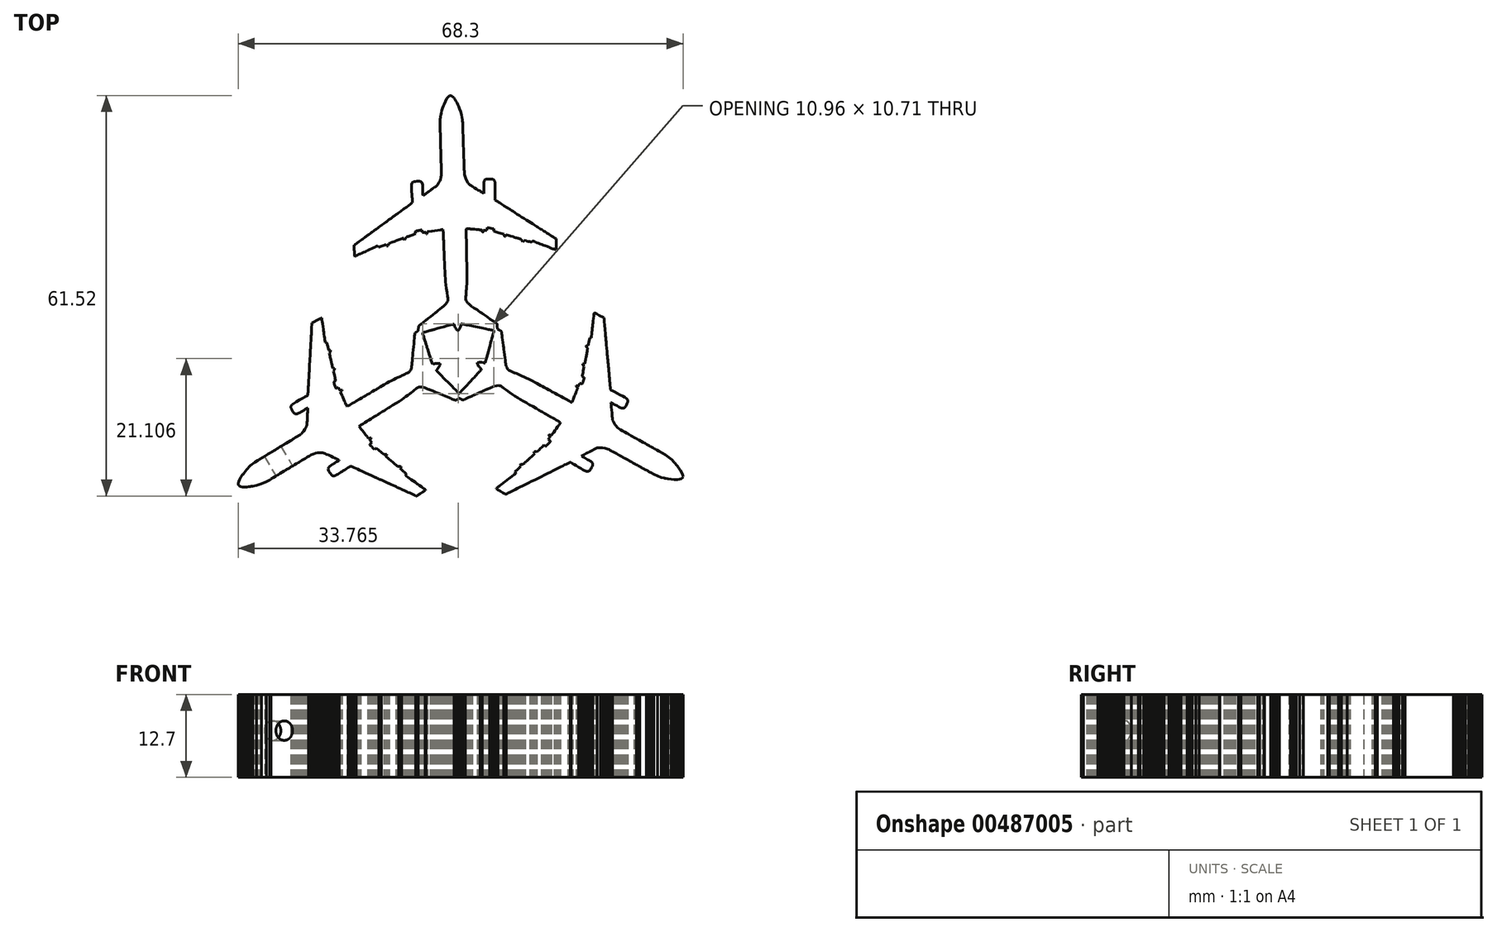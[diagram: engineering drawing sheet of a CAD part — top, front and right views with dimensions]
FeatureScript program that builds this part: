
annotation { "Feature Type Name" : "Feature", "Feature Type Description" : "" }
export const myFeature = defineFeature(function(context is Context, id is Id, definition is map)
    precondition{}
    {
        {
            var Q0;
            Q0=qCreatedBy(makeId("Top.planeOp"),FACE);
            var sketch = newSketch(context, id + "F0", { "sketchPlane" : qUnion([Q0])});
            skLineSegment(sketch, "E0", {"start": v(-1.7, 30.73) * mm, "end": v(-1.76, 30.7) * mm});
            skLineSegment(sketch, "E1", {"start": v(-1.76, 30.7) * mm, "end": v(-1.92, 30.58) * mm});
            skLineSegment(sketch, "E2", {"start": v(-1.92, 30.58) * mm, "end": v(-2.14, 30.3) * mm});
            skLineSegment(sketch, "E3", {"start": v(-2.14, 30.3) * mm, "end": v(-2.37, 29.87) * mm});
            skLineSegment(sketch, "E4", {"start": v(-2.37, 29.87) * mm, "end": v(-2.56, 29.43) * mm});
            skLineSegment(sketch, "E5", {"start": v(-2.56, 29.43) * mm, "end": v(-2.62, 29.28) * mm});
            skLineSegment(sketch, "E6", {"start": v(-2.62, 29.28) * mm, "end": v(-2.66, 29.17) * mm});
            skLineSegment(sketch, "E7", {"start": v(-2.66, 29.17) * mm, "end": v(-2.78, 28.85) * mm});
            skLineSegment(sketch, "E8", {"start": v(-2.78, 28.85) * mm, "end": v(-2.9, 28.46) * mm});
            skLineSegment(sketch, "E9", {"start": v(-2.9, 28.46) * mm, "end": v(-3, 28.1) * mm});
            skLineSegment(sketch, "E10", {"start": v(-3, 28.1) * mm, "end": v(-3.06, 27.8) * mm});
            skLineSegment(sketch, "E11", {"start": v(-3.06, 27.8) * mm, "end": v(-3.08, 27.7) * mm});
            skLineSegment(sketch, "E12", {"start": v(-3.08, 27.7) * mm, "end": v(-3.08, 27.67) * mm});
            skLineSegment(sketch, "E13", {"start": v(-3.08, 27.67) * mm, "end": v(-3.1, 27.57) * mm});
            skLineSegment(sketch, "E14", {"start": v(-3.1, 27.57) * mm, "end": v(-3.12, 27.45) * mm});
            skLineSegment(sketch, "E15", {"start": v(-3.12, 27.45) * mm, "end": v(-3.13, 27.34) * mm});
            skLineSegment(sketch, "E16", {"start": v(-3.13, 27.34) * mm, "end": v(-3.15, 27.22) * mm});
            skLineSegment(sketch, "E17", {"start": v(-3.15, 27.22) * mm, "end": v(-3.16, 27.09) * mm});
            skLineSegment(sketch, "E18", {"start": v(-3.16, 27.09) * mm, "end": v(-3.16, 26.94) * mm});
            skLineSegment(sketch, "E19", {"start": v(-3.16, 26.94) * mm, "end": v(-3.17, 26.77) * mm});
            skLineSegment(sketch, "E20", {"start": v(-3.17, 26.77) * mm, "end": v(-3.17, 26.57) * mm});
            skLineSegment(sketch, "E21", {"start": v(-3.17, 26.57) * mm, "end": v(-3.17, 26.33) * mm});
            skLineSegment(sketch, "E22", {"start": v(-3.17, 26.33) * mm, "end": v(-3.16, 26.04) * mm});
            skLineSegment(sketch, "E23", {"start": v(-3.16, 26.04) * mm, "end": v(-3.16, 25.7) * mm});
            skLineSegment(sketch, "E24", {"start": v(-3.16, 25.7) * mm, "end": v(-3.15, 25.3) * mm});
            skLineSegment(sketch, "E25", {"start": v(-3.15, 25.3) * mm, "end": v(-3.13, 24.85) * mm});
            skLineSegment(sketch, "E26", {"start": v(-3.13, 24.85) * mm, "end": v(-3.12, 24.31) * mm});
            skLineSegment(sketch, "E27", {"start": v(-3.12, 24.31) * mm, "end": v(-3.1, 23.7) * mm});
            skLineSegment(sketch, "E28", {"start": v(-3.1, 23.7) * mm, "end": v(-3.08, 23.18) * mm});
            skLineSegment(sketch, "E29", {"start": v(-3.08, 23.18) * mm, "end": v(-3.08, 23) * mm});
            skLineSegment(sketch, "E30", {"start": v(-3.08, 23) * mm, "end": v(-3.07, 22.82) * mm});
            skLineSegment(sketch, "E31", {"start": v(-3.07, 22.82) * mm, "end": v(-3.06, 22.27) * mm});
            skLineSegment(sketch, "E32", {"start": v(-3.06, 22.27) * mm, "end": v(-3.04, 21.63) * mm});
            skLineSegment(sketch, "E33", {"start": v(-3.04, 21.63) * mm, "end": v(-3.02, 21.08) * mm});
            skLineSegment(sketch, "E34", {"start": v(-3.02, 21.08) * mm, "end": v(-3.01, 20.6) * mm});
            skLineSegment(sketch, "E35", {"start": v(-3.01, 20.6) * mm, "end": v(-3, 20.17) * mm});
            skLineSegment(sketch, "E36", {"start": v(-3, 20.17) * mm, "end": v(-3, 19.79) * mm});
            skLineSegment(sketch, "E37", {"start": v(-3, 19.79) * mm, "end": v(-3, 19.44) * mm});
            skLineSegment(sketch, "E38", {"start": v(-3, 19.44) * mm, "end": v(-3, 19.19) * mm});
            skLineSegment(sketch, "E39", {"start": v(-3, 19.19) * mm, "end": v(-3, 19.1) * mm});
            skLineSegment(sketch, "E40", {"start": v(-3, 19.1) * mm, "end": v(-3, 19.03) * mm});
            skLineSegment(sketch, "E41", {"start": v(-3, 19.03) * mm, "end": v(-3, 18.81) * mm});
            skLineSegment(sketch, "E42", {"start": v(-3, 18.81) * mm, "end": v(-3, 18.59) * mm});
            skLineSegment(sketch, "E43", {"start": v(-3, 18.59) * mm, "end": v(-3, 18.42) * mm});
            skLineSegment(sketch, "E44", {"start": v(-3, 18.42) * mm, "end": v(-3, 18.3) * mm});
            skLineSegment(sketch, "E45", {"start": v(-3, 18.3) * mm, "end": v(-3.02, 18.2) * mm});
            skLineSegment(sketch, "E46", {"start": v(-3.02, 18.2) * mm, "end": v(-3.03, 18.12) * mm});
            skLineSegment(sketch, "E47", {"start": v(-3.03, 18.12) * mm, "end": v(-3.06, 18.04) * mm});
            skLineSegment(sketch, "E48", {"start": v(-3.06, 18.04) * mm, "end": v(-3.08, 17.97) * mm});
            skLineSegment(sketch, "E49", {"start": v(-3.08, 17.97) * mm, "end": v(-3.09, 17.95) * mm});
            skLineSegment(sketch, "E50", {"start": v(-3.09, 17.95) * mm, "end": v(-3.11, 17.88) * mm});
            skLineSegment(sketch, "E51", {"start": v(-3.11, 17.88) * mm, "end": v(-3.2, 17.68) * mm});
            skLineSegment(sketch, "E52", {"start": v(-3.2, 17.68) * mm, "end": v(-3.33, 17.4) * mm});
            skLineSegment(sketch, "E53", {"start": v(-3.33, 17.4) * mm, "end": v(-3.47, 17.16) * mm});
            skLineSegment(sketch, "E54", {"start": v(-3.47, 17.16) * mm, "end": v(-3.55, 17.03) * mm});
            skLineSegment(sketch, "E55", {"start": v(-3.55, 17.03) * mm, "end": v(-3.58, 17) * mm});
            skLineSegment(sketch, "E56", {"start": v(-3.58, 17) * mm, "end": v(-3.6, 16.99) * mm});
            skLineSegment(sketch, "E57", {"start": v(-3.6, 16.99) * mm, "end": v(-3.63, 16.95) * mm});
            skLineSegment(sketch, "E58", {"start": v(-3.63, 16.95) * mm, "end": v(-3.72, 16.88) * mm});
            skLineSegment(sketch, "E59", {"start": v(-3.72, 16.88) * mm, "end": v(-3.82, 16.8) * mm});
            skLineSegment(sketch, "E60", {"start": v(-3.82, 16.8) * mm, "end": v(-3.9, 16.74) * mm});
            skLineSegment(sketch, "E61", {"start": v(-3.9, 16.74) * mm, "end": v(-3.93, 16.72) * mm});
            skLineSegment(sketch, "E62", {"start": v(-3.93, 16.72) * mm, "end": v(-3.96, 16.7) * mm});
            skLineSegment(sketch, "E63", {"start": v(-3.96, 16.7) * mm, "end": v(-4.06, 16.63) * mm});
            skLineSegment(sketch, "E64", {"start": v(-4.06, 16.63) * mm, "end": v(-4.22, 16.52) * mm});
            skLineSegment(sketch, "E65", {"start": v(-4.22, 16.52) * mm, "end": v(-4.38, 16.4) * mm});
            skLineSegment(sketch, "E66", {"start": v(-4.38, 16.4) * mm, "end": v(-4.5, 16.31) * mm});
            skLineSegment(sketch, "E67", {"start": v(-4.5, 16.31) * mm, "end": v(-4.54, 16.29) * mm});
            skLineSegment(sketch, "E68", {"start": v(-4.54, 16.29) * mm, "end": v(-4.58, 16.26) * mm});
            skLineSegment(sketch, "E69", {"start": v(-4.58, 16.26) * mm, "end": v(-4.7, 16.17) * mm});
            skLineSegment(sketch, "E70", {"start": v(-4.7, 16.17) * mm, "end": v(-4.87, 16.05) * mm});
            skLineSegment(sketch, "E71", {"start": v(-4.87, 16.05) * mm, "end": v(-5.03, 15.93) * mm});
            skLineSegment(sketch, "E72", {"start": v(-5.03, 15.93) * mm, "end": v(-5.13, 15.86) * mm});
            skLineSegment(sketch, "E73", {"start": v(-5.13, 15.86) * mm, "end": v(-5.16, 15.83) * mm});
            skLineSegment(sketch, "E74", {"start": v(-5.16, 15.83) * mm, "end": v(-5.2, 15.81) * mm});
            skLineSegment(sketch, "E75", {"start": v(-5.2, 15.81) * mm, "end": v(-5.28, 15.75) * mm});
            skLineSegment(sketch, "E76", {"start": v(-5.28, 15.75) * mm, "end": v(-5.4, 15.66) * mm});
            skLineSegment(sketch, "E77", {"start": v(-5.4, 15.66) * mm, "end": v(-5.5, 15.58) * mm});
            skLineSegment(sketch, "E78", {"start": v(-5.5, 15.58) * mm, "end": v(-5.57, 15.54) * mm});
            skLineSegment(sketch, "E79", {"start": v(-5.57, 15.54) * mm, "end": v(-5.59, 15.52) * mm});
            skLineSegment(sketch, "E80", {"start": v(-5.59, 15.52) * mm, "end": v(-5.6, 15.51) * mm});
            skLineSegment(sketch, "E81", {"start": v(-5.6, 15.51) * mm, "end": v(-5.65, 15.48) * mm});
            skLineSegment(sketch, "E82", {"start": v(-5.65, 15.48) * mm, "end": v(-5.7, 15.45) * mm});
            skLineSegment(sketch, "E83", {"start": v(-5.7, 15.45) * mm, "end": v(-5.74, 15.42) * mm});
            skLineSegment(sketch, "E84", {"start": v(-5.74, 15.42) * mm, "end": v(-5.76, 15.41) * mm});
            skLineSegment(sketch, "E85", {"start": v(-5.76, 15.41) * mm, "end": v(-5.76, 15.41) * mm});
            skLineSegment(sketch, "E86", {"start": v(-5.76, 15.41) * mm, "end": v(-5.77, 15.41) * mm});
            skLineSegment(sketch, "E87", {"start": v(-5.77, 15.41) * mm, "end": v(-5.79, 15.46) * mm});
            skLineSegment(sketch, "E88", {"start": v(-5.79, 15.46) * mm, "end": v(-5.8, 15.61) * mm});
            skLineSegment(sketch, "E89", {"start": v(-5.8, 15.61) * mm, "end": v(-5.82, 15.9) * mm});
            skLineSegment(sketch, "E90", {"start": v(-5.82, 15.9) * mm, "end": v(-5.83, 16.22) * mm});
            skLineSegment(sketch, "E91", {"start": v(-5.83, 16.22) * mm, "end": v(-5.83, 16.32) * mm});
            skLineSegment(sketch, "E92", {"start": v(-5.83, 16.32) * mm, "end": v(-5.83, 16.42) * mm});
            skLineSegment(sketch, "E93", {"start": v(-5.83, 16.42) * mm, "end": v(-5.84, 16.71) * mm});
            skLineSegment(sketch, "E94", {"start": v(-5.84, 16.71) * mm, "end": v(-5.86, 17.01) * mm});
            skLineSegment(sketch, "E95", {"start": v(-5.86, 17.01) * mm, "end": v(-5.89, 17.22) * mm});
            skLineSegment(sketch, "E96", {"start": v(-5.89, 17.22) * mm, "end": v(-5.91, 17.32) * mm});
            skLineSegment(sketch, "E97", {"start": v(-5.91, 17.32) * mm, "end": v(-5.93, 17.35) * mm});
            skLineSegment(sketch, "E98", {"start": v(-5.93, 17.35) * mm, "end": v(-5.95, 17.38) * mm});
            skLineSegment(sketch, "E99", {"start": v(-5.95, 17.38) * mm, "end": v(-6.03, 17.48) * mm});
            skLineSegment(sketch, "E100", {"start": v(-6.03, 17.48) * mm, "end": v(-6.17, 17.56) * mm});
            skLineSegment(sketch, "E101", {"start": v(-6.17, 17.56) * mm, "end": v(-6.37, 17.6) * mm});
            skLineSegment(sketch, "E102", {"start": v(-6.37, 17.6) * mm, "end": v(-6.56, 17.61) * mm});
            skLineSegment(sketch, "E103", {"start": v(-6.56, 17.61) * mm, "end": v(-6.63, 17.6) * mm});
            skLineSegment(sketch, "E104", {"start": v(-6.63, 17.6) * mm, "end": v(-6.72, 17.6) * mm});
            skLineSegment(sketch, "E105", {"start": v(-6.72, 17.6) * mm, "end": v(-7, 17.58) * mm});
            skLineSegment(sketch, "E106", {"start": v(-7, 17.58) * mm, "end": v(-7.24, 17.53) * mm});
            skLineSegment(sketch, "E107", {"start": v(-7.24, 17.53) * mm, "end": v(-7.4, 17.44) * mm});
            skLineSegment(sketch, "E108", {"start": v(-7.4, 17.44) * mm, "end": v(-7.47, 17.35) * mm});
            skLineSegment(sketch, "E109", {"start": v(-7.47, 17.35) * mm, "end": v(-7.5, 17.31) * mm});
            skLineSegment(sketch, "E110", {"start": v(-7.5, 17.31) * mm, "end": v(-7.5, 17.27) * mm});
            skLineSegment(sketch, "E111", {"start": v(-7.5, 17.27) * mm, "end": v(-7.53, 17.09) * mm});
            skLineSegment(sketch, "E112", {"start": v(-7.53, 17.09) * mm, "end": v(-7.54, 16.67) * mm});
            skLineSegment(sketch, "E113", {"start": v(-7.54, 16.67) * mm, "end": v(-7.53, 16.07) * mm});
            skLineSegment(sketch, "E114", {"start": v(-7.53, 16.07) * mm, "end": v(-7.5, 15.5) * mm});
            skLineSegment(sketch, "E115", {"start": v(-7.5, 15.5) * mm, "end": v(-7.48, 15.31) * mm});
            skLineSegment(sketch, "E116", {"start": v(-7.48, 15.31) * mm, "end": v(-7.47, 15.23) * mm});
            skLineSegment(sketch, "E117", {"start": v(-7.47, 15.23) * mm, "end": v(-7.45, 14.96) * mm});
            skLineSegment(sketch, "E118", {"start": v(-7.45, 14.96) * mm, "end": v(-7.43, 14.67) * mm});
            skLineSegment(sketch, "E119", {"start": v(-7.43, 14.67) * mm, "end": v(-7.42, 14.46) * mm});
            skLineSegment(sketch, "E120", {"start": v(-7.42, 14.46) * mm, "end": v(-7.41, 14.4) * mm});
            skLineSegment(sketch, "E121", {"start": v(-7.41, 14.4) * mm, "end": v(-7.41, 14.37) * mm});
            skLineSegment(sketch, "E122", {"start": v(-7.41, 14.37) * mm, "end": v(-7.41, 14.36) * mm});
            skLineSegment(sketch, "E123", {"start": v(-7.41, 14.36) * mm, "end": v(-7.45, 14.32) * mm});
            skLineSegment(sketch, "E124", {"start": v(-7.45, 14.32) * mm, "end": v(-7.56, 14.23) * mm});
            skLineSegment(sketch, "E125", {"start": v(-7.56, 14.23) * mm, "end": v(-7.75, 14.08) * mm});
            skLineSegment(sketch, "E126", {"start": v(-7.75, 14.08) * mm, "end": v(-8, 13.88) * mm});
            skLineSegment(sketch, "E127", {"start": v(-8, 13.88) * mm, "end": v(-8.34, 13.64) * mm});
            skLineSegment(sketch, "E128", {"start": v(-8.34, 13.64) * mm, "end": v(-8.73, 13.35) * mm});
            skLineSegment(sketch, "E129", {"start": v(-8.73, 13.35) * mm, "end": v(-9.2, 13) * mm});
            skLineSegment(sketch, "E130", {"start": v(-9.2, 13) * mm, "end": v(-9.6, 12.72) * mm});
            skLineSegment(sketch, "E131", {"start": v(-9.6, 12.72) * mm, "end": v(-9.73, 12.63) * mm});
            skLineSegment(sketch, "E132", {"start": v(-9.73, 12.63) * mm, "end": v(-9.75, 12.6) * mm});
            skLineSegment(sketch, "E133", {"start": v(-9.75, 12.6) * mm, "end": v(-9.82, 12.56) * mm});
            skLineSegment(sketch, "E134", {"start": v(-9.82, 12.56) * mm, "end": v(-9.95, 12.47) * mm});
            skLineSegment(sketch, "E135", {"start": v(-9.95, 12.47) * mm, "end": v(-10.09, 12.37) * mm});
            skLineSegment(sketch, "E136", {"start": v(-10.09, 12.37) * mm, "end": v(-10.19, 12.3) * mm});
            skLineSegment(sketch, "E137", {"start": v(-10.19, 12.3) * mm, "end": v(-10.22, 12.27) * mm});
            skLineSegment(sketch, "E138", {"start": v(-10.22, 12.27) * mm, "end": v(-10.26, 12.24) * mm});
            skLineSegment(sketch, "E139", {"start": v(-10.26, 12.24) * mm, "end": v(-10.4, 12.13) * mm});
            skLineSegment(sketch, "E140", {"start": v(-10.4, 12.13) * mm, "end": v(-10.69, 11.92) * mm});
            skLineSegment(sketch, "E141", {"start": v(-10.69, 11.92) * mm, "end": v(-11.02, 11.68) * mm});
            skLineSegment(sketch, "E142", {"start": v(-11.02, 11.68) * mm, "end": v(-11.3, 11.48) * mm});
            skLineSegment(sketch, "E143", {"start": v(-11.3, 11.48) * mm, "end": v(-11.38, 11.42) * mm});
            skLineSegment(sketch, "E144", {"start": v(-11.38, 11.42) * mm, "end": v(-11.47, 11.35) * mm});
            skLineSegment(sketch, "E145", {"start": v(-11.47, 11.35) * mm, "end": v(-11.74, 11.16) * mm});
            skLineSegment(sketch, "E146", {"start": v(-11.74, 11.16) * mm, "end": v(-12.1, 10.9) * mm});
            skLineSegment(sketch, "E147", {"start": v(-12.1, 10.9) * mm, "end": v(-12.4, 10.67) * mm});
            skLineSegment(sketch, "E148", {"start": v(-12.4, 10.67) * mm, "end": v(-12.56, 10.55) * mm});
            skLineSegment(sketch, "E149", {"start": v(-12.56, 10.55) * mm, "end": v(-12.62, 10.51) * mm});
            skLineSegment(sketch, "E150", {"start": v(-12.62, 10.51) * mm, "end": v(-12.66, 10.48) * mm});
            skLineSegment(sketch, "E151", {"start": v(-12.66, 10.48) * mm, "end": v(-12.78, 10.4) * mm});
            skLineSegment(sketch, "E152", {"start": v(-12.78, 10.4) * mm, "end": v(-12.94, 10.28) * mm});
            skLineSegment(sketch, "E153", {"start": v(-12.94, 10.28) * mm, "end": v(-13.07, 10.18) * mm});
            skLineSegment(sketch, "E154", {"start": v(-13.07, 10.18) * mm, "end": v(-13.15, 10.12) * mm});
            skLineSegment(sketch, "E155", {"start": v(-13.15, 10.12) * mm, "end": v(-13.17, 10.1) * mm});
            skLineSegment(sketch, "E156", {"start": v(-13.17, 10.1) * mm, "end": v(-13.2, 10.1) * mm});
            skLineSegment(sketch, "E157", {"start": v(-13.2, 10.1) * mm, "end": v(-13.27, 10.04) * mm});
            skLineSegment(sketch, "E158", {"start": v(-13.27, 10.04) * mm, "end": v(-13.41, 9.93) * mm});
            skLineSegment(sketch, "E159", {"start": v(-13.41, 9.93) * mm, "end": v(-13.58, 9.8) * mm});
            skLineSegment(sketch, "E160", {"start": v(-13.58, 9.8) * mm, "end": v(-13.71, 9.71) * mm});
            skLineSegment(sketch, "E161", {"start": v(-13.71, 9.71) * mm, "end": v(-13.76, 9.68) * mm});
            skLineSegment(sketch, "E162", {"start": v(-13.76, 9.68) * mm, "end": v(-13.8, 9.65) * mm});
            skLineSegment(sketch, "E163", {"start": v(-13.8, 9.65) * mm, "end": v(-13.93, 9.55) * mm});
            skLineSegment(sketch, "E164", {"start": v(-13.93, 9.55) * mm, "end": v(-14.07, 9.45) * mm});
            skLineSegment(sketch, "E165", {"start": v(-14.07, 9.45) * mm, "end": v(-14.18, 9.36) * mm});
            skLineSegment(sketch, "E166", {"start": v(-14.18, 9.36) * mm, "end": v(-14.23, 9.33) * mm});
            skLineSegment(sketch, "E167", {"start": v(-14.23, 9.33) * mm, "end": v(-14.24, 9.32) * mm});
            skLineSegment(sketch, "E168", {"start": v(-14.24, 9.32) * mm, "end": v(-14.25, 9.32) * mm});
            skLineSegment(sketch, "E169", {"start": v(-14.25, 9.32) * mm, "end": v(-14.3, 9.28) * mm});
            skLineSegment(sketch, "E170", {"start": v(-14.3, 9.28) * mm, "end": v(-14.4, 9.21) * mm});
            skLineSegment(sketch, "E171", {"start": v(-14.4, 9.21) * mm, "end": v(-14.52, 9.12) * mm});
            skLineSegment(sketch, "E172", {"start": v(-14.52, 9.12) * mm, "end": v(-14.63, 9.04) * mm});
            skLineSegment(sketch, "E173", {"start": v(-14.63, 9.04) * mm, "end": v(-14.66, 9.01) * mm});
            skLineSegment(sketch, "E174", {"start": v(-14.66, 9.01) * mm, "end": v(-14.7, 8.99) * mm});
            skLineSegment(sketch, "E175", {"start": v(-14.7, 8.99) * mm, "end": v(-14.81, 8.9) * mm});
            skLineSegment(sketch, "E176", {"start": v(-14.81, 8.9) * mm, "end": v(-14.95, 8.8) * mm});
            skLineSegment(sketch, "E177", {"start": v(-14.95, 8.8) * mm, "end": v(-15.07, 8.72) * mm});
            skLineSegment(sketch, "E178", {"start": v(-15.07, 8.72) * mm, "end": v(-15.13, 8.67) * mm});
            skLineSegment(sketch, "E179", {"start": v(-15.13, 8.67) * mm, "end": v(-15.15, 8.66) * mm});
            skLineSegment(sketch, "E180", {"start": v(-15.15, 8.66) * mm, "end": v(-15.17, 8.64) * mm});
            skLineSegment(sketch, "E181", {"start": v(-15.17, 8.64) * mm, "end": v(-15.24, 8.59) * mm});
            skLineSegment(sketch, "E182", {"start": v(-15.24, 8.59) * mm, "end": v(-15.4, 8.48) * mm});
            skLineSegment(sketch, "E183", {"start": v(-15.4, 8.48) * mm, "end": v(-15.58, 8.34) * mm});
            skLineSegment(sketch, "E184", {"start": v(-15.58, 8.34) * mm, "end": v(-15.74, 8.23) * mm});
            skLineSegment(sketch, "E185", {"start": v(-15.74, 8.23) * mm, "end": v(-15.79, 8.2) * mm});
            skLineSegment(sketch, "E186", {"start": v(-15.79, 8.2) * mm, "end": v(-15.84, 8.15) * mm});
            skLineSegment(sketch, "E187", {"start": v(-15.84, 8.15) * mm, "end": v(-15.99, 8.04) * mm});
            skLineSegment(sketch, "E188", {"start": v(-15.99, 8.04) * mm, "end": v(-16.16, 7.92) * mm});
            skLineSegment(sketch, "E189", {"start": v(-16.16, 7.92) * mm, "end": v(-16.28, 7.83) * mm});
            skLineSegment(sketch, "E190", {"start": v(-16.28, 7.83) * mm, "end": v(-16.33, 7.8) * mm});
            skLineSegment(sketch, "E191", {"start": v(-16.33, 7.8) * mm, "end": v(-16.34, 7.8) * mm});
            skLineSegment(sketch, "E192", {"start": v(-16.34, 7.8) * mm, "end": v(-16.35, 7.79) * mm});
            skLineSegment(sketch, "E193", {"start": v(-16.35, 7.79) * mm, "end": v(-16.36, 7.75) * mm});
            skLineSegment(sketch, "E194", {"start": v(-16.36, 7.75) * mm, "end": v(-16.37, 7.63) * mm});
            skLineSegment(sketch, "E195", {"start": v(-16.37, 7.63) * mm, "end": v(-16.37, 7.4) * mm});
            skLineSegment(sketch, "E196", {"start": v(-16.37, 7.4) * mm, "end": v(-16.35, 7.08) * mm});
            skLineSegment(sketch, "E197", {"start": v(-16.35, 7.08) * mm, "end": v(-16.35, 6.98) * mm});
            skLineSegment(sketch, "E198", {"start": v(-16.35, 6.98) * mm, "end": v(-16.34, 6.9) * mm});
            skLineSegment(sketch, "E199", {"start": v(-16.34, 6.9) * mm, "end": v(-16.33, 6.67) * mm});
            skLineSegment(sketch, "E200", {"start": v(-16.33, 6.67) * mm, "end": v(-16.31, 6.4) * mm});
            skLineSegment(sketch, "E201", {"start": v(-16.31, 6.4) * mm, "end": v(-16.3, 6.21) * mm});
            skLineSegment(sketch, "E202", {"start": v(-16.3, 6.21) * mm, "end": v(-16.29, 6.13) * mm});
            skLineSegment(sketch, "E203", {"start": v(-16.29, 6.13) * mm, "end": v(-16.29, 6.12) * mm});
            skLineSegment(sketch, "E204", {"start": v(-16.29, 6.12) * mm, "end": v(-16.27, 6.05) * mm});
            skLineSegment(sketch, "E205", {"start": v(-16.27, 6.05) * mm, "end": v(-16.11, 6.13) * mm});
            skLineSegment(sketch, "E206", {"start": v(-16.11, 6.13) * mm, "end": v(-16.09, 6.14) * mm});
            skLineSegment(sketch, "E207", {"start": v(-16.09, 6.14) * mm, "end": v(-16, 6.18) * mm});
            skLineSegment(sketch, "E208", {"start": v(-16, 6.18) * mm, "end": v(-15.85, 6.25) * mm});
            skLineSegment(sketch, "E209", {"start": v(-15.85, 6.25) * mm, "end": v(-15.65, 6.34) * mm});
            skLineSegment(sketch, "E210", {"start": v(-15.65, 6.34) * mm, "end": v(-15.49, 6.42) * mm});
            skLineSegment(sketch, "E211", {"start": v(-15.49, 6.42) * mm, "end": v(-15.43, 6.44) * mm});
            skLineSegment(sketch, "E212", {"start": v(-15.43, 6.44) * mm, "end": v(-15.37, 6.47) * mm});
            skLineSegment(sketch, "E213", {"start": v(-15.37, 6.47) * mm, "end": v(-15.2, 6.55) * mm});
            skLineSegment(sketch, "E214", {"start": v(-15.2, 6.55) * mm, "end": v(-14.94, 6.67) * mm});
            skLineSegment(sketch, "E215", {"start": v(-14.94, 6.67) * mm, "end": v(-14.69, 6.78) * mm});
            skLineSegment(sketch, "E216", {"start": v(-14.69, 6.78) * mm, "end": v(-14.53, 6.85) * mm});
            skLineSegment(sketch, "E217", {"start": v(-14.53, 6.85) * mm, "end": v(-14.48, 6.88) * mm});
            skLineSegment(sketch, "E218", {"start": v(-14.48, 6.88) * mm, "end": v(-14.41, 6.9) * mm});
            skLineSegment(sketch, "E219", {"start": v(-14.41, 6.9) * mm, "end": v(-14.22, 7) * mm});
            skLineSegment(sketch, "E220", {"start": v(-14.22, 7) * mm, "end": v(-13.94, 7.12) * mm});
            skLineSegment(sketch, "E221", {"start": v(-13.94, 7.12) * mm, "end": v(-13.67, 7.25) * mm});
            skLineSegment(sketch, "E222", {"start": v(-13.67, 7.25) * mm, "end": v(-13.4, 7.37) * mm});
            skLineSegment(sketch, "E223", {"start": v(-13.4, 7.37) * mm, "end": v(-13.17, 7.47) * mm});
            skLineSegment(sketch, "E224", {"start": v(-13.17, 7.47) * mm, "end": v(-12.98, 7.56) * mm});
            skLineSegment(sketch, "E225", {"start": v(-12.98, 7.56) * mm, "end": v(-12.85, 7.62) * mm});
            skLineSegment(sketch, "E226", {"start": v(-12.85, 7.62) * mm, "end": v(-12.8, 7.64) * mm});
            skLineSegment(sketch, "E227", {"start": v(-12.8, 7.64) * mm, "end": v(-12.8, 7.65) * mm});
            skLineSegment(sketch, "E228", {"start": v(-12.8, 7.65) * mm, "end": v(-12.79, 7.65) * mm});
            skLineSegment(sketch, "E229", {"start": v(-12.79, 7.65) * mm, "end": v(-12.75, 7.63) * mm});
            skLineSegment(sketch, "E230", {"start": v(-12.75, 7.63) * mm, "end": v(-12.7, 7.58) * mm});
            skLineSegment(sketch, "E231", {"start": v(-12.7, 7.58) * mm, "end": v(-12.7, 7.56) * mm});
            skLineSegment(sketch, "E232", {"start": v(-12.7, 7.56) * mm, "end": v(-12.65, 7.46) * mm});
            skLineSegment(sketch, "E233", {"start": v(-12.65, 7.46) * mm, "end": v(-12.12, 7.65) * mm});
            skLineSegment(sketch, "E234", {"start": v(-12.12, 7.65) * mm, "end": v(-12.07, 7.66) * mm});
            skLineSegment(sketch, "E235", {"start": v(-12.07, 7.66) * mm, "end": v(-11.91, 7.72) * mm});
            skLineSegment(sketch, "E236", {"start": v(-11.91, 7.72) * mm, "end": v(-11.73, 7.78) * mm});
            skLineSegment(sketch, "E237", {"start": v(-11.73, 7.78) * mm, "end": v(-11.6, 7.83) * mm});
            skLineSegment(sketch, "E238", {"start": v(-11.6, 7.83) * mm, "end": v(-11.54, 7.85) * mm});
            skLineSegment(sketch, "E239", {"start": v(-11.54, 7.85) * mm, "end": v(-11.53, 7.85) * mm});
            skLineSegment(sketch, "E240", {"start": v(-11.53, 7.85) * mm, "end": v(-11.52, 7.85) * mm});
            skLineSegment(sketch, "E241", {"start": v(-11.52, 7.85) * mm, "end": v(-11.48, 7.84) * mm});
            skLineSegment(sketch, "E242", {"start": v(-11.48, 7.84) * mm, "end": v(-11.45, 7.8) * mm});
            skLineSegment(sketch, "E243", {"start": v(-11.45, 7.8) * mm, "end": v(-11.44, 7.78) * mm});
            skLineSegment(sketch, "E244", {"start": v(-11.44, 7.78) * mm, "end": v(-11.43, 7.75) * mm});
            skLineSegment(sketch, "E245", {"start": v(-11.43, 7.75) * mm, "end": v(-11.37, 7.67) * mm});
            skLineSegment(sketch, "E246", {"start": v(-11.37, 7.67) * mm, "end": v(-11.28, 7.64) * mm});
            skLineSegment(sketch, "E247", {"start": v(-11.28, 7.64) * mm, "end": v(-11.2, 7.7) * mm});
            skLineSegment(sketch, "E248", {"start": v(-11.2, 7.7) * mm, "end": v(-11.13, 7.82) * mm});
            skLineSegment(sketch, "E249", {"start": v(-11.13, 7.82) * mm, "end": v(-11.11, 7.86) * mm});
            skLineSegment(sketch, "E250", {"start": v(-11.11, 7.86) * mm, "end": v(-11.05, 8.04) * mm});
            skLineSegment(sketch, "E251", {"start": v(-11.05, 8.04) * mm, "end": v(-10.73, 8.15) * mm});
            skLineSegment(sketch, "E252", {"start": v(-10.73, 8.15) * mm, "end": v(-10.7, 8.17) * mm});
            skLineSegment(sketch, "E253", {"start": v(-10.7, 8.17) * mm, "end": v(-10.57, 8.21) * mm});
            skLineSegment(sketch, "E254", {"start": v(-10.57, 8.21) * mm, "end": v(-10.37, 8.28) * mm});
            skLineSegment(sketch, "E255", {"start": v(-10.37, 8.28) * mm, "end": v(-10.16, 8.36) * mm});
            skLineSegment(sketch, "E256", {"start": v(-10.16, 8.36) * mm, "end": v(-10.01, 8.42) * mm});
            skLineSegment(sketch, "E257", {"start": v(-10.01, 8.42) * mm, "end": v(-9.96, 8.44) * mm});
            skLineSegment(sketch, "E258", {"start": v(-9.96, 8.44) * mm, "end": v(-9.92, 8.45) * mm});
            skLineSegment(sketch, "E259", {"start": v(-9.92, 8.45) * mm, "end": v(-9.78, 8.5) * mm});
            skLineSegment(sketch, "E260", {"start": v(-9.78, 8.5) * mm, "end": v(-9.58, 8.57) * mm});
            skLineSegment(sketch, "E261", {"start": v(-9.58, 8.57) * mm, "end": v(-9.39, 8.65) * mm});
            skLineSegment(sketch, "E262", {"start": v(-9.39, 8.65) * mm, "end": v(-9.2, 8.71) * mm});
            skLineSegment(sketch, "E263", {"start": v(-9.2, 8.71) * mm, "end": v(-9.03, 8.77) * mm});
            skLineSegment(sketch, "E264", {"start": v(-9.03, 8.77) * mm, "end": v(-8.9, 8.82) * mm});
            skLineSegment(sketch, "E265", {"start": v(-8.9, 8.82) * mm, "end": v(-8.8, 8.85) * mm});
            skLineSegment(sketch, "E266", {"start": v(-8.8, 8.85) * mm, "end": v(-8.78, 8.87) * mm});
            skLineSegment(sketch, "E267", {"start": v(-8.78, 8.87) * mm, "end": v(-8.77, 8.87) * mm});
            skLineSegment(sketch, "E268", {"start": v(-8.77, 8.87) * mm, "end": v(-8.77, 8.87) * mm});
            skLineSegment(sketch, "E269", {"start": v(-8.77, 8.87) * mm, "end": v(-8.76, 8.84) * mm});
            skLineSegment(sketch, "E270", {"start": v(-8.76, 8.84) * mm, "end": v(-8.74, 8.79) * mm});
            skLineSegment(sketch, "E271", {"start": v(-8.74, 8.79) * mm, "end": v(-8.74, 8.77) * mm});
            skLineSegment(sketch, "E272", {"start": v(-8.74, 8.77) * mm, "end": v(-8.73, 8.74) * mm});
            skLineSegment(sketch, "E273", {"start": v(-8.73, 8.74) * mm, "end": v(-8.68, 8.65) * mm});
            skLineSegment(sketch, "E274", {"start": v(-8.68, 8.65) * mm, "end": v(-8.62, 8.62) * mm});
            skLineSegment(sketch, "E275", {"start": v(-8.62, 8.62) * mm, "end": v(-8.54, 8.68) * mm});
            skLineSegment(sketch, "E276", {"start": v(-8.54, 8.68) * mm, "end": v(-8.47, 8.79) * mm});
            skLineSegment(sketch, "E277", {"start": v(-8.47, 8.79) * mm, "end": v(-8.45, 8.83) * mm});
            skLineSegment(sketch, "E278", {"start": v(-8.45, 8.83) * mm, "end": v(-8.45, 8.84) * mm});
            skLineSegment(sketch, "E279", {"start": v(-8.45, 8.84) * mm, "end": v(-8.43, 8.9) * mm});
            skLineSegment(sketch, "E280", {"start": v(-8.43, 8.9) * mm, "end": v(-8.4, 8.95) * mm});
            skLineSegment(sketch, "E281", {"start": v(-8.4, 8.95) * mm, "end": v(-8.37, 9) * mm});
            skLineSegment(sketch, "E282", {"start": v(-8.37, 9) * mm, "end": v(-8.36, 9.01) * mm});
            skLineSegment(sketch, "E283", {"start": v(-8.36, 9.01) * mm, "end": v(-8.35, 9.02) * mm});
            skLineSegment(sketch, "E284", {"start": v(-8.35, 9.02) * mm, "end": v(-8.35, 9.02) * mm});
            skLineSegment(sketch, "E285", {"start": v(-8.35, 9.02) * mm, "end": v(-8.3, 9.04) * mm});
            skLineSegment(sketch, "E286", {"start": v(-8.3, 9.04) * mm, "end": v(-8.2, 9.07) * mm});
            skLineSegment(sketch, "E287", {"start": v(-8.2, 9.07) * mm, "end": v(-8.07, 9.12) * mm});
            skLineSegment(sketch, "E288", {"start": v(-8.07, 9.12) * mm, "end": v(-7.95, 9.17) * mm});
            skLineSegment(sketch, "E289", {"start": v(-7.95, 9.17) * mm, "end": v(-7.9, 9.18) * mm});
            skLineSegment(sketch, "E290", {"start": v(-7.9, 9.18) * mm, "end": v(-7.86, 9.2) * mm});
            skLineSegment(sketch, "E291", {"start": v(-7.86, 9.2) * mm, "end": v(-7.72, 9.25) * mm});
            skLineSegment(sketch, "E292", {"start": v(-7.72, 9.25) * mm, "end": v(-7.53, 9.32) * mm});
            skLineSegment(sketch, "E293", {"start": v(-7.53, 9.32) * mm, "end": v(-7.36, 9.38) * mm});
            skLineSegment(sketch, "E294", {"start": v(-7.36, 9.38) * mm, "end": v(-7.25, 9.42) * mm});
            skLineSegment(sketch, "E295", {"start": v(-7.25, 9.42) * mm, "end": v(-7.22, 9.44) * mm});
            skLineSegment(sketch, "E296", {"start": v(-7.22, 9.44) * mm, "end": v(-6.94, 9.54) * mm});
            skLineSegment(sketch, "E297", {"start": v(-6.94, 9.54) * mm, "end": v(-6.96, 9.72) * mm});
            skLineSegment(sketch, "E298", {"start": v(-6.96, 9.72) * mm, "end": v(-6.96, 9.75) * mm});
            skLineSegment(sketch, "E299", {"start": v(-6.96, 9.75) * mm, "end": v(-6.97, 9.83) * mm});
            skLineSegment(sketch, "E300", {"start": v(-6.97, 9.83) * mm, "end": v(-6.97, 9.88) * mm});
            skLineSegment(sketch, "E301", {"start": v(-6.97, 9.88) * mm, "end": v(-6.94, 9.9) * mm});
            skLineSegment(sketch, "E302", {"start": v(-6.94, 9.9) * mm, "end": v(-6.9, 9.92) * mm});
            skLineSegment(sketch, "E303", {"start": v(-6.9, 9.92) * mm, "end": v(-6.89, 9.93) * mm});
            skLineSegment(sketch, "E304", {"start": v(-6.89, 9.93) * mm, "end": v(-6.87, 9.93) * mm});
            skLineSegment(sketch, "E305", {"start": v(-6.87, 9.93) * mm, "end": v(-6.82, 9.94) * mm});
            skLineSegment(sketch, "E306", {"start": v(-6.82, 9.94) * mm, "end": v(-6.7, 9.97) * mm});
            skLineSegment(sketch, "E307", {"start": v(-6.7, 9.97) * mm, "end": v(-6.55, 10) * mm});
            skLineSegment(sketch, "E308", {"start": v(-6.55, 10) * mm, "end": v(-6.43, 10.04) * mm});
            skLineSegment(sketch, "E309", {"start": v(-6.43, 10.04) * mm, "end": v(-6.4, 10.05) * mm});
            skLineSegment(sketch, "E310", {"start": v(-6.4, 10.05) * mm, "end": v(-6.35, 10.06) * mm});
            skLineSegment(sketch, "E311", {"start": v(-6.35, 10.06) * mm, "end": v(-6.24, 10.08) * mm});
            skLineSegment(sketch, "E312", {"start": v(-6.24, 10.08) * mm, "end": v(-6.1, 10.1) * mm});
            skLineSegment(sketch, "E313", {"start": v(-6.1, 10.1) * mm, "end": v(-6.01, 10.12) * mm});
            skLineSegment(sketch, "E314", {"start": v(-6.01, 10.12) * mm, "end": v(-5.98, 10.13) * mm});
            skLineSegment(sketch, "E315", {"start": v(-5.98, 10.13) * mm, "end": v(-5.97, 10.12) * mm});
            skLineSegment(sketch, "E316", {"start": v(-5.97, 10.12) * mm, "end": v(-5.97, 10.12) * mm});
            skLineSegment(sketch, "E317", {"start": v(-5.97, 10.12) * mm, "end": v(-5.95, 10.06) * mm});
            skLineSegment(sketch, "E318", {"start": v(-5.95, 10.06) * mm, "end": v(-5.92, 9.95) * mm});
            skLineSegment(sketch, "E319", {"start": v(-5.92, 9.95) * mm, "end": v(-5.92, 9.93) * mm});
            skLineSegment(sketch, "E320", {"start": v(-5.92, 9.93) * mm, "end": v(-5.88, 9.76) * mm});
            skLineSegment(sketch, "E321", {"start": v(-5.88, 9.76) * mm, "end": v(-5.61, 9.77) * mm});
            skLineSegment(sketch, "E322", {"start": v(-5.61, 9.77) * mm, "end": v(-5.34, 9.78) * mm});
            skLineSegment(sketch, "E323", {"start": v(-5.34, 9.78) * mm, "end": v(-5.31, 9.63) * mm});
            skLineSegment(sketch, "E324", {"start": v(-5.31, 9.63) * mm, "end": v(-5.3, 9.6) * mm});
            skLineSegment(sketch, "E325", {"start": v(-5.3, 9.6) * mm, "end": v(-5.27, 9.52) * mm});
            skLineSegment(sketch, "E326", {"start": v(-5.27, 9.52) * mm, "end": v(-5.23, 9.49) * mm});
            skLineSegment(sketch, "E327", {"start": v(-5.23, 9.49) * mm, "end": v(-5.18, 9.54) * mm});
            skLineSegment(sketch, "E328", {"start": v(-5.18, 9.54) * mm, "end": v(-5.15, 9.64) * mm});
            skLineSegment(sketch, "E329", {"start": v(-5.15, 9.64) * mm, "end": v(-5.14, 9.67) * mm});
            skLineSegment(sketch, "E330", {"start": v(-5.14, 9.67) * mm, "end": v(-5.1, 9.86) * mm});
            skLineSegment(sketch, "E331", {"start": v(-5.1, 9.86) * mm, "end": v(-4.49, 9.94) * mm});
            skLineSegment(sketch, "E332", {"start": v(-4.49, 9.94) * mm, "end": v(-4.37, 9.96) * mm});
            skLineSegment(sketch, "E333", {"start": v(-4.37, 9.96) * mm, "end": v(-4, 10.01) * mm});
            skLineSegment(sketch, "E334", {"start": v(-4, 10.01) * mm, "end": v(-3.53, 10.09) * mm});
            skLineSegment(sketch, "E335", {"start": v(-3.53, 10.09) * mm, "end": v(-3.11, 10.15) * mm});
            skLineSegment(sketch, "E336", {"start": v(-3.11, 10.15) * mm, "end": v(-2.9, 10.18) * mm});
            skLineSegment(sketch, "E337", {"start": v(-2.9, 10.18) * mm, "end": v(-2.84, 10.2) * mm});
            skLineSegment(sketch, "E338", {"start": v(-2.84, 10.2) * mm, "end": v(-2.72, 10.22) * mm});
            skLineSegment(sketch, "E339", {"start": v(-2.72, 10.22) * mm, "end": v(-2.7, 9.95) * mm});
            skLineSegment(sketch, "E340", {"start": v(-2.7, 9.95) * mm, "end": v(-2.7, 9.92) * mm});
            skLineSegment(sketch, "E341", {"start": v(-2.7, 9.92) * mm, "end": v(-2.68, 9.78) * mm});
            skLineSegment(sketch, "E342", {"start": v(-2.68, 9.78) * mm, "end": v(-2.67, 9.51) * mm});
            skLineSegment(sketch, "E343", {"start": v(-2.67, 9.51) * mm, "end": v(-2.66, 9.18) * mm});
            skLineSegment(sketch, "E344", {"start": v(-2.66, 9.18) * mm, "end": v(-2.65, 8.92) * mm});
            skLineSegment(sketch, "E345", {"start": v(-2.65, 8.92) * mm, "end": v(-2.64, 8.83) * mm});
            skLineSegment(sketch, "E346", {"start": v(-2.64, 8.83) * mm, "end": v(-2.64, 8.73) * mm});
            skLineSegment(sketch, "E347", {"start": v(-2.64, 8.73) * mm, "end": v(-2.62, 8.41) * mm});
            skLineSegment(sketch, "E348", {"start": v(-2.62, 8.41) * mm, "end": v(-2.6, 7.9) * mm});
            skLineSegment(sketch, "E349", {"start": v(-2.6, 7.9) * mm, "end": v(-2.58, 7.35) * mm});
            skLineSegment(sketch, "E350", {"start": v(-2.58, 7.35) * mm, "end": v(-2.56, 6.98) * mm});
            skLineSegment(sketch, "E351", {"start": v(-2.56, 6.98) * mm, "end": v(-2.56, 6.85) * mm});
            skLineSegment(sketch, "E352", {"start": v(-2.56, 6.85) * mm, "end": v(-2.55, 6.72) * mm});
            skLineSegment(sketch, "E353", {"start": v(-2.55, 6.72) * mm, "end": v(-2.53, 6.31) * mm});
            skLineSegment(sketch, "E354", {"start": v(-2.53, 6.31) * mm, "end": v(-2.5, 5.68) * mm});
            skLineSegment(sketch, "E355", {"start": v(-2.5, 5.68) * mm, "end": v(-2.48, 5.03) * mm});
            skLineSegment(sketch, "E356", {"start": v(-2.48, 5.03) * mm, "end": v(-2.46, 4.6) * mm});
            skLineSegment(sketch, "E357", {"start": v(-2.46, 4.6) * mm, "end": v(-2.46, 4.45) * mm});
            skLineSegment(sketch, "E358", {"start": v(-2.46, 4.45) * mm, "end": v(-2.45, 4.27) * mm});
            skLineSegment(sketch, "E359", {"start": v(-2.45, 4.27) * mm, "end": v(-2.43, 3.74) * mm});
            skLineSegment(sketch, "E360", {"start": v(-2.43, 3.74) * mm, "end": v(-2.4, 3.16) * mm});
            skLineSegment(sketch, "E361", {"start": v(-2.4, 3.16) * mm, "end": v(-2.37, 2.65) * mm});
            skLineSegment(sketch, "E362", {"start": v(-2.37, 2.65) * mm, "end": v(-2.33, 2.18) * mm});
            skLineSegment(sketch, "E363", {"start": v(-2.33, 2.18) * mm, "end": v(-2.27, 1.7) * mm});
            skLineSegment(sketch, "E364", {"start": v(-2.27, 1.7) * mm, "end": v(-2.2, 1.16) * mm});
            skLineSegment(sketch, "E365", {"start": v(-2.2, 1.16) * mm, "end": v(-2.1, 0.52) * mm});
            skLineSegment(sketch, "E366", {"start": v(-2.1, 0.52) * mm, "end": v(-2.02, -0.07) * mm});
            skLineSegment(sketch, "E367", {"start": v(-2.02, -0.07) * mm, "end": v(-1.99, -0.27) * mm});
            skLineSegment(sketch, "E368", {"start": v(-1.99, -0.27) * mm, "end": v(-1.98, -0.3) * mm});
            skLineSegment(sketch, "E369", {"start": v(-1.98, -0.3) * mm, "end": v(-1.97, -0.42) * mm});
            skLineSegment(sketch, "E370", {"start": v(-1.97, -0.42) * mm, "end": v(-1.96, -0.54) * mm});
            skLineSegment(sketch, "E371", {"start": v(-1.96, -0.54) * mm, "end": v(-1.96, -0.64) * mm});
            skLineSegment(sketch, "E372", {"start": v(-1.96, -0.64) * mm, "end": v(-1.96, -0.7) * mm});
            skLineSegment(sketch, "E373", {"start": v(-1.96, -0.7) * mm, "end": v(-1.97, -0.71) * mm});
            skLineSegment(sketch, "E374", {"start": v(-1.97, -0.71) * mm, "end": v(-1.98, -0.77) * mm});
            skLineSegment(sketch, "E375", {"start": v(-1.98, -0.77) * mm, "end": v(-2.06, -0.94) * mm});
            skLineSegment(sketch, "E376", {"start": v(-2.06, -0.94) * mm, "end": v(-2.22, -1.18) * mm});
            skLineSegment(sketch, "E377", {"start": v(-2.22, -1.18) * mm, "end": v(-2.45, -1.44) * mm});
            skLineSegment(sketch, "E378", {"start": v(-2.45, -1.44) * mm, "end": v(-2.67, -1.63) * mm});
            skLineSegment(sketch, "E379", {"start": v(-2.67, -1.63) * mm, "end": v(-2.74, -1.69) * mm});
            skLineSegment(sketch, "E380", {"start": v(-2.74, -1.69) * mm, "end": v(-2.77, -1.71) * mm});
            skLineSegment(sketch, "E381", {"start": v(-2.77, -1.71) * mm, "end": v(-2.9, -1.81) * mm});
            skLineSegment(sketch, "E382", {"start": v(-2.9, -1.81) * mm, "end": v(-3.16, -2.02) * mm});
            skLineSegment(sketch, "E383", {"start": v(-3.16, -2.02) * mm, "end": v(-3.49, -2.28) * mm});
            skLineSegment(sketch, "E384", {"start": v(-3.49, -2.28) * mm, "end": v(-3.76, -2.5) * mm});
            skLineSegment(sketch, "E385", {"start": v(-3.76, -2.5) * mm, "end": v(-3.85, -2.57) * mm});
            skLineSegment(sketch, "E386", {"start": v(-3.85, -2.57) * mm, "end": v(-3.95, -2.65) * mm});
            skLineSegment(sketch, "E387", {"start": v(-3.95, -2.65) * mm, "end": v(-4.24, -2.88) * mm});
            skLineSegment(sketch, "E388", {"start": v(-4.24, -2.88) * mm, "end": v(-4.63, -3.19) * mm});
            skLineSegment(sketch, "E389", {"start": v(-4.63, -3.19) * mm, "end": v(-4.99, -3.47) * mm});
            skLineSegment(sketch, "E390", {"start": v(-4.99, -3.47) * mm, "end": v(-5.2, -3.64) * mm});
            skLineSegment(sketch, "E391", {"start": v(-5.2, -3.64) * mm, "end": v(-5.26, -3.7) * mm});
            skLineSegment(sketch, "E392", {"start": v(-5.26, -3.7) * mm, "end": v(-5.31, -3.73) * mm});
            skLineSegment(sketch, "E393", {"start": v(-5.31, -3.73) * mm, "end": v(-5.47, -3.85) * mm});
            skLineSegment(sketch, "E394", {"start": v(-5.47, -3.85) * mm, "end": v(-5.65, -4) * mm});
            skLineSegment(sketch, "E395", {"start": v(-5.65, -4) * mm, "end": v(-5.78, -4.1) * mm});
            skLineSegment(sketch, "E396", {"start": v(-5.78, -4.1) * mm, "end": v(-5.84, -4.15) * mm});
            skLineSegment(sketch, "E397", {"start": v(-5.84, -4.15) * mm, "end": v(-5.85, -4.16) * mm});
            skLineSegment(sketch, "E398", {"start": v(-5.85, -4.16) * mm, "end": v(-5.86, -4.16) * mm});
            skLineSegment(sketch, "E399", {"start": v(-5.86, -4.16) * mm, "end": v(-5.9, -4.2) * mm});
            skLineSegment(sketch, "E400", {"start": v(-5.9, -4.2) * mm, "end": v(-5.98, -4.26) * mm});
            skLineSegment(sketch, "E401", {"start": v(-5.98, -4.26) * mm, "end": v(-6.09, -4.35) * mm});
            skLineSegment(sketch, "E402", {"start": v(-6.09, -4.35) * mm, "end": v(-6.18, -4.42) * mm});
            skLineSegment(sketch, "E403", {"start": v(-6.18, -4.42) * mm, "end": v(-6.2, -4.45) * mm});
            skLineSegment(sketch, "E404", {"start": v(-6.2, -4.45) * mm, "end": v(-6.5, -4.68) * mm});
            skLineSegment(sketch, "E405", {"start": v(-6.5, -4.68) * mm, "end": v(-6.52, -5.38) * mm});
            skLineSegment(sketch, "E406", {"start": v(-6.52, -5.38) * mm, "end": v(-6.75, -5.52) * mm});
            skLineSegment(sketch, "E407", {"start": v(-6.75, -5.52) * mm, "end": v(-6.77, -5.53) * mm});
            skLineSegment(sketch, "E408", {"start": v(-6.77, -5.53) * mm, "end": v(-6.84, -5.58) * mm});
            skLineSegment(sketch, "E409", {"start": v(-6.84, -5.58) * mm, "end": v(-6.92, -5.63) * mm});
            skLineSegment(sketch, "E410", {"start": v(-6.92, -5.63) * mm, "end": v(-6.98, -5.67) * mm});
            skLineSegment(sketch, "E411", {"start": v(-6.98, -5.67) * mm, "end": v(-7, -5.69) * mm});
            skLineSegment(sketch, "E412", {"start": v(-7, -5.69) * mm, "end": v(-7, -5.7) * mm});
            skLineSegment(sketch, "E413", {"start": v(-7, -5.7) * mm, "end": v(-7.01, -5.7) * mm});
            skLineSegment(sketch, "E414", {"start": v(-7.01, -5.7) * mm, "end": v(-7.03, -5.76) * mm});
            skLineSegment(sketch, "E415", {"start": v(-7.03, -5.76) * mm, "end": v(-7.05, -5.93) * mm});
            skLineSegment(sketch, "E416", {"start": v(-7.05, -5.93) * mm, "end": v(-7.08, -6.16) * mm});
            skLineSegment(sketch, "E417", {"start": v(-7.08, -6.16) * mm, "end": v(-7.1, -6.36) * mm});
            skLineSegment(sketch, "E418", {"start": v(-7.1, -6.36) * mm, "end": v(-7.1, -6.43) * mm});
            skLineSegment(sketch, "E419", {"start": v(-7.1, -6.43) * mm, "end": v(-7.12, -6.54) * mm});
            skLineSegment(sketch, "E420", {"start": v(-7.12, -6.54) * mm, "end": v(-7.15, -6.87) * mm});
            skLineSegment(sketch, "E421", {"start": v(-7.15, -6.87) * mm, "end": v(-7.2, -7.34) * mm});
            skLineSegment(sketch, "E422", {"start": v(-7.2, -7.34) * mm, "end": v(-7.24, -7.83) * mm});
            skLineSegment(sketch, "E423", {"start": v(-7.24, -7.83) * mm, "end": v(-7.28, -8.32) * mm});
            skLineSegment(sketch, "E424", {"start": v(-7.28, -8.32) * mm, "end": v(-7.33, -8.79) * mm});
            skLineSegment(sketch, "E425", {"start": v(-7.33, -8.79) * mm, "end": v(-7.37, -9.2) * mm});
            skLineSegment(sketch, "E426", {"start": v(-7.37, -9.2) * mm, "end": v(-7.4, -9.56) * mm});
            skLineSegment(sketch, "E427", {"start": v(-7.4, -9.56) * mm, "end": v(-7.42, -9.76) * mm});
            skLineSegment(sketch, "E428", {"start": v(-7.42, -9.76) * mm, "end": v(-7.42, -9.82) * mm});
            skLineSegment(sketch, "E429", {"start": v(-7.42, -9.82) * mm, "end": v(-7.43, -9.88) * mm});
            skLineSegment(sketch, "E430", {"start": v(-7.43, -9.88) * mm, "end": v(-7.44, -10.03) * mm});
            skLineSegment(sketch, "E431", {"start": v(-7.44, -10.03) * mm, "end": v(-7.47, -10.25) * mm});
            skLineSegment(sketch, "E432", {"start": v(-7.47, -10.25) * mm, "end": v(-7.48, -10.43) * mm});
            skLineSegment(sketch, "E433", {"start": v(-7.48, -10.43) * mm, "end": v(-7.5, -10.53) * mm});
            skLineSegment(sketch, "E434", {"start": v(-7.5, -10.53) * mm, "end": v(-7.5, -10.56) * mm});
            skLineSegment(sketch, "E435", {"start": v(-7.5, -10.56) * mm, "end": v(-7.5, -10.62) * mm});
            skLineSegment(sketch, "E436", {"start": v(-7.5, -10.62) * mm, "end": v(-7.53, -10.79) * mm});
            skLineSegment(sketch, "E437", {"start": v(-7.53, -10.79) * mm, "end": v(-7.58, -11.04) * mm});
            skLineSegment(sketch, "E438", {"start": v(-7.58, -11.04) * mm, "end": v(-7.64, -11.27) * mm});
            skLineSegment(sketch, "E439", {"start": v(-7.64, -11.27) * mm, "end": v(-7.68, -11.4) * mm});
            skLineSegment(sketch, "E440", {"start": v(-7.68, -11.4) * mm, "end": v(-7.7, -11.43) * mm});
            skLineSegment(sketch, "E441", {"start": v(-7.7, -11.43) * mm, "end": v(-7.72, -11.46) * mm});
            skLineSegment(sketch, "E442", {"start": v(-7.72, -11.46) * mm, "end": v(-7.78, -11.56) * mm});
            skLineSegment(sketch, "E443", {"start": v(-7.78, -11.56) * mm, "end": v(-7.86, -11.66) * mm});
            skLineSegment(sketch, "E444", {"start": v(-7.86, -11.66) * mm, "end": v(-7.95, -11.75) * mm});
            skLineSegment(sketch, "E445", {"start": v(-7.95, -11.75) * mm, "end": v(-8.03, -11.8) * mm});
            skLineSegment(sketch, "E446", {"start": v(-8.03, -11.8) * mm, "end": v(-8.05, -11.8) * mm});
            skLineSegment(sketch, "E447", {"start": v(-8.05, -11.8) * mm, "end": v(-8.08, -11.82) * mm});
            skLineSegment(sketch, "E448", {"start": v(-8.08, -11.82) * mm, "end": v(-8.16, -11.86) * mm});
            skLineSegment(sketch, "E449", {"start": v(-8.16, -11.86) * mm, "end": v(-8.34, -11.94) * mm});
            skLineSegment(sketch, "E450", {"start": v(-8.34, -11.94) * mm, "end": v(-8.56, -12.04) * mm});
            skLineSegment(sketch, "E451", {"start": v(-8.56, -12.04) * mm, "end": v(-8.8, -12.15) * mm});
            skLineSegment(sketch, "E452", {"start": v(-8.8, -12.15) * mm, "end": v(-9.02, -12.25) * mm});
            skLineSegment(sketch, "E453", {"start": v(-9.02, -12.25) * mm, "end": v(-9.22, -12.34) * mm});
            skLineSegment(sketch, "E454", {"start": v(-9.22, -12.34) * mm, "end": v(-9.35, -12.4) * mm});
            skLineSegment(sketch, "E455", {"start": v(-9.35, -12.4) * mm, "end": v(-9.4, -12.42) * mm});
            skLineSegment(sketch, "E456", {"start": v(-9.4, -12.42) * mm, "end": v(-9.41, -12.42) * mm});
            skLineSegment(sketch, "E457", {"start": v(-9.41, -12.42) * mm, "end": v(-9.43, -12.42) * mm});
            skLineSegment(sketch, "E458", {"start": v(-9.43, -12.42) * mm, "end": v(-9.5, -12.46) * mm});
            skLineSegment(sketch, "E459", {"start": v(-9.5, -12.46) * mm, "end": v(-9.7, -12.55) * mm});
            skLineSegment(sketch, "E460", {"start": v(-9.7, -12.55) * mm, "end": v(-9.98, -12.7) * mm});
            skLineSegment(sketch, "E461", {"start": v(-9.98, -12.7) * mm, "end": v(-10.3, -12.86) * mm});
            skLineSegment(sketch, "E462", {"start": v(-10.3, -12.86) * mm, "end": v(-10.65, -13.04) * mm});
            skLineSegment(sketch, "E463", {"start": v(-10.65, -13.04) * mm, "end": v(-10.98, -13.21) * mm});
            skLineSegment(sketch, "E464", {"start": v(-10.98, -13.21) * mm, "end": v(-11.27, -13.36) * mm});
            skLineSegment(sketch, "E465", {"start": v(-11.27, -13.36) * mm, "end": v(-11.42, -13.45) * mm});
            skLineSegment(sketch, "E466", {"start": v(-11.42, -13.45) * mm, "end": v(-11.47, -13.48) * mm});
            skLineSegment(sketch, "E467", {"start": v(-11.47, -13.48) * mm, "end": v(-11.54, -13.52) * mm});
            skLineSegment(sketch, "E468", {"start": v(-11.54, -13.52) * mm, "end": v(-11.73, -13.63) * mm});
            skLineSegment(sketch, "E469", {"start": v(-11.73, -13.63) * mm, "end": v(-12.04, -13.82) * mm});
            skLineSegment(sketch, "E470", {"start": v(-12.04, -13.82) * mm, "end": v(-12.36, -14) * mm});
            skLineSegment(sketch, "E471", {"start": v(-12.36, -14) * mm, "end": v(-12.6, -14.14) * mm});
            skLineSegment(sketch, "E472", {"start": v(-12.6, -14.14) * mm, "end": v(-12.67, -14.19) * mm});
            skLineSegment(sketch, "E473", {"start": v(-12.67, -14.19) * mm, "end": v(-12.74, -14.23) * mm});
            skLineSegment(sketch, "E474", {"start": v(-12.74, -14.23) * mm, "end": v(-12.96, -14.36) * mm});
            skLineSegment(sketch, "E475", {"start": v(-12.96, -14.36) * mm, "end": v(-13.28, -14.55) * mm});
            skLineSegment(sketch, "E476", {"start": v(-13.28, -14.55) * mm, "end": v(-13.57, -14.72) * mm});
            skLineSegment(sketch, "E477", {"start": v(-13.57, -14.72) * mm, "end": v(-13.75, -14.82) * mm});
            skLineSegment(sketch, "E478", {"start": v(-13.75, -14.82) * mm, "end": v(-13.8, -14.86) * mm});
            skLineSegment(sketch, "E479", {"start": v(-13.8, -14.86) * mm, "end": v(-13.86, -14.9) * mm});
            skLineSegment(sketch, "E480", {"start": v(-13.86, -14.9) * mm, "end": v(-14.04, -15) * mm});
            skLineSegment(sketch, "E481", {"start": v(-14.04, -15) * mm, "end": v(-14.32, -15.16) * mm});
            skLineSegment(sketch, "E482", {"start": v(-14.32, -15.16) * mm, "end": v(-14.62, -15.34) * mm});
            skLineSegment(sketch, "E483", {"start": v(-14.62, -15.34) * mm, "end": v(-14.83, -15.46) * mm});
            skLineSegment(sketch, "E484", {"start": v(-14.83, -15.46) * mm, "end": v(-14.9, -15.5) * mm});
            skLineSegment(sketch, "E485", {"start": v(-14.9, -15.5) * mm, "end": v(-14.97, -15.54) * mm});
            skLineSegment(sketch, "E486", {"start": v(-14.97, -15.54) * mm, "end": v(-15.17, -15.66) * mm});
            skLineSegment(sketch, "E487", {"start": v(-15.17, -15.66) * mm, "end": v(-15.47, -15.83) * mm});
            skLineSegment(sketch, "E488", {"start": v(-15.47, -15.83) * mm, "end": v(-15.74, -15.99) * mm});
            skLineSegment(sketch, "E489", {"start": v(-15.74, -15.99) * mm, "end": v(-15.9, -16.08) * mm});
            skLineSegment(sketch, "E490", {"start": v(-15.9, -16.08) * mm, "end": v(-15.96, -16.11) * mm});
            skLineSegment(sketch, "E491", {"start": v(-15.96, -16.11) * mm, "end": v(-16.05, -16.17) * mm});
            skLineSegment(sketch, "E492", {"start": v(-16.05, -16.17) * mm, "end": v(-16.32, -16.33) * mm});
            skLineSegment(sketch, "E493", {"start": v(-16.32, -16.33) * mm, "end": v(-16.63, -16.51) * mm});
            skLineSegment(sketch, "E494", {"start": v(-16.63, -16.51) * mm, "end": v(-16.88, -16.66) * mm});
            skLineSegment(sketch, "E495", {"start": v(-16.88, -16.66) * mm, "end": v(-17.1, -16.78) * mm});
            skLineSegment(sketch, "E496", {"start": v(-17.1, -16.78) * mm, "end": v(-17.26, -16.88) * mm});
            skLineSegment(sketch, "E497", {"start": v(-17.26, -16.88) * mm, "end": v(-17.37, -16.94) * mm});
            skLineSegment(sketch, "E498", {"start": v(-17.37, -16.94) * mm, "end": v(-17.44, -16.98) * mm});
            skLineSegment(sketch, "E499", {"start": v(-17.44, -16.98) * mm, "end": v(-17.46, -16.99) * mm});
            skLineSegment(sketch, "E500", {"start": v(-17.46, -16.99) * mm, "end": v(-17.47, -16.99) * mm});
            skLineSegment(sketch, "E501", {"start": v(-17.47, -16.99) * mm, "end": v(-17.47, -16.99) * mm});
            skLineSegment(sketch, "E502", {"start": v(-17.47, -16.99) * mm, "end": v(-17.49, -16.94) * mm});
            skLineSegment(sketch, "E503", {"start": v(-17.49, -16.94) * mm, "end": v(-17.54, -16.82) * mm});
            skLineSegment(sketch, "E504", {"start": v(-17.54, -16.82) * mm, "end": v(-17.62, -16.66) * mm});
            skLineSegment(sketch, "E505", {"start": v(-17.62, -16.66) * mm, "end": v(-17.69, -16.5) * mm});
            skLineSegment(sketch, "E506", {"start": v(-17.69, -16.5) * mm, "end": v(-17.7, -16.45) * mm});
            skLineSegment(sketch, "E507", {"start": v(-17.7, -16.45) * mm, "end": v(-17.74, -16.4) * mm});
            skLineSegment(sketch, "E508", {"start": v(-17.74, -16.4) * mm, "end": v(-17.82, -16.2) * mm});
            skLineSegment(sketch, "E509", {"start": v(-17.82, -16.2) * mm, "end": v(-17.95, -15.92) * mm});
            skLineSegment(sketch, "E510", {"start": v(-17.95, -15.92) * mm, "end": v(-18.09, -15.62) * mm});
            skLineSegment(sketch, "E511", {"start": v(-18.09, -15.62) * mm, "end": v(-18.18, -15.42) * mm});
            skLineSegment(sketch, "E512", {"start": v(-18.18, -15.42) * mm, "end": v(-18.2, -15.35) * mm});
            skLineSegment(sketch, "E513", {"start": v(-18.2, -15.35) * mm, "end": v(-18.47, -14.77) * mm});
            skLineSegment(sketch, "E514", {"start": v(-18.47, -14.77) * mm, "end": v(-18.33, -14.65) * mm});
            skLineSegment(sketch, "E515", {"start": v(-18.33, -14.65) * mm, "end": v(-18.32, -14.64) * mm});
            skLineSegment(sketch, "E516", {"start": v(-18.32, -14.64) * mm, "end": v(-18.28, -14.6) * mm});
            skLineSegment(sketch, "E517", {"start": v(-18.28, -14.6) * mm, "end": v(-18.23, -14.56) * mm});
            skLineSegment(sketch, "E518", {"start": v(-18.23, -14.56) * mm, "end": v(-18.2, -14.52) * mm});
            skLineSegment(sketch, "E519", {"start": v(-18.2, -14.52) * mm, "end": v(-18.19, -14.5) * mm});
            skLineSegment(sketch, "E520", {"start": v(-18.19, -14.5) * mm, "end": v(-18.19, -14.5) * mm});
            skLineSegment(sketch, "E521", {"start": v(-18.19, -14.5) * mm, "end": v(-18.22, -14.48) * mm});
            skLineSegment(sketch, "E522", {"start": v(-18.22, -14.48) * mm, "end": v(-18.28, -14.48) * mm});
            skLineSegment(sketch, "E523", {"start": v(-18.28, -14.48) * mm, "end": v(-18.37, -14.5) * mm});
            skLineSegment(sketch, "E524", {"start": v(-18.37, -14.5) * mm, "end": v(-18.45, -14.51) * mm});
            skLineSegment(sketch, "E525", {"start": v(-18.45, -14.51) * mm, "end": v(-18.48, -14.52) * mm});
            skLineSegment(sketch, "E526", {"start": v(-18.48, -14.52) * mm, "end": v(-18.49, -14.53) * mm});
            skLineSegment(sketch, "E527", {"start": v(-18.49, -14.53) * mm, "end": v(-18.52, -14.53) * mm});
            skLineSegment(sketch, "E528", {"start": v(-18.52, -14.53) * mm, "end": v(-18.56, -14.5) * mm});
            skLineSegment(sketch, "E529", {"start": v(-18.56, -14.5) * mm, "end": v(-18.6, -14.43) * mm});
            skLineSegment(sketch, "E530", {"start": v(-18.6, -14.43) * mm, "end": v(-18.66, -14.34) * mm});
            skLineSegment(sketch, "E531", {"start": v(-18.66, -14.34) * mm, "end": v(-18.67, -14.3) * mm});
            skLineSegment(sketch, "E532", {"start": v(-18.67, -14.3) * mm, "end": v(-18.8, -14.07) * mm});
            skLineSegment(sketch, "E533", {"start": v(-18.8, -14.07) * mm, "end": v(-18.98, -14.15) * mm});
            skLineSegment(sketch, "E534", {"start": v(-18.98, -14.15) * mm, "end": v(-19, -14.16) * mm});
            skLineSegment(sketch, "E535", {"start": v(-19, -14.16) * mm, "end": v(-19.06, -14.19) * mm});
            skLineSegment(sketch, "E536", {"start": v(-19.06, -14.19) * mm, "end": v(-19.12, -14.2) * mm});
            skLineSegment(sketch, "E537", {"start": v(-19.12, -14.2) * mm, "end": v(-19.16, -14.21) * mm});
            skLineSegment(sketch, "E538", {"start": v(-19.16, -14.21) * mm, "end": v(-19.18, -14.2) * mm});
            skLineSegment(sketch, "E539", {"start": v(-19.18, -14.2) * mm, "end": v(-19.18, -14.2) * mm});
            skLineSegment(sketch, "E540", {"start": v(-19.18, -14.2) * mm, "end": v(-19.19, -14.19) * mm});
            skLineSegment(sketch, "E541", {"start": v(-19.19, -14.19) * mm, "end": v(-19.2, -14.15) * mm});
            skLineSegment(sketch, "E542", {"start": v(-19.2, -14.15) * mm, "end": v(-19.24, -14.04) * mm});
            skLineSegment(sketch, "E543", {"start": v(-19.24, -14.04) * mm, "end": v(-19.3, -13.89) * mm});
            skLineSegment(sketch, "E544", {"start": v(-19.3, -13.89) * mm, "end": v(-19.35, -13.72) * mm});
            skLineSegment(sketch, "E545", {"start": v(-19.35, -13.72) * mm, "end": v(-19.4, -13.55) * mm});
            skLineSegment(sketch, "E546", {"start": v(-19.4, -13.55) * mm, "end": v(-19.45, -13.4) * mm});
            skLineSegment(sketch, "E547", {"start": v(-19.45, -13.4) * mm, "end": v(-19.49, -13.3) * mm});
            skLineSegment(sketch, "E548", {"start": v(-19.49, -13.3) * mm, "end": v(-19.5, -13.26) * mm});
            skLineSegment(sketch, "E549", {"start": v(-19.5, -13.26) * mm, "end": v(-19.5, -13.24) * mm});
            skLineSegment(sketch, "E550", {"start": v(-19.5, -13.24) * mm, "end": v(-19.5, -13.24) * mm});
            skLineSegment(sketch, "E551", {"start": v(-19.5, -13.24) * mm, "end": v(-19.49, -13.22) * mm});
            skLineSegment(sketch, "E552", {"start": v(-19.49, -13.22) * mm, "end": v(-19.45, -13.2) * mm});
            skLineSegment(sketch, "E553", {"start": v(-19.45, -13.2) * mm, "end": v(-19.4, -13.17) * mm});
            skLineSegment(sketch, "E554", {"start": v(-19.4, -13.17) * mm, "end": v(-19.36, -13.15) * mm});
            skLineSegment(sketch, "E555", {"start": v(-19.36, -13.15) * mm, "end": v(-19.34, -13.15) * mm});
            skLineSegment(sketch, "E556", {"start": v(-19.34, -13.15) * mm, "end": v(-19.32, -13.14) * mm});
            skLineSegment(sketch, "E557", {"start": v(-19.32, -13.14) * mm, "end": v(-19.26, -13.11) * mm});
            skLineSegment(sketch, "E558", {"start": v(-19.26, -13.11) * mm, "end": v(-19.22, -13.08) * mm});
            skLineSegment(sketch, "E559", {"start": v(-19.22, -13.08) * mm, "end": v(-19.2, -13.05) * mm});
            skLineSegment(sketch, "E560", {"start": v(-19.2, -13.05) * mm, "end": v(-19.2, -13.02) * mm});
            skLineSegment(sketch, "E561", {"start": v(-19.2, -13.02) * mm, "end": v(-19.21, -13) * mm});
            skLineSegment(sketch, "E562", {"start": v(-19.21, -13) * mm, "end": v(-19.21, -13) * mm});
            skLineSegment(sketch, "E563", {"start": v(-19.21, -13) * mm, "end": v(-19.23, -12.92) * mm});
            skLineSegment(sketch, "E564", {"start": v(-19.23, -12.92) * mm, "end": v(-19.27, -12.75) * mm});
            skLineSegment(sketch, "E565", {"start": v(-19.27, -12.75) * mm, "end": v(-19.32, -12.52) * mm});
            skLineSegment(sketch, "E566", {"start": v(-19.32, -12.52) * mm, "end": v(-19.37, -12.32) * mm});
            skLineSegment(sketch, "E567", {"start": v(-19.37, -12.32) * mm, "end": v(-19.38, -12.26) * mm});
            skLineSegment(sketch, "E568", {"start": v(-19.38, -12.26) * mm, "end": v(-19.54, -11.58) * mm});
            skLineSegment(sketch, "E569", {"start": v(-19.54, -11.58) * mm, "end": v(-19.44, -11.43) * mm});
            skLineSegment(sketch, "E570", {"start": v(-19.44, -11.43) * mm, "end": v(-19.42, -11.41) * mm});
            skLineSegment(sketch, "E571", {"start": v(-19.42, -11.41) * mm, "end": v(-19.4, -11.36) * mm});
            skLineSegment(sketch, "E572", {"start": v(-19.4, -11.36) * mm, "end": v(-19.36, -11.3) * mm});
            skLineSegment(sketch, "E573", {"start": v(-19.36, -11.3) * mm, "end": v(-19.34, -11.25) * mm});
            skLineSegment(sketch, "E574", {"start": v(-19.34, -11.25) * mm, "end": v(-19.33, -11.22) * mm});
            skLineSegment(sketch, "E575", {"start": v(-19.33, -11.22) * mm, "end": v(-19.33, -11.21) * mm});
            skLineSegment(sketch, "E576", {"start": v(-19.33, -11.21) * mm, "end": v(-19.33, -11.2) * mm});
            skLineSegment(sketch, "E577", {"start": v(-19.33, -11.2) * mm, "end": v(-19.35, -11.16) * mm});
            skLineSegment(sketch, "E578", {"start": v(-19.35, -11.16) * mm, "end": v(-19.38, -11.14) * mm});
            skLineSegment(sketch, "E579", {"start": v(-19.38, -11.14) * mm, "end": v(-19.44, -11.13) * mm});
            skLineSegment(sketch, "E580", {"start": v(-19.44, -11.13) * mm, "end": v(-19.5, -11.14) * mm});
            skLineSegment(sketch, "E581", {"start": v(-19.5, -11.14) * mm, "end": v(-19.52, -11.15) * mm});
            skLineSegment(sketch, "E582", {"start": v(-19.52, -11.15) * mm, "end": v(-19.53, -11.16) * mm});
            skLineSegment(sketch, "E583", {"start": v(-19.53, -11.16) * mm, "end": v(-19.59, -11.17) * mm});
            skLineSegment(sketch, "E584", {"start": v(-19.59, -11.17) * mm, "end": v(-19.62, -11.17) * mm});
            skLineSegment(sketch, "E585", {"start": v(-19.62, -11.17) * mm, "end": v(-19.63, -11.17) * mm});
            skLineSegment(sketch, "E586", {"start": v(-19.63, -11.17) * mm, "end": v(-19.63, -11.17) * mm});
            skLineSegment(sketch, "E587", {"start": v(-19.63, -11.17) * mm, "end": v(-19.64, -11.13) * mm});
            skLineSegment(sketch, "E588", {"start": v(-19.64, -11.13) * mm, "end": v(-19.66, -11.05) * mm});
            skLineSegment(sketch, "E589", {"start": v(-19.66, -11.05) * mm, "end": v(-19.69, -10.94) * mm});
            skLineSegment(sketch, "E590", {"start": v(-19.69, -10.94) * mm, "end": v(-19.71, -10.84) * mm});
            skLineSegment(sketch, "E591", {"start": v(-19.71, -10.84) * mm, "end": v(-19.72, -10.8) * mm});
            skLineSegment(sketch, "E592", {"start": v(-19.72, -10.8) * mm, "end": v(-19.73, -10.76) * mm});
            skLineSegment(sketch, "E593", {"start": v(-19.73, -10.76) * mm, "end": v(-19.76, -10.64) * mm});
            skLineSegment(sketch, "E594", {"start": v(-19.76, -10.64) * mm, "end": v(-19.8, -10.44) * mm});
            skLineSegment(sketch, "E595", {"start": v(-19.8, -10.44) * mm, "end": v(-19.85, -10.23) * mm});
            skLineSegment(sketch, "E596", {"start": v(-19.85, -10.23) * mm, "end": v(-19.89, -10.09) * mm});
            skLineSegment(sketch, "E597", {"start": v(-19.89, -10.09) * mm, "end": v(-19.9, -10.04) * mm});
            skLineSegment(sketch, "E598", {"start": v(-19.9, -10.04) * mm, "end": v(-19.9, -10) * mm});
            skLineSegment(sketch, "E599", {"start": v(-19.9, -10) * mm, "end": v(-19.94, -9.85) * mm});
            skLineSegment(sketch, "E600", {"start": v(-19.94, -9.85) * mm, "end": v(-20, -9.63) * mm});
            skLineSegment(sketch, "E601", {"start": v(-20, -9.63) * mm, "end": v(-20.04, -9.41) * mm});
            skLineSegment(sketch, "E602", {"start": v(-20.04, -9.41) * mm, "end": v(-20.08, -9.27) * mm});
            skLineSegment(sketch, "E603", {"start": v(-20.08, -9.27) * mm, "end": v(-20.09, -9.22) * mm});
            skLineSegment(sketch, "E604", {"start": v(-20.09, -9.22) * mm, "end": v(-20.18, -8.83) * mm});
            skLineSegment(sketch, "E605", {"start": v(-20.18, -8.83) * mm, "end": v(-20.07, -8.69) * mm});
            skLineSegment(sketch, "E606", {"start": v(-20.07, -8.69) * mm, "end": v(-20.06, -8.68) * mm});
            skLineSegment(sketch, "E607", {"start": v(-20.06, -8.68) * mm, "end": v(-20.03, -8.63) * mm});
            skLineSegment(sketch, "E608", {"start": v(-20.03, -8.63) * mm, "end": v(-20, -8.56) * mm});
            skLineSegment(sketch, "E609", {"start": v(-20, -8.56) * mm, "end": v(-19.98, -8.5) * mm});
            skLineSegment(sketch, "E610", {"start": v(-19.98, -8.5) * mm, "end": v(-19.97, -8.47) * mm});
            skLineSegment(sketch, "E611", {"start": v(-19.97, -8.47) * mm, "end": v(-19.97, -8.45) * mm});
            skLineSegment(sketch, "E612", {"start": v(-19.97, -8.45) * mm, "end": v(-19.97, -8.44) * mm});
            skLineSegment(sketch, "E613", {"start": v(-19.97, -8.44) * mm, "end": v(-19.98, -8.4) * mm});
            skLineSegment(sketch, "E614", {"start": v(-19.98, -8.4) * mm, "end": v(-20, -8.36) * mm});
            skLineSegment(sketch, "E615", {"start": v(-20, -8.36) * mm, "end": v(-20.08, -8.35) * mm});
            skLineSegment(sketch, "E616", {"start": v(-20.08, -8.35) * mm, "end": v(-20.17, -8.36) * mm});
            skLineSegment(sketch, "E617", {"start": v(-20.17, -8.36) * mm, "end": v(-20.2, -8.36) * mm});
            skLineSegment(sketch, "E618", {"start": v(-20.2, -8.36) * mm, "end": v(-20.2, -8.36) * mm});
            skLineSegment(sketch, "E619", {"start": v(-20.2, -8.36) * mm, "end": v(-20.25, -8.35) * mm});
            skLineSegment(sketch, "E620", {"start": v(-20.25, -8.35) * mm, "end": v(-20.28, -8.31) * mm});
            skLineSegment(sketch, "E621", {"start": v(-20.28, -8.31) * mm, "end": v(-20.28, -8.3) * mm});
            skLineSegment(sketch, "E622", {"start": v(-20.28, -8.3) * mm, "end": v(-20.29, -8.29) * mm});
            skLineSegment(sketch, "E623", {"start": v(-20.29, -8.29) * mm, "end": v(-20.3, -8.24) * mm});
            skLineSegment(sketch, "E624", {"start": v(-20.3, -8.24) * mm, "end": v(-20.33, -8.13) * mm});
            skLineSegment(sketch, "E625", {"start": v(-20.33, -8.13) * mm, "end": v(-20.36, -7.99) * mm});
            skLineSegment(sketch, "E626", {"start": v(-20.36, -7.99) * mm, "end": v(-20.4, -7.82) * mm});
            skLineSegment(sketch, "E627", {"start": v(-20.4, -7.82) * mm, "end": v(-20.44, -7.65) * mm});
            skLineSegment(sketch, "E628", {"start": v(-20.44, -7.65) * mm, "end": v(-20.48, -7.5) * mm});
            skLineSegment(sketch, "E629", {"start": v(-20.48, -7.5) * mm, "end": v(-20.5, -7.37) * mm});
            skLineSegment(sketch, "E630", {"start": v(-20.5, -7.37) * mm, "end": v(-20.52, -7.31) * mm});
            skLineSegment(sketch, "E631", {"start": v(-20.52, -7.31) * mm, "end": v(-20.52, -7.3) * mm});
            skLineSegment(sketch, "E632", {"start": v(-20.52, -7.3) * mm, "end": v(-20.53, -7.28) * mm});
            skLineSegment(sketch, "E633", {"start": v(-20.53, -7.28) * mm, "end": v(-20.54, -7.24) * mm});
            skLineSegment(sketch, "E634", {"start": v(-20.54, -7.24) * mm, "end": v(-20.56, -7.2) * mm});
            skLineSegment(sketch, "E635", {"start": v(-20.56, -7.2) * mm, "end": v(-20.6, -7.19) * mm});
            skLineSegment(sketch, "E636", {"start": v(-20.6, -7.19) * mm, "end": v(-20.66, -7.19) * mm});
            skLineSegment(sketch, "E637", {"start": v(-20.66, -7.19) * mm, "end": v(-20.68, -7.19) * mm});
            skLineSegment(sketch, "E638", {"start": v(-20.68, -7.19) * mm, "end": v(-20.7, -7.19) * mm});
            skLineSegment(sketch, "E639", {"start": v(-20.7, -7.19) * mm, "end": v(-20.77, -7.17) * mm});
            skLineSegment(sketch, "E640", {"start": v(-20.77, -7.17) * mm, "end": v(-20.8, -7.15) * mm});
            skLineSegment(sketch, "E641", {"start": v(-20.8, -7.15) * mm, "end": v(-20.8, -7.14) * mm});
            skLineSegment(sketch, "E642", {"start": v(-20.8, -7.14) * mm, "end": v(-20.8, -7.13) * mm});
            skLineSegment(sketch, "E643", {"start": v(-20.8, -7.13) * mm, "end": v(-20.82, -7.08) * mm});
            skLineSegment(sketch, "E644", {"start": v(-20.82, -7.08) * mm, "end": v(-20.83, -6.94) * mm});
            skLineSegment(sketch, "E645", {"start": v(-20.83, -6.94) * mm, "end": v(-20.86, -6.74) * mm});
            skLineSegment(sketch, "E646", {"start": v(-20.86, -6.74) * mm, "end": v(-20.89, -6.57) * mm});
            skLineSegment(sketch, "E647", {"start": v(-20.89, -6.57) * mm, "end": v(-20.9, -6.51) * mm});
            skLineSegment(sketch, "E648", {"start": v(-20.9, -6.51) * mm, "end": v(-20.9, -6.44) * mm});
            skLineSegment(sketch, "E649", {"start": v(-20.9, -6.44) * mm, "end": v(-20.94, -6.23) * mm});
            skLineSegment(sketch, "E650", {"start": v(-20.94, -6.23) * mm, "end": v(-20.98, -5.9) * mm});
            skLineSegment(sketch, "E651", {"start": v(-20.98, -5.9) * mm, "end": v(-21.03, -5.57) * mm});
            skLineSegment(sketch, "E652", {"start": v(-21.03, -5.57) * mm, "end": v(-21.07, -5.35) * mm});
            skLineSegment(sketch, "E653", {"start": v(-21.07, -5.35) * mm, "end": v(-21.08, -5.27) * mm});
            skLineSegment(sketch, "E654", {"start": v(-21.08, -5.27) * mm, "end": v(-21.1, -5.14) * mm});
            skLineSegment(sketch, "E655", {"start": v(-21.1, -5.14) * mm, "end": v(-21.15, -4.74) * mm});
            skLineSegment(sketch, "E656", {"start": v(-21.15, -4.74) * mm, "end": v(-21.22, -4.32) * mm});
            skLineSegment(sketch, "E657", {"start": v(-21.22, -4.32) * mm, "end": v(-21.27, -4) * mm});
            skLineSegment(sketch, "E658", {"start": v(-21.27, -4) * mm, "end": v(-21.3, -3.75) * mm});
            skLineSegment(sketch, "E659", {"start": v(-21.3, -3.75) * mm, "end": v(-21.33, -3.58) * mm});
            skLineSegment(sketch, "E660", {"start": v(-21.33, -3.58) * mm, "end": v(-21.35, -3.47) * mm});
            skLineSegment(sketch, "E661", {"start": v(-21.35, -3.47) * mm, "end": v(-21.36, -3.41) * mm});
            skLineSegment(sketch, "E662", {"start": v(-21.36, -3.41) * mm, "end": v(-21.36, -3.4) * mm});
            skLineSegment(sketch, "E663", {"start": v(-21.36, -3.4) * mm, "end": v(-21.37, -3.4) * mm});
            skLineSegment(sketch, "E664", {"start": v(-21.37, -3.4) * mm, "end": v(-21.37, -3.39) * mm});
            skLineSegment(sketch, "E665", {"start": v(-21.37, -3.39) * mm, "end": v(-21.43, -3.41) * mm});
            skLineSegment(sketch, "E666", {"start": v(-21.43, -3.41) * mm, "end": v(-21.62, -3.5) * mm});
            skLineSegment(sketch, "E667", {"start": v(-21.62, -3.5) * mm, "end": v(-21.92, -3.67) * mm});
            skLineSegment(sketch, "E668", {"start": v(-21.92, -3.67) * mm, "end": v(-22.25, -3.85) * mm});
            skLineSegment(sketch, "E669", {"start": v(-22.25, -3.85) * mm, "end": v(-22.36, -3.91) * mm});
            skLineSegment(sketch, "E670", {"start": v(-22.36, -3.91) * mm, "end": v(-22.84, -4.18) * mm});
            skLineSegment(sketch, "E671", {"start": v(-22.84, -4.18) * mm, "end": v(-22.9, -5.09) * mm});
            skLineSegment(sketch, "E672", {"start": v(-22.9, -5.09) * mm, "end": v(-22.9, -5.18) * mm});
            skLineSegment(sketch, "E673", {"start": v(-22.9, -5.18) * mm, "end": v(-22.92, -5.47) * mm});
            skLineSegment(sketch, "E674", {"start": v(-22.92, -5.47) * mm, "end": v(-22.94, -5.86) * mm});
            skLineSegment(sketch, "E675", {"start": v(-22.94, -5.86) * mm, "end": v(-22.96, -6.19) * mm});
            skLineSegment(sketch, "E676", {"start": v(-22.96, -6.19) * mm, "end": v(-22.97, -6.37) * mm});
            skLineSegment(sketch, "E677", {"start": v(-22.97, -6.37) * mm, "end": v(-22.97, -6.43) * mm});
            skLineSegment(sketch, "E678", {"start": v(-22.97, -6.43) * mm, "end": v(-22.98, -6.54) * mm});
            skLineSegment(sketch, "E679", {"start": v(-22.98, -6.54) * mm, "end": v(-23, -6.85) * mm});
            skLineSegment(sketch, "E680", {"start": v(-23, -6.85) * mm, "end": v(-23.02, -7.35) * mm});
            skLineSegment(sketch, "E681", {"start": v(-23.02, -7.35) * mm, "end": v(-23.05, -7.84) * mm});
            skLineSegment(sketch, "E682", {"start": v(-23.05, -7.84) * mm, "end": v(-23.07, -8.13) * mm});
            skLineSegment(sketch, "E683", {"start": v(-23.07, -8.13) * mm, "end": v(-23.08, -8.23) * mm});
            skLineSegment(sketch, "E684", {"start": v(-23.08, -8.23) * mm, "end": v(-23.08, -8.26) * mm});
            skLineSegment(sketch, "E685", {"start": v(-23.08, -8.26) * mm, "end": v(-23.1, -8.5) * mm});
            skLineSegment(sketch, "E686", {"start": v(-23.1, -8.5) * mm, "end": v(-23.1, -8.75) * mm});
            skLineSegment(sketch, "E687", {"start": v(-23.1, -8.75) * mm, "end": v(-23.1, -8.8) * mm});
            skLineSegment(sketch, "E688", {"start": v(-23.1, -8.8) * mm, "end": v(-23.11, -8.9) * mm});
            skLineSegment(sketch, "E689", {"start": v(-23.11, -8.9) * mm, "end": v(-23.13, -9.23) * mm});
            skLineSegment(sketch, "E690", {"start": v(-23.13, -9.23) * mm, "end": v(-23.15, -9.63) * mm});
            skLineSegment(sketch, "E691", {"start": v(-23.15, -9.63) * mm, "end": v(-23.18, -10.07) * mm});
            skLineSegment(sketch, "E692", {"start": v(-23.18, -10.07) * mm, "end": v(-23.2, -10.5) * mm});
            skLineSegment(sketch, "E693", {"start": v(-23.2, -10.5) * mm, "end": v(-23.2, -10.64) * mm});
            skLineSegment(sketch, "E694", {"start": v(-23.2, -10.64) * mm, "end": v(-23.21, -10.74) * mm});
            skLineSegment(sketch, "E695", {"start": v(-23.21, -10.74) * mm, "end": v(-23.23, -11.02) * mm});
            skLineSegment(sketch, "E696", {"start": v(-23.23, -11.02) * mm, "end": v(-23.25, -11.32) * mm});
            skLineSegment(sketch, "E697", {"start": v(-23.25, -11.32) * mm, "end": v(-23.26, -11.6) * mm});
            skLineSegment(sketch, "E698", {"start": v(-23.26, -11.6) * mm, "end": v(-23.28, -11.86) * mm});
            skLineSegment(sketch, "E699", {"start": v(-23.28, -11.86) * mm, "end": v(-23.3, -12.16) * mm});
            skLineSegment(sketch, "E700", {"start": v(-23.3, -12.16) * mm, "end": v(-23.32, -12.53) * mm});
            skLineSegment(sketch, "E701", {"start": v(-23.32, -12.53) * mm, "end": v(-23.34, -13.02) * mm});
            skLineSegment(sketch, "E702", {"start": v(-23.34, -13.02) * mm, "end": v(-23.37, -13.5) * mm});
            skLineSegment(sketch, "E703", {"start": v(-23.37, -13.5) * mm, "end": v(-23.38, -13.65) * mm});
            skLineSegment(sketch, "E704", {"start": v(-23.38, -13.65) * mm, "end": v(-23.38, -13.73) * mm});
            skLineSegment(sketch, "E705", {"start": v(-23.38, -13.73) * mm, "end": v(-23.4, -13.97) * mm});
            skLineSegment(sketch, "E706", {"start": v(-23.4, -13.97) * mm, "end": v(-23.41, -14.28) * mm});
            skLineSegment(sketch, "E707", {"start": v(-23.41, -14.28) * mm, "end": v(-23.43, -14.55) * mm});
            skLineSegment(sketch, "E708", {"start": v(-23.43, -14.55) * mm, "end": v(-23.45, -14.8) * mm});
            skLineSegment(sketch, "E709", {"start": v(-23.45, -14.8) * mm, "end": v(-23.46, -15) * mm});
            skLineSegment(sketch, "E710", {"start": v(-23.46, -15) * mm, "end": v(-23.48, -15.15) * mm});
            skLineSegment(sketch, "E711", {"start": v(-23.48, -15.15) * mm, "end": v(-23.48, -15.25) * mm});
            skLineSegment(sketch, "E712", {"start": v(-23.48, -15.25) * mm, "end": v(-23.49, -15.28) * mm});
            skLineSegment(sketch, "E713", {"start": v(-23.49, -15.28) * mm, "end": v(-23.5, -15.28) * mm});
            skLineSegment(sketch, "E714", {"start": v(-23.5, -15.28) * mm, "end": v(-23.5, -15.29) * mm});
            skLineSegment(sketch, "E715", {"start": v(-23.5, -15.29) * mm, "end": v(-23.54, -15.32) * mm});
            skLineSegment(sketch, "E716", {"start": v(-23.54, -15.32) * mm, "end": v(-23.67, -15.39) * mm});
            skLineSegment(sketch, "E717", {"start": v(-23.67, -15.39) * mm, "end": v(-23.86, -15.5) * mm});
            skLineSegment(sketch, "E718", {"start": v(-23.86, -15.5) * mm, "end": v(-24.03, -15.58) * mm});
            skLineSegment(sketch, "E719", {"start": v(-24.03, -15.58) * mm, "end": v(-24.08, -15.61) * mm});
            skLineSegment(sketch, "E720", {"start": v(-24.08, -15.61) * mm, "end": v(-24.25, -15.7) * mm});
            skLineSegment(sketch, "E721", {"start": v(-24.25, -15.7) * mm, "end": v(-24.76, -15.98) * mm});
            skLineSegment(sketch, "E722", {"start": v(-24.76, -15.98) * mm, "end": v(-25.29, -16.3) * mm});
            skLineSegment(sketch, "E723", {"start": v(-25.29, -16.3) * mm, "end": v(-25.67, -16.53) * mm});
            skLineSegment(sketch, "E724", {"start": v(-25.67, -16.53) * mm, "end": v(-25.84, -16.65) * mm});
            skLineSegment(sketch, "E725", {"start": v(-25.84, -16.65) * mm, "end": v(-25.89, -16.69) * mm});
            skLineSegment(sketch, "E726", {"start": v(-25.89, -16.69) * mm, "end": v(-25.9, -16.7) * mm});
            skLineSegment(sketch, "E727", {"start": v(-25.9, -16.7) * mm, "end": v(-25.98, -16.78) * mm});
            skLineSegment(sketch, "E728", {"start": v(-25.98, -16.78) * mm, "end": v(-26.03, -16.84) * mm});
            skLineSegment(sketch, "E729", {"start": v(-26.03, -16.84) * mm, "end": v(-26.06, -16.92) * mm});
            skLineSegment(sketch, "E730", {"start": v(-26.06, -16.92) * mm, "end": v(-26.07, -16.99) * mm});
            skLineSegment(sketch, "E731", {"start": v(-26.07, -16.99) * mm, "end": v(-26.07, -17.01) * mm});
            skLineSegment(sketch, "E732", {"start": v(-26.07, -17.01) * mm, "end": v(-26.07, -17.03) * mm});
            skLineSegment(sketch, "E733", {"start": v(-26.07, -17.03) * mm, "end": v(-26.08, -17.07) * mm});
            skLineSegment(sketch, "E734", {"start": v(-26.08, -17.07) * mm, "end": v(-26.08, -17.12) * mm});
            skLineSegment(sketch, "E735", {"start": v(-26.08, -17.12) * mm, "end": v(-26.07, -17.16) * mm});
            skLineSegment(sketch, "E736", {"start": v(-26.07, -17.16) * mm, "end": v(-26.06, -17.21) * mm});
            skLineSegment(sketch, "E737", {"start": v(-26.06, -17.21) * mm, "end": v(-26.04, -17.26) * mm});
            skLineSegment(sketch, "E738", {"start": v(-26.04, -17.26) * mm, "end": v(-26.01, -17.33) * mm});
            skLineSegment(sketch, "E739", {"start": v(-26.01, -17.33) * mm, "end": v(-25.98, -17.4) * mm});
            skLineSegment(sketch, "E740", {"start": v(-25.98, -17.4) * mm, "end": v(-25.94, -17.48) * mm});
            skLineSegment(sketch, "E741", {"start": v(-25.94, -17.48) * mm, "end": v(-25.93, -17.5) * mm});
            skLineSegment(sketch, "E742", {"start": v(-25.93, -17.5) * mm, "end": v(-25.89, -17.58) * mm});
            skLineSegment(sketch, "E743", {"start": v(-25.89, -17.58) * mm, "end": v(-25.75, -17.82) * mm});
            skLineSegment(sketch, "E744", {"start": v(-25.75, -17.82) * mm, "end": v(-25.6, -18.03) * mm});
            skLineSegment(sketch, "E745", {"start": v(-25.6, -18.03) * mm, "end": v(-25.44, -18.13) * mm});
            skLineSegment(sketch, "E746", {"start": v(-25.44, -18.13) * mm, "end": v(-25.3, -18.17) * mm});
            skLineSegment(sketch, "E747", {"start": v(-25.3, -18.17) * mm, "end": v(-25.26, -18.17) * mm});
            skLineSegment(sketch, "E748", {"start": v(-25.26, -18.17) * mm, "end": v(-25.25, -18.17) * mm});
            skLineSegment(sketch, "E749", {"start": v(-25.25, -18.17) * mm, "end": v(-25.2, -18.16) * mm});
            skLineSegment(sketch, "E750", {"start": v(-25.2, -18.16) * mm, "end": v(-25.11, -18.14) * mm});
            skLineSegment(sketch, "E751", {"start": v(-25.11, -18.14) * mm, "end": v(-25.01, -18.1) * mm});
            skLineSegment(sketch, "E752", {"start": v(-25.01, -18.1) * mm, "end": v(-24.88, -18.03) * mm});
            skLineSegment(sketch, "E753", {"start": v(-24.88, -18.03) * mm, "end": v(-24.72, -17.95) * mm});
            skLineSegment(sketch, "E754", {"start": v(-24.72, -17.95) * mm, "end": v(-24.52, -17.83) * mm});
            skLineSegment(sketch, "E755", {"start": v(-24.52, -17.83) * mm, "end": v(-24.27, -17.68) * mm});
            skLineSegment(sketch, "E756", {"start": v(-24.27, -17.68) * mm, "end": v(-24.04, -17.54) * mm});
            skLineSegment(sketch, "E757", {"start": v(-24.04, -17.54) * mm, "end": v(-23.96, -17.49) * mm});
            skLineSegment(sketch, "E758", {"start": v(-23.96, -17.49) * mm, "end": v(-23.92, -17.46) * mm});
            skLineSegment(sketch, "E759", {"start": v(-23.92, -17.46) * mm, "end": v(-23.8, -17.39) * mm});
            skLineSegment(sketch, "E760", {"start": v(-23.8, -17.39) * mm, "end": v(-23.65, -17.3) * mm});
            skLineSegment(sketch, "E761", {"start": v(-23.65, -17.3) * mm, "end": v(-23.56, -17.25) * mm});
            skLineSegment(sketch, "E762", {"start": v(-23.56, -17.25) * mm, "end": v(-23.52, -17.23) * mm});
            skLineSegment(sketch, "E763", {"start": v(-23.52, -17.23) * mm, "end": v(-23.51, -17.23) * mm});
            skLineSegment(sketch, "E764", {"start": v(-23.51, -17.23) * mm, "end": v(-23.51, -17.23) * mm});
            skLineSegment(sketch, "E765", {"start": v(-23.51, -17.23) * mm, "end": v(-23.5, -17.26) * mm});
            skLineSegment(sketch, "E766", {"start": v(-23.5, -17.26) * mm, "end": v(-23.5, -17.36) * mm});
            skLineSegment(sketch, "E767", {"start": v(-23.5, -17.36) * mm, "end": v(-23.5, -17.5) * mm});
            skLineSegment(sketch, "E768", {"start": v(-23.5, -17.5) * mm, "end": v(-23.5, -17.69) * mm});
            skLineSegment(sketch, "E769", {"start": v(-23.5, -17.69) * mm, "end": v(-23.51, -17.9) * mm});
            skLineSegment(sketch, "E770", {"start": v(-23.51, -17.9) * mm, "end": v(-23.52, -18.1) * mm});
            skLineSegment(sketch, "E771", {"start": v(-23.52, -18.1) * mm, "end": v(-23.53, -18.31) * mm});
            skLineSegment(sketch, "E772", {"start": v(-23.53, -18.31) * mm, "end": v(-23.54, -18.45) * mm});
            skLineSegment(sketch, "E773", {"start": v(-23.54, -18.45) * mm, "end": v(-23.55, -18.5) * mm});
            skLineSegment(sketch, "E774", {"start": v(-23.55, -18.5) * mm, "end": v(-23.55, -18.53) * mm});
            skLineSegment(sketch, "E775", {"start": v(-23.55, -18.53) * mm, "end": v(-23.55, -18.6) * mm});
            skLineSegment(sketch, "E776", {"start": v(-23.55, -18.6) * mm, "end": v(-23.56, -18.76) * mm});
            skLineSegment(sketch, "E777", {"start": v(-23.56, -18.76) * mm, "end": v(-23.57, -18.94) * mm});
            skLineSegment(sketch, "E778", {"start": v(-23.57, -18.94) * mm, "end": v(-23.58, -19.08) * mm});
            skLineSegment(sketch, "E779", {"start": v(-23.58, -19.08) * mm, "end": v(-23.58, -19.12) * mm});
            skLineSegment(sketch, "E780", {"start": v(-23.58, -19.12) * mm, "end": v(-23.58, -19.19) * mm});
            skLineSegment(sketch, "E781", {"start": v(-23.58, -19.19) * mm, "end": v(-23.6, -19.38) * mm});
            skLineSegment(sketch, "E782", {"start": v(-23.6, -19.38) * mm, "end": v(-23.6, -19.58) * mm});
            skLineSegment(sketch, "E783", {"start": v(-23.6, -19.58) * mm, "end": v(-23.62, -19.74) * mm});
            skLineSegment(sketch, "E784", {"start": v(-23.62, -19.74) * mm, "end": v(-23.63, -19.86) * mm});
            skLineSegment(sketch, "E785", {"start": v(-23.63, -19.86) * mm, "end": v(-23.65, -19.96) * mm});
            skLineSegment(sketch, "E786", {"start": v(-23.65, -19.96) * mm, "end": v(-23.68, -20.05) * mm});
            skLineSegment(sketch, "E787", {"start": v(-23.68, -20.05) * mm, "end": v(-23.72, -20.13) * mm});
            skLineSegment(sketch, "E788", {"start": v(-23.72, -20.13) * mm, "end": v(-23.75, -20.2) * mm});
            skLineSegment(sketch, "E789", {"start": v(-23.75, -20.2) * mm, "end": v(-23.76, -20.23) * mm});
            skLineSegment(sketch, "E790", {"start": v(-23.76, -20.23) * mm, "end": v(-23.8, -20.3) * mm});
            skLineSegment(sketch, "E791", {"start": v(-23.8, -20.3) * mm, "end": v(-23.92, -20.5) * mm});
            skLineSegment(sketch, "E792", {"start": v(-23.92, -20.5) * mm, "end": v(-24.1, -20.77) * mm});
            skLineSegment(sketch, "E793", {"start": v(-24.1, -20.77) * mm, "end": v(-24.3, -21.02) * mm});
            skLineSegment(sketch, "E794", {"start": v(-24.3, -21.02) * mm, "end": v(-24.44, -21.16) * mm});
            skLineSegment(sketch, "E795", {"start": v(-24.44, -21.16) * mm, "end": v(-24.49, -21.2) * mm});
            skLineSegment(sketch, "E796", {"start": v(-24.49, -21.2) * mm, "end": v(-24.5, -21.22) * mm});
            skLineSegment(sketch, "E797", {"start": v(-24.5, -21.22) * mm, "end": v(-24.57, -21.27) * mm});
            skLineSegment(sketch, "E798", {"start": v(-24.57, -21.27) * mm, "end": v(-24.7, -21.35) * mm});
            skLineSegment(sketch, "E799", {"start": v(-24.7, -21.35) * mm, "end": v(-24.84, -21.45) * mm});
            skLineSegment(sketch, "E800", {"start": v(-24.84, -21.45) * mm, "end": v(-24.95, -21.52) * mm});
            skLineSegment(sketch, "E801", {"start": v(-24.95, -21.52) * mm, "end": v(-24.99, -21.54) * mm});
            skLineSegment(sketch, "E802", {"start": v(-24.99, -21.54) * mm, "end": v(-25.03, -21.57) * mm});
            skLineSegment(sketch, "E803", {"start": v(-25.03, -21.57) * mm, "end": v(-25.16, -21.65) * mm});
            skLineSegment(sketch, "E804", {"start": v(-25.16, -21.65) * mm, "end": v(-25.38, -21.78) * mm});
            skLineSegment(sketch, "E805", {"start": v(-25.38, -21.78) * mm, "end": v(-25.63, -21.93) * mm});
            skLineSegment(sketch, "E806", {"start": v(-25.63, -21.93) * mm, "end": v(-25.8, -22.04) * mm});
            skLineSegment(sketch, "E807", {"start": v(-25.8, -22.04) * mm, "end": v(-25.86, -22.08) * mm});
            skLineSegment(sketch, "E808", {"start": v(-25.86, -22.08) * mm, "end": v(-25.93, -22.12) * mm});
            skLineSegment(sketch, "E809", {"start": v(-25.93, -22.12) * mm, "end": v(-26.13, -22.24) * mm});
            skLineSegment(sketch, "E810", {"start": v(-26.13, -22.24) * mm, "end": v(-26.46, -22.44) * mm});
            skLineSegment(sketch, "E811", {"start": v(-26.46, -22.44) * mm, "end": v(-26.8, -22.65) * mm});
            skLineSegment(sketch, "E812", {"start": v(-26.8, -22.65) * mm, "end": v(-27.06, -22.8) * mm});
            skLineSegment(sketch, "E813", {"start": v(-27.06, -22.8) * mm, "end": v(-27.14, -22.85) * mm});
            skLineSegment(sketch, "E814", {"start": v(-27.14, -22.85) * mm, "end": v(-27.22, -22.9) * mm});
            skLineSegment(sketch, "E815", {"start": v(-27.22, -22.9) * mm, "end": v(-27.46, -23.04) * mm});
            skLineSegment(sketch, "E816", {"start": v(-27.46, -23.04) * mm, "end": v(-27.77, -23.23) * mm});
            skLineSegment(sketch, "E817", {"start": v(-27.77, -23.23) * mm, "end": v(-28.06, -23.4) * mm});
            skLineSegment(sketch, "E818", {"start": v(-28.06, -23.4) * mm, "end": v(-28.21, -23.5) * mm});
            skLineSegment(sketch, "E819", {"start": v(-28.21, -23.5) * mm, "end": v(-28.26, -23.53) * mm});
            skLineSegment(sketch, "E820", {"start": v(-28.26, -23.53) * mm, "end": v(-28.3, -23.56) * mm});
            skLineSegment(sketch, "E821", {"start": v(-28.3, -23.56) * mm, "end": v(-28.45, -23.64) * mm});
            skLineSegment(sketch, "E822", {"start": v(-28.45, -23.64) * mm, "end": v(-28.66, -23.78) * mm});
            skLineSegment(sketch, "E823", {"start": v(-28.66, -23.78) * mm, "end": v(-28.89, -23.9) * mm});
            skLineSegment(sketch, "E824", {"start": v(-28.89, -23.9) * mm, "end": v(-29.04, -24) * mm});
            skLineSegment(sketch, "E825", {"start": v(-29.04, -24) * mm, "end": v(-29.09, -24.03) * mm});
            skLineSegment(sketch, "E826", {"start": v(-29.09, -24.03) * mm, "end": v(-29.14, -24.06) * mm});
            skLineSegment(sketch, "E827", {"start": v(-29.14, -24.06) * mm, "end": v(-29.3, -24.16) * mm});
            skLineSegment(sketch, "E828", {"start": v(-29.3, -24.16) * mm, "end": v(-29.56, -24.32) * mm});
            skLineSegment(sketch, "E829", {"start": v(-29.56, -24.32) * mm, "end": v(-29.84, -24.48) * mm});
            skLineSegment(sketch, "E830", {"start": v(-29.84, -24.48) * mm, "end": v(-30.03, -24.6) * mm});
            skLineSegment(sketch, "E831", {"start": v(-30.03, -24.6) * mm, "end": v(-30.1, -24.64) * mm});
            skLineSegment(sketch, "E832", {"start": v(-30.1, -24.64) * mm, "end": v(-30.15, -24.68) * mm});
            skLineSegment(sketch, "E833", {"start": v(-30.15, -24.68) * mm, "end": v(-30.34, -24.79) * mm});
            skLineSegment(sketch, "E834", {"start": v(-30.34, -24.79) * mm, "end": v(-30.57, -24.93) * mm});
            skLineSegment(sketch, "E835", {"start": v(-30.57, -24.93) * mm, "end": v(-30.78, -25.06) * mm});
            skLineSegment(sketch, "E836", {"start": v(-30.78, -25.06) * mm, "end": v(-30.9, -25.12) * mm});
            skLineSegment(sketch, "E837", {"start": v(-30.9, -25.12) * mm, "end": v(-30.93, -25.14) * mm});
            skLineSegment(sketch, "E838", {"start": v(-30.93, -25.14) * mm, "end": v(-31.12, -25.25) * mm});
            skLineSegment(sketch, "E839", {"start": v(-31.12, -25.25) * mm, "end": v(-31.64, -25.6) * mm});
            skLineSegment(sketch, "E840", {"start": v(-31.64, -25.6) * mm, "end": v(-32.28, -26.1) * mm});
            skLineSegment(sketch, "E841", {"start": v(-32.28, -26.1) * mm, "end": v(-32.87, -26.7) * mm});
            skLineSegment(sketch, "E842", {"start": v(-32.87, -26.7) * mm, "end": v(-33.29, -27.2) * mm});
            skLineSegment(sketch, "E843", {"start": v(-33.29, -27.2) * mm, "end": v(-33.42, -27.38) * mm});
            skLineSegment(sketch, "E844", {"start": v(-33.42, -27.38) * mm, "end": v(-33.5, -27.5) * mm});
            skLineSegment(sketch, "E845", {"start": v(-33.5, -27.5) * mm, "end": v(-33.75, -27.86) * mm});
            skLineSegment(sketch, "E846", {"start": v(-33.75, -27.86) * mm, "end": v(-33.97, -28.26) * mm});
            skLineSegment(sketch, "E847", {"start": v(-33.97, -28.26) * mm, "end": v(-34.1, -28.58) * mm});
            skLineSegment(sketch, "E848", {"start": v(-34.1, -28.58) * mm, "end": v(-34.15, -28.78) * mm});
            skLineSegment(sketch, "E849", {"start": v(-34.15, -28.78) * mm, "end": v(-34.15, -28.85) * mm});
            skLineSegment(sketch, "E850", {"start": v(-34.15, -28.85) * mm, "end": v(-34.15, -28.88) * mm});
            skLineSegment(sketch, "E851", {"start": v(-34.15, -28.88) * mm, "end": v(-34.15, -28.96) * mm});
            skLineSegment(sketch, "E852", {"start": v(-34.15, -28.96) * mm, "end": v(-34.14, -29.03) * mm});
            skLineSegment(sketch, "E853", {"start": v(-34.14, -29.03) * mm, "end": v(-34.1, -29.09) * mm});
            skLineSegment(sketch, "E854", {"start": v(-34.1, -29.09) * mm, "end": v(-34.07, -29.13) * mm});
            skLineSegment(sketch, "E855", {"start": v(-34.07, -29.13) * mm, "end": v(-34.06, -29.15) * mm});
            skLineSegment(sketch, "E856", {"start": v(-34.06, -29.15) * mm, "end": v(-34.03, -29.18) * mm});
            skLineSegment(sketch, "E857", {"start": v(-34.03, -29.18) * mm, "end": v(-33.92, -29.25) * mm});
            skLineSegment(sketch, "E858", {"start": v(-33.92, -29.25) * mm, "end": v(-33.75, -29.31) * mm});
            skLineSegment(sketch, "E859", {"start": v(-33.75, -29.31) * mm, "end": v(-33.5, -29.35) * mm});
            skLineSegment(sketch, "E860", {"start": v(-33.5, -29.35) * mm, "end": v(-33.28, -29.36) * mm});
            skLineSegment(sketch, "E861", {"start": v(-33.28, -29.36) * mm, "end": v(-33.2, -29.36) * mm});
            skLineSegment(sketch, "E862", {"start": v(-33.2, -29.36) * mm, "end": v(-33.11, -29.36) * mm});
            skLineSegment(sketch, "E863", {"start": v(-33.11, -29.36) * mm, "end": v(-32.84, -29.35) * mm});
            skLineSegment(sketch, "E864", {"start": v(-32.84, -29.35) * mm, "end": v(-32.57, -29.32) * mm});
            skLineSegment(sketch, "E865", {"start": v(-32.57, -29.32) * mm, "end": v(-32.53, -29.32) * mm});
            skLineSegment(sketch, "E866", {"start": v(-32.53, -29.32) * mm, "end": v(-32.5, -29.31) * mm});
            skLineSegment(sketch, "E867", {"start": v(-32.5, -29.31) * mm, "end": v(-32.4, -29.3) * mm});
            skLineSegment(sketch, "E868", {"start": v(-32.4, -29.3) * mm, "end": v(-32.3, -29.28) * mm});
            skLineSegment(sketch, "E869", {"start": v(-32.3, -29.28) * mm, "end": v(-32.2, -29.27) * mm});
            skLineSegment(sketch, "E870", {"start": v(-32.2, -29.27) * mm, "end": v(-32.14, -29.26) * mm});
            skLineSegment(sketch, "E871", {"start": v(-32.14, -29.26) * mm, "end": v(-32.12, -29.26) * mm});
            skLineSegment(sketch, "E872", {"start": v(-32.12, -29.26) * mm, "end": v(-31.93, -29.23) * mm});
            skLineSegment(sketch, "E873", {"start": v(-31.93, -29.23) * mm, "end": v(-31.36, -29.1) * mm});
            skLineSegment(sketch, "E874", {"start": v(-31.36, -29.1) * mm, "end": v(-30.6, -28.87) * mm});
            skLineSegment(sketch, "E875", {"start": v(-30.6, -28.87) * mm, "end": v(-29.86, -28.55) * mm});
            skLineSegment(sketch, "E876", {"start": v(-29.86, -28.55) * mm, "end": v(-29.33, -28.27) * mm});
            skLineSegment(sketch, "E877", {"start": v(-29.33, -28.27) * mm, "end": v(-29.17, -28.16) * mm});
            skLineSegment(sketch, "E878", {"start": v(-29.17, -28.16) * mm, "end": v(-29.13, -28.14) * mm});
            skLineSegment(sketch, "E879", {"start": v(-29.13, -28.14) * mm, "end": v(-29, -28.05) * mm});
            skLineSegment(sketch, "E880", {"start": v(-29, -28.05) * mm, "end": v(-28.74, -27.9) * mm});
            skLineSegment(sketch, "E881", {"start": v(-28.74, -27.9) * mm, "end": v(-28.43, -27.7) * mm});
            skLineSegment(sketch, "E882", {"start": v(-28.43, -27.7) * mm, "end": v(-28.19, -27.56) * mm});
            skLineSegment(sketch, "E883", {"start": v(-28.19, -27.56) * mm, "end": v(-28.1, -27.51) * mm});
            skLineSegment(sketch, "E884", {"start": v(-28.1, -27.51) * mm, "end": v(-28.02, -27.46) * mm});
            skLineSegment(sketch, "E885", {"start": v(-28.02, -27.46) * mm, "end": v(-27.76, -27.31) * mm});
            skLineSegment(sketch, "E886", {"start": v(-27.76, -27.31) * mm, "end": v(-27.4, -27.1) * mm});
            skLineSegment(sketch, "E887", {"start": v(-27.4, -27.1) * mm, "end": v(-27.08, -26.9) * mm});
            skLineSegment(sketch, "E888", {"start": v(-27.08, -26.9) * mm, "end": v(-26.9, -26.79) * mm});
            skLineSegment(sketch, "E889", {"start": v(-26.9, -26.79) * mm, "end": v(-26.83, -26.75) * mm});
            skLineSegment(sketch, "E890", {"start": v(-26.83, -26.75) * mm, "end": v(-26.8, -26.73) * mm});
            skLineSegment(sketch, "E891", {"start": v(-26.8, -26.73) * mm, "end": v(-26.7, -26.67) * mm});
            skLineSegment(sketch, "E892", {"start": v(-26.7, -26.67) * mm, "end": v(-26.52, -26.57) * mm});
            skLineSegment(sketch, "E893", {"start": v(-26.52, -26.57) * mm, "end": v(-26.3, -26.44) * mm});
            skLineSegment(sketch, "E894", {"start": v(-26.3, -26.44) * mm, "end": v(-26.06, -26.3) * mm});
            skLineSegment(sketch, "E895", {"start": v(-26.06, -26.3) * mm, "end": v(-25.8, -26.13) * mm});
            skLineSegment(sketch, "E896", {"start": v(-25.8, -26.13) * mm, "end": v(-25.5, -25.96) * mm});
            skLineSegment(sketch, "E897", {"start": v(-25.5, -25.96) * mm, "end": v(-25.22, -25.79) * mm});
            skLineSegment(sketch, "E898", {"start": v(-25.22, -25.79) * mm, "end": v(-25, -25.65) * mm});
            skLineSegment(sketch, "E899", {"start": v(-25, -25.65) * mm, "end": v(-24.92, -25.61) * mm});
            skLineSegment(sketch, "E900", {"start": v(-24.92, -25.61) * mm, "end": v(-24.85, -25.57) * mm});
            skLineSegment(sketch, "E901", {"start": v(-24.85, -25.57) * mm, "end": v(-24.64, -25.44) * mm});
            skLineSegment(sketch, "E902", {"start": v(-24.64, -25.44) * mm, "end": v(-24.36, -25.28) * mm});
            skLineSegment(sketch, "E903", {"start": v(-24.36, -25.28) * mm, "end": v(-24.1, -25.12) * mm});
            skLineSegment(sketch, "E904", {"start": v(-24.1, -25.12) * mm, "end": v(-23.88, -24.99) * mm});
            skLineSegment(sketch, "E905", {"start": v(-23.88, -24.99) * mm, "end": v(-23.68, -24.87) * mm});
            skLineSegment(sketch, "E906", {"start": v(-23.68, -24.87) * mm, "end": v(-23.52, -24.77) * mm});
            skLineSegment(sketch, "E907", {"start": v(-23.52, -24.77) * mm, "end": v(-23.4, -24.7) * mm});
            skLineSegment(sketch, "E908", {"start": v(-23.4, -24.7) * mm, "end": v(-23.36, -24.67) * mm});
            skLineSegment(sketch, "E909", {"start": v(-23.36, -24.67) * mm, "end": v(-23.34, -24.66) * mm});
            skLineSegment(sketch, "E910", {"start": v(-23.34, -24.66) * mm, "end": v(-23.25, -24.6) * mm});
            skLineSegment(sketch, "E911", {"start": v(-23.25, -24.6) * mm, "end": v(-22.96, -24.44) * mm});
            skLineSegment(sketch, "E912", {"start": v(-22.96, -24.44) * mm, "end": v(-22.6, -24.28) * mm});
            skLineSegment(sketch, "E913", {"start": v(-22.6, -24.28) * mm, "end": v(-22.26, -24.17) * mm});
            skLineSegment(sketch, "E914", {"start": v(-22.26, -24.17) * mm, "end": v(-21.98, -24.12) * mm});
            skLineSegment(sketch, "E915", {"start": v(-21.98, -24.12) * mm, "end": v(-21.89, -24.1) * mm});
            skLineSegment(sketch, "E916", {"start": v(-21.89, -24.1) * mm, "end": v(-21.84, -24.1) * mm});
            skLineSegment(sketch, "E917", {"start": v(-21.84, -24.1) * mm, "end": v(-21.68, -24.09) * mm});
            skLineSegment(sketch, "E918", {"start": v(-21.68, -24.09) * mm, "end": v(-21.5, -24.08) * mm});
            skLineSegment(sketch, "E919", {"start": v(-21.5, -24.08) * mm, "end": v(-21.36, -24.08) * mm});
            skLineSegment(sketch, "E920", {"start": v(-21.36, -24.08) * mm, "end": v(-21.2, -24.1) * mm});
            skLineSegment(sketch, "E921", {"start": v(-21.2, -24.1) * mm, "end": v(-21.04, -24.16) * mm});
            skLineSegment(sketch, "E922", {"start": v(-21.04, -24.16) * mm, "end": v(-20.84, -24.23) * mm});
            skLineSegment(sketch, "E923", {"start": v(-20.84, -24.23) * mm, "end": v(-20.6, -24.34) * mm});
            skLineSegment(sketch, "E924", {"start": v(-20.6, -24.34) * mm, "end": v(-20.38, -24.44) * mm});
            skLineSegment(sketch, "E925", {"start": v(-20.38, -24.44) * mm, "end": v(-20.3, -24.47) * mm});
            skLineSegment(sketch, "E926", {"start": v(-20.3, -24.47) * mm, "end": v(-20.22, -24.51) * mm});
            skLineSegment(sketch, "E927", {"start": v(-20.22, -24.51) * mm, "end": v(-19.96, -24.63) * mm});
            skLineSegment(sketch, "E928", {"start": v(-19.96, -24.63) * mm, "end": v(-19.62, -24.79) * mm});
            skLineSegment(sketch, "E929", {"start": v(-19.62, -24.79) * mm, "end": v(-19.32, -24.93) * mm});
            skLineSegment(sketch, "E930", {"start": v(-19.32, -24.93) * mm, "end": v(-19.14, -25) * mm});
            skLineSegment(sketch, "E931", {"start": v(-19.14, -25) * mm, "end": v(-19.09, -25.03) * mm});
            skLineSegment(sketch, "E932", {"start": v(-19.09, -25.03) * mm, "end": v(-19.04, -25.05) * mm});
            skLineSegment(sketch, "E933", {"start": v(-19.04, -25.05) * mm, "end": v(-18.92, -25.11) * mm});
            skLineSegment(sketch, "E934", {"start": v(-18.92, -25.11) * mm, "end": v(-18.78, -25.18) * mm});
            skLineSegment(sketch, "E935", {"start": v(-18.78, -25.18) * mm, "end": v(-18.7, -25.23) * mm});
            skLineSegment(sketch, "E936", {"start": v(-18.7, -25.23) * mm, "end": v(-18.66, -25.25) * mm});
            skLineSegment(sketch, "E937", {"start": v(-18.66, -25.25) * mm, "end": v(-18.66, -25.25) * mm});
            skLineSegment(sketch, "E938", {"start": v(-18.66, -25.25) * mm, "end": v(-18.67, -25.27) * mm});
            skLineSegment(sketch, "E939", {"start": v(-18.67, -25.27) * mm, "end": v(-18.7, -25.29) * mm});
            skLineSegment(sketch, "E940", {"start": v(-18.7, -25.29) * mm, "end": v(-18.74, -25.32) * mm});
            skLineSegment(sketch, "E941", {"start": v(-18.74, -25.32) * mm, "end": v(-18.82, -25.38) * mm});
            skLineSegment(sketch, "E942", {"start": v(-18.82, -25.38) * mm, "end": v(-18.93, -25.44) * mm});
            skLineSegment(sketch, "E943", {"start": v(-18.93, -25.44) * mm, "end": v(-19.08, -25.53) * mm});
            skLineSegment(sketch, "E944", {"start": v(-19.08, -25.53) * mm, "end": v(-19.27, -25.65) * mm});
            skLineSegment(sketch, "E945", {"start": v(-19.27, -25.65) * mm, "end": v(-19.45, -25.76) * mm});
            skLineSegment(sketch, "E946", {"start": v(-19.45, -25.76) * mm, "end": v(-19.51, -25.8) * mm});
            skLineSegment(sketch, "E947", {"start": v(-19.51, -25.8) * mm, "end": v(-19.6, -25.85) * mm});
            skLineSegment(sketch, "E948", {"start": v(-19.6, -25.85) * mm, "end": v(-19.89, -26.02) * mm});
            skLineSegment(sketch, "E949", {"start": v(-19.89, -26.02) * mm, "end": v(-20.13, -26.2) * mm});
            skLineSegment(sketch, "E950", {"start": v(-20.13, -26.2) * mm, "end": v(-20.27, -26.34) * mm});
            skLineSegment(sketch, "E951", {"start": v(-20.27, -26.34) * mm, "end": v(-20.32, -26.44) * mm});
            skLineSegment(sketch, "E952", {"start": v(-20.32, -26.44) * mm, "end": v(-20.33, -26.47) * mm});
            skLineSegment(sketch, "E953", {"start": v(-20.33, -26.47) * mm, "end": v(-20.34, -26.5) * mm});
            skLineSegment(sketch, "E954", {"start": v(-20.34, -26.5) * mm, "end": v(-20.35, -26.61) * mm});
            skLineSegment(sketch, "E955", {"start": v(-20.35, -26.61) * mm, "end": v(-20.31, -26.77) * mm});
            skLineSegment(sketch, "E956", {"start": v(-20.31, -26.77) * mm, "end": v(-20.22, -26.96) * mm});
            skLineSegment(sketch, "E957", {"start": v(-20.22, -26.96) * mm, "end": v(-20.1, -27.15) * mm});
            skLineSegment(sketch, "E958", {"start": v(-20.1, -27.15) * mm, "end": v(-20.07, -27.21) * mm});
            skLineSegment(sketch, "E959", {"start": v(-20.07, -27.21) * mm, "end": v(-20.02, -27.27) * mm});
            skLineSegment(sketch, "E960", {"start": v(-20.02, -27.27) * mm, "end": v(-19.9, -27.45) * mm});
            skLineSegment(sketch, "E961", {"start": v(-19.9, -27.45) * mm, "end": v(-19.75, -27.6) * mm});
            skLineSegment(sketch, "E962", {"start": v(-19.75, -27.6) * mm, "end": v(-19.61, -27.66) * mm});
            skLineSegment(sketch, "E963", {"start": v(-19.61, -27.66) * mm, "end": v(-19.5, -27.67) * mm});
            skLineSegment(sketch, "E964", {"start": v(-19.5, -27.67) * mm, "end": v(-19.46, -27.66) * mm});
            skLineSegment(sketch, "E965", {"start": v(-19.46, -27.66) * mm, "end": v(-19.44, -27.66) * mm});
            skLineSegment(sketch, "E966", {"start": v(-19.44, -27.66) * mm, "end": v(-19.38, -27.65) * mm});
            skLineSegment(sketch, "E967", {"start": v(-19.38, -27.65) * mm, "end": v(-19.28, -27.62) * mm});
            skLineSegment(sketch, "E968", {"start": v(-19.28, -27.62) * mm, "end": v(-19.17, -27.57) * mm});
            skLineSegment(sketch, "E969", {"start": v(-19.17, -27.57) * mm, "end": v(-19.03, -27.5) * mm});
            skLineSegment(sketch, "E970", {"start": v(-19.03, -27.5) * mm, "end": v(-18.85, -27.4) * mm});
            skLineSegment(sketch, "E971", {"start": v(-18.85, -27.4) * mm, "end": v(-18.64, -27.27) * mm});
            skLineSegment(sketch, "E972", {"start": v(-18.64, -27.27) * mm, "end": v(-18.38, -27.1) * mm});
            skLineSegment(sketch, "E973", {"start": v(-18.38, -27.1) * mm, "end": v(-18.15, -26.95) * mm});
            skLineSegment(sketch, "E974", {"start": v(-18.15, -26.95) * mm, "end": v(-18.07, -26.9) * mm});
            skLineSegment(sketch, "E975", {"start": v(-18.07, -26.9) * mm, "end": v(-18.01, -26.87) * mm});
            skLineSegment(sketch, "E976", {"start": v(-18.01, -26.87) * mm, "end": v(-17.84, -26.75) * mm});
            skLineSegment(sketch, "E977", {"start": v(-17.84, -26.75) * mm, "end": v(-17.61, -26.6) * mm});
            skLineSegment(sketch, "E978", {"start": v(-17.61, -26.6) * mm, "end": v(-17.4, -26.47) * mm});
            skLineSegment(sketch, "E979", {"start": v(-17.4, -26.47) * mm, "end": v(-17.3, -26.4) * mm});
            skLineSegment(sketch, "E980", {"start": v(-17.3, -26.4) * mm, "end": v(-17.26, -26.37) * mm});
            skLineSegment(sketch, "E981", {"start": v(-17.26, -26.37) * mm, "end": v(-17.23, -26.35) * mm});
            skLineSegment(sketch, "E982", {"start": v(-17.23, -26.35) * mm, "end": v(-17.15, -26.3) * mm});
            skLineSegment(sketch, "E983", {"start": v(-17.15, -26.3) * mm, "end": v(-17.05, -26.24) * mm});
            skLineSegment(sketch, "E984", {"start": v(-17.05, -26.24) * mm, "end": v(-16.97, -26.2) * mm});
            skLineSegment(sketch, "E985", {"start": v(-16.97, -26.2) * mm, "end": v(-16.94, -26.17) * mm});
            skLineSegment(sketch, "E986", {"start": v(-16.94, -26.17) * mm, "end": v(-16.93, -26.17) * mm});
            skLineSegment(sketch, "E987", {"start": v(-16.93, -26.17) * mm, "end": v(-16.93, -26.17) * mm});
            skLineSegment(sketch, "E988", {"start": v(-16.93, -26.17) * mm, "end": v(-16.84, -26.2) * mm});
            skLineSegment(sketch, "E989", {"start": v(-16.84, -26.2) * mm, "end": v(-16.64, -26.28) * mm});
            skLineSegment(sketch, "E990", {"start": v(-16.64, -26.28) * mm, "end": v(-16.35, -26.4) * mm});
            skLineSegment(sketch, "E991", {"start": v(-16.35, -26.4) * mm, "end": v(-16.09, -26.51) * mm});
            skLineSegment(sketch, "E992", {"start": v(-16.09, -26.51) * mm, "end": v(-16, -26.55) * mm});
            skLineSegment(sketch, "E993", {"start": v(-16, -26.55) * mm, "end": v(-15.89, -26.6) * mm});
            skLineSegment(sketch, "E994", {"start": v(-15.89, -26.6) * mm, "end": v(-15.56, -26.76) * mm});
            skLineSegment(sketch, "E995", {"start": v(-15.56, -26.76) * mm, "end": v(-15.08, -26.97) * mm});
            skLineSegment(sketch, "E996", {"start": v(-15.08, -26.97) * mm, "end": v(-14.6, -27.2) * mm});
            skLineSegment(sketch, "E997", {"start": v(-14.6, -27.2) * mm, "end": v(-14.13, -27.4) * mm});
            skLineSegment(sketch, "E998", {"start": v(-14.13, -27.4) * mm, "end": v(-13.7, -27.6) * mm});
            skLineSegment(sketch, "E999", {"start": v(-13.7, -27.6) * mm, "end": v(-13.34, -27.77) * mm});
            skLineSegment(sketch, "E1000", {"start": v(-13.34, -27.77) * mm, "end": v(-13.07, -27.89) * mm});
            skLineSegment(sketch, "E1001", {"start": v(-13.07, -27.89) * mm, "end": v(-12.96, -27.94) * mm});
            skLineSegment(sketch, "E1002", {"start": v(-12.96, -27.94) * mm, "end": v(-12.92, -27.96) * mm});
            skLineSegment(sketch, "E1003", {"start": v(-12.92, -27.96) * mm, "end": v(-12.9, -27.97) * mm});
            skLineSegment(sketch, "E1004", {"start": v(-12.9, -27.97) * mm, "end": v(-12.83, -28) * mm});
            skLineSegment(sketch, "E1005", {"start": v(-12.83, -28) * mm, "end": v(-12.74, -28.04) * mm});
            skLineSegment(sketch, "E1006", {"start": v(-12.74, -28.04) * mm, "end": v(-12.64, -28.09) * mm});
            skLineSegment(sketch, "E1007", {"start": v(-12.64, -28.09) * mm, "end": v(-12.58, -28.11) * mm});
            skLineSegment(sketch, "E1008", {"start": v(-12.58, -28.11) * mm, "end": v(-12.56, -28.12) * mm});
            skLineSegment(sketch, "E1009", {"start": v(-12.56, -28.12) * mm, "end": v(-12.54, -28.13) * mm});
            skLineSegment(sketch, "E1010", {"start": v(-12.54, -28.13) * mm, "end": v(-12.48, -28.16) * mm});
            skLineSegment(sketch, "E1011", {"start": v(-12.48, -28.16) * mm, "end": v(-12.38, -28.2) * mm});
            skLineSegment(sketch, "E1012", {"start": v(-12.38, -28.2) * mm, "end": v(-12.27, -28.26) * mm});
            skLineSegment(sketch, "E1013", {"start": v(-12.27, -28.26) * mm, "end": v(-12.19, -28.3) * mm});
            skLineSegment(sketch, "E1014", {"start": v(-12.19, -28.3) * mm, "end": v(-12.16, -28.3) * mm});
            skLineSegment(sketch, "E1015", {"start": v(-12.16, -28.3) * mm, "end": v(-12.13, -28.32) * mm});
            skLineSegment(sketch, "E1016", {"start": v(-12.13, -28.32) * mm, "end": v(-12, -28.38) * mm});
            skLineSegment(sketch, "E1017", {"start": v(-12, -28.38) * mm, "end": v(-11.73, -28.5) * mm});
            skLineSegment(sketch, "E1018", {"start": v(-11.73, -28.5) * mm, "end": v(-11.39, -28.66) * mm});
            skLineSegment(sketch, "E1019", {"start": v(-11.39, -28.66) * mm, "end": v(-11.11, -28.79) * mm});
            skLineSegment(sketch, "E1020", {"start": v(-11.11, -28.79) * mm, "end": v(-11.02, -28.83) * mm});
            skLineSegment(sketch, "E1021", {"start": v(-11.02, -28.83) * mm, "end": v(-10.93, -28.87) * mm});
            skLineSegment(sketch, "E1022", {"start": v(-10.93, -28.87) * mm, "end": v(-10.65, -29) * mm});
            skLineSegment(sketch, "E1023", {"start": v(-10.65, -29) * mm, "end": v(-10.32, -29.15) * mm});
            skLineSegment(sketch, "E1024", {"start": v(-10.32, -29.15) * mm, "end": v(-10.05, -29.27) * mm});
            skLineSegment(sketch, "E1025", {"start": v(-10.05, -29.27) * mm, "end": v(-9.93, -29.33) * mm});
            skLineSegment(sketch, "E1026", {"start": v(-9.93, -29.33) * mm, "end": v(-9.9, -29.34) * mm});
            skLineSegment(sketch, "E1027", {"start": v(-9.9, -29.34) * mm, "end": v(-9.87, -29.35) * mm});
            skLineSegment(sketch, "E1028", {"start": v(-9.87, -29.35) * mm, "end": v(-9.8, -29.39) * mm});
            skLineSegment(sketch, "E1029", {"start": v(-9.8, -29.39) * mm, "end": v(-9.69, -29.44) * mm});
            skLineSegment(sketch, "E1030", {"start": v(-9.69, -29.44) * mm, "end": v(-9.58, -29.48) * mm});
            skLineSegment(sketch, "E1031", {"start": v(-9.58, -29.48) * mm, "end": v(-9.51, -29.52) * mm});
            skLineSegment(sketch, "E1032", {"start": v(-9.51, -29.52) * mm, "end": v(-9.5, -29.53) * mm});
            skLineSegment(sketch, "E1033", {"start": v(-9.5, -29.53) * mm, "end": v(-9.47, -29.54) * mm});
            skLineSegment(sketch, "E1034", {"start": v(-9.47, -29.54) * mm, "end": v(-9.4, -29.57) * mm});
            skLineSegment(sketch, "E1035", {"start": v(-9.4, -29.57) * mm, "end": v(-9.29, -29.62) * mm});
            skLineSegment(sketch, "E1036", {"start": v(-9.29, -29.62) * mm, "end": v(-9.17, -29.67) * mm});
            skLineSegment(sketch, "E1037", {"start": v(-9.17, -29.67) * mm, "end": v(-9.08, -29.71) * mm});
            skLineSegment(sketch, "E1038", {"start": v(-9.08, -29.71) * mm, "end": v(-9.06, -29.73) * mm});
            skLineSegment(sketch, "E1039", {"start": v(-9.06, -29.73) * mm, "end": v(-9.02, -29.74) * mm});
            skLineSegment(sketch, "E1040", {"start": v(-9.02, -29.74) * mm, "end": v(-8.9, -29.8) * mm});
            skLineSegment(sketch, "E1041", {"start": v(-8.9, -29.8) * mm, "end": v(-8.68, -29.9) * mm});
            skLineSegment(sketch, "E1042", {"start": v(-8.68, -29.9) * mm, "end": v(-8.4, -30.02) * mm});
            skLineSegment(sketch, "E1043", {"start": v(-8.4, -30.02) * mm, "end": v(-8.19, -30.12) * mm});
            skLineSegment(sketch, "E1044", {"start": v(-8.19, -30.12) * mm, "end": v(-8.12, -30.15) * mm});
            skLineSegment(sketch, "E1045", {"start": v(-8.12, -30.15) * mm, "end": v(-8.04, -30.19) * mm});
            skLineSegment(sketch, "E1046", {"start": v(-8.04, -30.19) * mm, "end": v(-7.82, -30.29) * mm});
            skLineSegment(sketch, "E1047", {"start": v(-7.82, -30.29) * mm, "end": v(-7.54, -30.42) * mm});
            skLineSegment(sketch, "E1048", {"start": v(-7.54, -30.42) * mm, "end": v(-7.3, -30.53) * mm});
            skLineSegment(sketch, "E1049", {"start": v(-7.3, -30.53) * mm, "end": v(-7.16, -30.6) * mm});
            skLineSegment(sketch, "E1050", {"start": v(-7.16, -30.6) * mm, "end": v(-7.11, -30.61) * mm});
            skLineSegment(sketch, "E1051", {"start": v(-7.11, -30.61) * mm, "end": v(-7.08, -30.63) * mm});
            skLineSegment(sketch, "E1052", {"start": v(-7.08, -30.63) * mm, "end": v(-7, -30.67) * mm});
            skLineSegment(sketch, "E1053", {"start": v(-7, -30.67) * mm, "end": v(-6.89, -30.71) * mm});
            skLineSegment(sketch, "E1054", {"start": v(-6.89, -30.71) * mm, "end": v(-6.82, -30.75) * mm});
            skLineSegment(sketch, "E1055", {"start": v(-6.82, -30.75) * mm, "end": v(-6.8, -30.76) * mm});
            skLineSegment(sketch, "E1056", {"start": v(-6.8, -30.76) * mm, "end": v(-6.79, -30.76) * mm});
            skLineSegment(sketch, "E1057", {"start": v(-6.79, -30.76) * mm, "end": v(-6.78, -30.76) * mm});
            skLineSegment(sketch, "E1058", {"start": v(-6.78, -30.76) * mm, "end": v(-6.75, -30.74) * mm});
            skLineSegment(sketch, "E1059", {"start": v(-6.75, -30.74) * mm, "end": v(-6.66, -30.69) * mm});
            skLineSegment(sketch, "E1060", {"start": v(-6.66, -30.69) * mm, "end": v(-6.54, -30.6) * mm});
            skLineSegment(sketch, "E1061", {"start": v(-6.54, -30.6) * mm, "end": v(-6.43, -30.54) * mm});
            skLineSegment(sketch, "E1062", {"start": v(-6.43, -30.54) * mm, "end": v(-6.4, -30.51) * mm});
            skLineSegment(sketch, "E1063", {"start": v(-6.4, -30.51) * mm, "end": v(-6.35, -30.48) * mm});
            skLineSegment(sketch, "E1064", {"start": v(-6.35, -30.48) * mm, "end": v(-6.22, -30.4) * mm});
            skLineSegment(sketch, "E1065", {"start": v(-6.22, -30.4) * mm, "end": v(-6.03, -30.28) * mm});
            skLineSegment(sketch, "E1066", {"start": v(-6.03, -30.28) * mm, "end": v(-5.85, -30.16) * mm});
            skLineSegment(sketch, "E1067", {"start": v(-5.85, -30.16) * mm, "end": v(-5.73, -30.08) * mm});
            skLineSegment(sketch, "E1068", {"start": v(-5.73, -30.08) * mm, "end": v(-5.69, -30.05) * mm});
            skLineSegment(sketch, "E1069", {"start": v(-5.69, -30.05) * mm, "end": v(-5.66, -30.03) * mm});
            skLineSegment(sketch, "E1070", {"start": v(-5.66, -30.03) * mm, "end": v(-5.56, -29.97) * mm});
            skLineSegment(sketch, "E1071", {"start": v(-5.56, -29.97) * mm, "end": v(-5.46, -29.9) * mm});
            skLineSegment(sketch, "E1072", {"start": v(-5.46, -29.9) * mm, "end": v(-5.39, -29.85) * mm});
            skLineSegment(sketch, "E1073", {"start": v(-5.39, -29.85) * mm, "end": v(-5.36, -29.84) * mm});
            skLineSegment(sketch, "E1074", {"start": v(-5.36, -29.84) * mm, "end": v(-5.36, -29.84) * mm});
            skLineSegment(sketch, "E1075", {"start": v(-5.36, -29.84) * mm, "end": v(-5.36, -29.83) * mm});
            skLineSegment(sketch, "E1076", {"start": v(-5.36, -29.83) * mm, "end": v(-5.38, -29.82) * mm});
            skLineSegment(sketch, "E1077", {"start": v(-5.38, -29.82) * mm, "end": v(-5.42, -29.78) * mm});
            skLineSegment(sketch, "E1078", {"start": v(-5.42, -29.78) * mm, "end": v(-5.51, -29.72) * mm});
            skLineSegment(sketch, "E1079", {"start": v(-5.51, -29.72) * mm, "end": v(-5.64, -29.62) * mm});
            skLineSegment(sketch, "E1080", {"start": v(-5.64, -29.62) * mm, "end": v(-5.82, -29.5) * mm});
            skLineSegment(sketch, "E1081", {"start": v(-5.82, -29.5) * mm, "end": v(-6.05, -29.33) * mm});
            skLineSegment(sketch, "E1082", {"start": v(-6.05, -29.33) * mm, "end": v(-6.34, -29.12) * mm});
            skLineSegment(sketch, "E1083", {"start": v(-6.34, -29.12) * mm, "end": v(-6.6, -28.92) * mm});
            skLineSegment(sketch, "E1084", {"start": v(-6.6, -28.92) * mm, "end": v(-6.69, -28.86) * mm});
            skLineSegment(sketch, "E1085", {"start": v(-6.69, -28.86) * mm, "end": v(-6.76, -28.8) * mm});
            skLineSegment(sketch, "E1086", {"start": v(-6.76, -28.8) * mm, "end": v(-6.99, -28.64) * mm});
            skLineSegment(sketch, "E1087", {"start": v(-6.99, -28.64) * mm, "end": v(-7.29, -28.42) * mm});
            skLineSegment(sketch, "E1088", {"start": v(-7.29, -28.42) * mm, "end": v(-7.58, -28.21) * mm});
            skLineSegment(sketch, "E1089", {"start": v(-7.58, -28.21) * mm, "end": v(-7.86, -28.01) * mm});
            skLineSegment(sketch, "E1090", {"start": v(-7.86, -28.01) * mm, "end": v(-8.1, -27.84) * mm});
            skLineSegment(sketch, "E1091", {"start": v(-8.1, -27.84) * mm, "end": v(-8.28, -27.7) * mm});
            skLineSegment(sketch, "E1092", {"start": v(-8.28, -27.7) * mm, "end": v(-8.4, -27.6) * mm});
            skLineSegment(sketch, "E1093", {"start": v(-8.4, -27.6) * mm, "end": v(-8.45, -27.58) * mm});
            skLineSegment(sketch, "E1094", {"start": v(-8.45, -27.58) * mm, "end": v(-8.46, -27.57) * mm});
            skLineSegment(sketch, "E1095", {"start": v(-8.46, -27.57) * mm, "end": v(-8.47, -27.56) * mm});
            skLineSegment(sketch, "E1096", {"start": v(-8.47, -27.56) * mm, "end": v(-8.47, -27.52) * mm});
            skLineSegment(sketch, "E1097", {"start": v(-8.47, -27.52) * mm, "end": v(-8.44, -27.47) * mm});
            skLineSegment(sketch, "E1098", {"start": v(-8.44, -27.47) * mm, "end": v(-8.43, -27.45) * mm});
            skLineSegment(sketch, "E1099", {"start": v(-8.43, -27.45) * mm, "end": v(-8.43, -27.44) * mm});
            skLineSegment(sketch, "E1100", {"start": v(-8.43, -27.44) * mm, "end": v(-8.4, -27.39) * mm});
            skLineSegment(sketch, "E1101", {"start": v(-8.4, -27.39) * mm, "end": v(-8.39, -27.34) * mm});
            skLineSegment(sketch, "E1102", {"start": v(-8.39, -27.34) * mm, "end": v(-8.4, -27.34) * mm});
            skLineSegment(sketch, "E1103", {"start": v(-8.4, -27.34) * mm, "end": v(-8.4, -27.34) * mm});
            skLineSegment(sketch, "E1104", {"start": v(-8.4, -27.34) * mm, "end": v(-8.42, -27.3) * mm});
            skLineSegment(sketch, "E1105", {"start": v(-8.42, -27.3) * mm, "end": v(-8.5, -27.24) * mm});
            skLineSegment(sketch, "E1106", {"start": v(-8.5, -27.24) * mm, "end": v(-8.6, -27.14) * mm});
            skLineSegment(sketch, "E1107", {"start": v(-8.6, -27.14) * mm, "end": v(-8.69, -27.06) * mm});
            skLineSegment(sketch, "E1108", {"start": v(-8.69, -27.06) * mm, "end": v(-8.72, -27.03) * mm});
            skLineSegment(sketch, "E1109", {"start": v(-8.72, -27.03) * mm, "end": v(-8.75, -27) * mm});
            skLineSegment(sketch, "E1110", {"start": v(-8.75, -27) * mm, "end": v(-8.85, -26.92) * mm});
            skLineSegment(sketch, "E1111", {"start": v(-8.85, -26.92) * mm, "end": v(-8.98, -26.8) * mm});
            skLineSegment(sketch, "E1112", {"start": v(-8.98, -26.8) * mm, "end": v(-9.1, -26.7) * mm});
            skLineSegment(sketch, "E1113", {"start": v(-9.1, -26.7) * mm, "end": v(-9.15, -26.66) * mm});
            skLineSegment(sketch, "E1114", {"start": v(-9.15, -26.66) * mm, "end": v(-9.17, -26.64) * mm});
            skLineSegment(sketch, "E1115", {"start": v(-9.17, -26.64) * mm, "end": v(-9.3, -26.53) * mm});
            skLineSegment(sketch, "E1116", {"start": v(-9.3, -26.53) * mm, "end": v(-9.23, -26.44) * mm});
            skLineSegment(sketch, "E1117", {"start": v(-9.23, -26.44) * mm, "end": v(-9.22, -26.43) * mm});
            skLineSegment(sketch, "E1118", {"start": v(-9.22, -26.43) * mm, "end": v(-9.18, -26.36) * mm});
            skLineSegment(sketch, "E1119", {"start": v(-9.18, -26.36) * mm, "end": v(-9.16, -26.32) * mm});
            skLineSegment(sketch, "E1120", {"start": v(-9.16, -26.32) * mm, "end": v(-9.16, -26.3) * mm});
            skLineSegment(sketch, "E1121", {"start": v(-9.16, -26.3) * mm, "end": v(-9.16, -26.3) * mm});
            skLineSegment(sketch, "E1122", {"start": v(-9.16, -26.3) * mm, "end": v(-9.18, -26.25) * mm});
            skLineSegment(sketch, "E1123", {"start": v(-9.18, -26.25) * mm, "end": v(-9.25, -26.22) * mm});
            skLineSegment(sketch, "E1124", {"start": v(-9.25, -26.22) * mm, "end": v(-9.35, -26.2) * mm});
            skLineSegment(sketch, "E1125", {"start": v(-9.35, -26.2) * mm, "end": v(-9.44, -26.2) * mm});
            skLineSegment(sketch, "E1126", {"start": v(-9.44, -26.2) * mm, "end": v(-9.48, -26.2) * mm});
            skLineSegment(sketch, "E1127", {"start": v(-9.48, -26.2) * mm, "end": v(-9.5, -26.21) * mm});
            skLineSegment(sketch, "E1128", {"start": v(-9.5, -26.21) * mm, "end": v(-9.58, -26.22) * mm});
            skLineSegment(sketch, "E1129", {"start": v(-9.58, -26.22) * mm, "end": v(-9.64, -26.21) * mm});
            skLineSegment(sketch, "E1130", {"start": v(-9.64, -26.21) * mm, "end": v(-9.7, -26.2) * mm});
            skLineSegment(sketch, "E1131", {"start": v(-9.7, -26.2) * mm, "end": v(-9.74, -26.17) * mm});
            skLineSegment(sketch, "E1132", {"start": v(-9.74, -26.17) * mm, "end": v(-9.75, -26.15) * mm});
            skLineSegment(sketch, "E1133", {"start": v(-9.75, -26.15) * mm, "end": v(-9.8, -26.12) * mm});
            skLineSegment(sketch, "E1134", {"start": v(-9.8, -26.12) * mm, "end": v(-9.92, -26.02) * mm});
            skLineSegment(sketch, "E1135", {"start": v(-9.92, -26.02) * mm, "end": v(-10.15, -25.82) * mm});
            skLineSegment(sketch, "E1136", {"start": v(-10.15, -25.82) * mm, "end": v(-10.43, -25.57) * mm});
            skLineSegment(sketch, "E1137", {"start": v(-10.43, -25.57) * mm, "end": v(-10.73, -25.32) * mm});
            skLineSegment(sketch, "E1138", {"start": v(-10.73, -25.32) * mm, "end": v(-11.01, -25.07) * mm});
            skLineSegment(sketch, "E1139", {"start": v(-11.01, -25.07) * mm, "end": v(-11.25, -24.86) * mm});
            skLineSegment(sketch, "E1140", {"start": v(-11.25, -24.86) * mm, "end": v(-11.41, -24.71) * mm});
            skLineSegment(sketch, "E1141", {"start": v(-11.41, -24.71) * mm, "end": v(-11.47, -24.67) * mm});
            skLineSegment(sketch, "E1142", {"start": v(-11.47, -24.67) * mm, "end": v(-11.47, -24.65) * mm});
            skLineSegment(sketch, "E1143", {"start": v(-11.47, -24.65) * mm, "end": v(-11.47, -24.64) * mm});
            skLineSegment(sketch, "E1144", {"start": v(-11.47, -24.64) * mm, "end": v(-11.45, -24.61) * mm});
            skLineSegment(sketch, "E1145", {"start": v(-11.45, -24.61) * mm, "end": v(-11.42, -24.57) * mm});
            skLineSegment(sketch, "E1146", {"start": v(-11.42, -24.57) * mm, "end": v(-11.4, -24.56) * mm});
            skLineSegment(sketch, "E1147", {"start": v(-11.4, -24.56) * mm, "end": v(-11.4, -24.55) * mm});
            skLineSegment(sketch, "E1148", {"start": v(-11.4, -24.55) * mm, "end": v(-11.36, -24.5) * mm});
            skLineSegment(sketch, "E1149", {"start": v(-11.36, -24.5) * mm, "end": v(-11.34, -24.45) * mm});
            skLineSegment(sketch, "E1150", {"start": v(-11.34, -24.45) * mm, "end": v(-11.36, -24.4) * mm});
            skLineSegment(sketch, "E1151", {"start": v(-11.36, -24.4) * mm, "end": v(-11.4, -24.37) * mm});
            skLineSegment(sketch, "E1152", {"start": v(-11.4, -24.37) * mm, "end": v(-11.4, -24.37) * mm});
            skLineSegment(sketch, "E1153", {"start": v(-11.4, -24.37) * mm, "end": v(-11.41, -24.37) * mm});
            skLineSegment(sketch, "E1154", {"start": v(-11.41, -24.37) * mm, "end": v(-11.5, -24.36) * mm});
            skLineSegment(sketch, "E1155", {"start": v(-11.5, -24.36) * mm, "end": v(-11.61, -24.37) * mm});
            skLineSegment(sketch, "E1156", {"start": v(-11.61, -24.37) * mm, "end": v(-11.63, -24.37) * mm});
            skLineSegment(sketch, "E1157", {"start": v(-11.63, -24.37) * mm, "end": v(-11.8, -24.39) * mm});
            skLineSegment(sketch, "E1158", {"start": v(-11.8, -24.39) * mm, "end": v(-12.95, -23.4) * mm});
            skLineSegment(sketch, "E1159", {"start": v(-12.95, -23.4) * mm, "end": v(-13.09, -23.49) * mm});
            skLineSegment(sketch, "E1160", {"start": v(-13.09, -23.49) * mm, "end": v(-13.1, -23.5) * mm});
            skLineSegment(sketch, "E1161", {"start": v(-13.1, -23.5) * mm, "end": v(-13.18, -23.54) * mm});
            skLineSegment(sketch, "E1162", {"start": v(-13.18, -23.54) * mm, "end": v(-13.25, -23.57) * mm});
            skLineSegment(sketch, "E1163", {"start": v(-13.25, -23.57) * mm, "end": v(-13.3, -23.56) * mm});
            skLineSegment(sketch, "E1164", {"start": v(-13.3, -23.56) * mm, "end": v(-13.34, -23.54) * mm});
            skLineSegment(sketch, "E1165", {"start": v(-13.34, -23.54) * mm, "end": v(-13.34, -23.53) * mm});
            skLineSegment(sketch, "E1166", {"start": v(-13.34, -23.53) * mm, "end": v(-13.35, -23.52) * mm});
            skLineSegment(sketch, "E1167", {"start": v(-13.35, -23.52) * mm, "end": v(-13.38, -23.48) * mm});
            skLineSegment(sketch, "E1168", {"start": v(-13.38, -23.48) * mm, "end": v(-13.45, -23.4) * mm});
            skLineSegment(sketch, "E1169", {"start": v(-13.45, -23.4) * mm, "end": v(-13.55, -23.3) * mm});
            skLineSegment(sketch, "E1170", {"start": v(-13.55, -23.3) * mm, "end": v(-13.63, -23.2) * mm});
            skLineSegment(sketch, "E1171", {"start": v(-13.63, -23.2) * mm, "end": v(-13.66, -23.17) * mm});
            skLineSegment(sketch, "E1172", {"start": v(-13.66, -23.17) * mm, "end": v(-13.7, -23.14) * mm});
            skLineSegment(sketch, "E1173", {"start": v(-13.7, -23.14) * mm, "end": v(-13.78, -23.05) * mm});
            skLineSegment(sketch, "E1174", {"start": v(-13.78, -23.05) * mm, "end": v(-13.87, -22.95) * mm});
            skLineSegment(sketch, "E1175", {"start": v(-13.87, -22.95) * mm, "end": v(-13.94, -22.87) * mm});
            skLineSegment(sketch, "E1176", {"start": v(-13.94, -22.87) * mm, "end": v(-13.96, -22.85) * mm});
            skLineSegment(sketch, "E1177", {"start": v(-13.96, -22.85) * mm, "end": v(-13.96, -22.84) * mm});
            skLineSegment(sketch, "E1178", {"start": v(-13.96, -22.84) * mm, "end": v(-13.96, -22.83) * mm});
            skLineSegment(sketch, "E1179", {"start": v(-13.96, -22.83) * mm, "end": v(-13.95, -22.82) * mm});
            skLineSegment(sketch, "E1180", {"start": v(-13.95, -22.82) * mm, "end": v(-13.91, -22.78) * mm});
            skLineSegment(sketch, "E1181", {"start": v(-13.91, -22.78) * mm, "end": v(-13.87, -22.74) * mm});
            skLineSegment(sketch, "E1182", {"start": v(-13.87, -22.74) * mm, "end": v(-13.82, -22.7) * mm});
            skLineSegment(sketch, "E1183", {"start": v(-13.82, -22.7) * mm, "end": v(-13.8, -22.69) * mm});
            skLineSegment(sketch, "E1184", {"start": v(-13.8, -22.69) * mm, "end": v(-13.66, -22.56) * mm});
            skLineSegment(sketch, "E1185", {"start": v(-13.66, -22.56) * mm, "end": v(-13.77, -22.41) * mm});
            skLineSegment(sketch, "E1186", {"start": v(-13.77, -22.41) * mm, "end": v(-13.8, -22.38) * mm});
            skLineSegment(sketch, "E1187", {"start": v(-13.8, -22.38) * mm, "end": v(-13.87, -22.27) * mm});
            skLineSegment(sketch, "E1188", {"start": v(-13.87, -22.27) * mm, "end": v(-13.91, -22.17) * mm});
            skLineSegment(sketch, "E1189", {"start": v(-13.91, -22.17) * mm, "end": v(-13.9, -22.1) * mm});
            skLineSegment(sketch, "E1190", {"start": v(-13.9, -22.1) * mm, "end": v(-13.86, -22.04) * mm});
            skLineSegment(sketch, "E1191", {"start": v(-13.86, -22.04) * mm, "end": v(-13.84, -22.02) * mm});
            skLineSegment(sketch, "E1192", {"start": v(-13.84, -22.02) * mm, "end": v(-13.83, -22.01) * mm});
            skLineSegment(sketch, "E1193", {"start": v(-13.83, -22.01) * mm, "end": v(-13.78, -21.96) * mm});
            skLineSegment(sketch, "E1194", {"start": v(-13.78, -21.96) * mm, "end": v(-13.76, -21.9) * mm});
            skLineSegment(sketch, "E1195", {"start": v(-13.76, -21.9) * mm, "end": v(-13.76, -21.89) * mm});
            skLineSegment(sketch, "E1196", {"start": v(-13.76, -21.89) * mm, "end": v(-13.76, -21.88) * mm});
            skLineSegment(sketch, "E1197", {"start": v(-13.76, -21.88) * mm, "end": v(-13.76, -21.86) * mm});
            skLineSegment(sketch, "E1198", {"start": v(-13.76, -21.86) * mm, "end": v(-13.77, -21.84) * mm});
            skLineSegment(sketch, "E1199", {"start": v(-13.77, -21.84) * mm, "end": v(-13.8, -21.84) * mm});
            skLineSegment(sketch, "E1200", {"start": v(-13.8, -21.84) * mm, "end": v(-13.84, -21.84) * mm});
            skLineSegment(sketch, "E1201", {"start": v(-13.84, -21.84) * mm, "end": v(-13.85, -21.85) * mm});
            skLineSegment(sketch, "E1202", {"start": v(-13.85, -21.85) * mm, "end": v(-13.86, -21.85) * mm});
            skLineSegment(sketch, "E1203", {"start": v(-13.86, -21.85) * mm, "end": v(-13.93, -21.88) * mm});
            skLineSegment(sketch, "E1204", {"start": v(-13.93, -21.88) * mm, "end": v(-14, -21.9) * mm});
            skLineSegment(sketch, "E1205", {"start": v(-14, -21.9) * mm, "end": v(-14, -21.91) * mm});
            skLineSegment(sketch, "E1206", {"start": v(-14, -21.91) * mm, "end": v(-14.02, -21.92) * mm});
            skLineSegment(sketch, "E1207", {"start": v(-14.02, -21.92) * mm, "end": v(-14.06, -21.95) * mm});
            skLineSegment(sketch, "E1208", {"start": v(-14.06, -21.95) * mm, "end": v(-14.09, -21.96) * mm});
            skLineSegment(sketch, "E1209", {"start": v(-14.09, -21.96) * mm, "end": v(-14.1, -21.96) * mm});
            skLineSegment(sketch, "E1210", {"start": v(-14.1, -21.96) * mm, "end": v(-14.1, -21.96) * mm});
            skLineSegment(sketch, "E1211", {"start": v(-14.1, -21.96) * mm, "end": v(-14.13, -21.93) * mm});
            skLineSegment(sketch, "E1212", {"start": v(-14.13, -21.93) * mm, "end": v(-14.2, -21.84) * mm});
            skLineSegment(sketch, "E1213", {"start": v(-14.2, -21.84) * mm, "end": v(-14.3, -21.72) * mm});
            skLineSegment(sketch, "E1214", {"start": v(-14.3, -21.72) * mm, "end": v(-14.4, -21.6) * mm});
            skLineSegment(sketch, "E1215", {"start": v(-14.4, -21.6) * mm, "end": v(-14.43, -21.56) * mm});
            skLineSegment(sketch, "E1216", {"start": v(-14.43, -21.56) * mm, "end": v(-14.46, -21.52) * mm});
            skLineSegment(sketch, "E1217", {"start": v(-14.46, -21.52) * mm, "end": v(-14.57, -21.38) * mm});
            skLineSegment(sketch, "E1218", {"start": v(-14.57, -21.38) * mm, "end": v(-14.73, -21.18) * mm});
            skLineSegment(sketch, "E1219", {"start": v(-14.73, -21.18) * mm, "end": v(-14.88, -20.99) * mm});
            skLineSegment(sketch, "E1220", {"start": v(-14.88, -20.99) * mm, "end": v(-14.98, -20.86) * mm});
            skLineSegment(sketch, "E1221", {"start": v(-14.98, -20.86) * mm, "end": v(-15, -20.82) * mm});
            skLineSegment(sketch, "E1222", {"start": v(-15, -20.82) * mm, "end": v(-15.05, -20.76) * mm});
            skLineSegment(sketch, "E1223", {"start": v(-15.05, -20.76) * mm, "end": v(-15.19, -20.6) * mm});
            skLineSegment(sketch, "E1224", {"start": v(-15.19, -20.6) * mm, "end": v(-15.33, -20.41) * mm});
            skLineSegment(sketch, "E1225", {"start": v(-15.33, -20.41) * mm, "end": v(-15.43, -20.28) * mm});
            skLineSegment(sketch, "E1226", {"start": v(-15.43, -20.28) * mm, "end": v(-15.5, -20.18) * mm});
            skLineSegment(sketch, "E1227", {"start": v(-15.5, -20.18) * mm, "end": v(-15.56, -20.1) * mm});
            skLineSegment(sketch, "E1228", {"start": v(-15.56, -20.1) * mm, "end": v(-15.58, -20.06) * mm});
            skLineSegment(sketch, "E1229", {"start": v(-15.58, -20.06) * mm, "end": v(-15.6, -20.03) * mm});
            skLineSegment(sketch, "E1230", {"start": v(-15.6, -20.03) * mm, "end": v(-15.6, -20.02) * mm});
            skLineSegment(sketch, "E1231", {"start": v(-15.6, -20.02) * mm, "end": v(-15.6, -20.02) * mm});
            skLineSegment(sketch, "E1232", {"start": v(-15.6, -20.02) * mm, "end": v(-15.59, -20.02) * mm});
            skLineSegment(sketch, "E1233", {"start": v(-15.59, -20.02) * mm, "end": v(-15.57, -20) * mm});
            skLineSegment(sketch, "E1234", {"start": v(-15.57, -20) * mm, "end": v(-15.52, -19.96) * mm});
            skLineSegment(sketch, "E1235", {"start": v(-15.52, -19.96) * mm, "end": v(-15.45, -19.91) * mm});
            skLineSegment(sketch, "E1236", {"start": v(-15.45, -19.91) * mm, "end": v(-15.38, -19.87) * mm});
            skLineSegment(sketch, "E1237", {"start": v(-15.38, -19.87) * mm, "end": v(-15.36, -19.86) * mm});
            skLineSegment(sketch, "E1238", {"start": v(-15.36, -19.86) * mm, "end": v(-15.33, -19.84) * mm});
            skLineSegment(sketch, "E1239", {"start": v(-15.33, -19.84) * mm, "end": v(-15.22, -19.77) * mm});
            skLineSegment(sketch, "E1240", {"start": v(-15.22, -19.77) * mm, "end": v(-15, -19.63) * mm});
            skLineSegment(sketch, "E1241", {"start": v(-15, -19.63) * mm, "end": v(-14.7, -19.46) * mm});
            skLineSegment(sketch, "E1242", {"start": v(-14.7, -19.46) * mm, "end": v(-14.47, -19.31) * mm});
            skLineSegment(sketch, "E1243", {"start": v(-14.47, -19.31) * mm, "end": v(-14.4, -19.26) * mm});
            skLineSegment(sketch, "E1244", {"start": v(-14.4, -19.26) * mm, "end": v(-14.32, -19.21) * mm});
            skLineSegment(sketch, "E1245", {"start": v(-14.32, -19.21) * mm, "end": v(-14.08, -19.07) * mm});
            skLineSegment(sketch, "E1246", {"start": v(-14.08, -19.07) * mm, "end": v(-13.77, -18.88) * mm});
            skLineSegment(sketch, "E1247", {"start": v(-13.77, -18.88) * mm, "end": v(-13.51, -18.72) * mm});
            skLineSegment(sketch, "E1248", {"start": v(-13.51, -18.72) * mm, "end": v(-13.38, -18.64) * mm});
            skLineSegment(sketch, "E1249", {"start": v(-13.38, -18.64) * mm, "end": v(-13.34, -18.6) * mm});
            skLineSegment(sketch, "E1250", {"start": v(-13.34, -18.6) * mm, "end": v(-13.3, -18.59) * mm});
            skLineSegment(sketch, "E1251", {"start": v(-13.3, -18.59) * mm, "end": v(-13.2, -18.53) * mm});
            skLineSegment(sketch, "E1252", {"start": v(-13.2, -18.53) * mm, "end": v(-13.07, -18.44) * mm});
            skLineSegment(sketch, "E1253", {"start": v(-13.07, -18.44) * mm, "end": v(-12.94, -18.36) * mm});
            skLineSegment(sketch, "E1254", {"start": v(-12.94, -18.36) * mm, "end": v(-12.87, -18.32) * mm});
            skLineSegment(sketch, "E1255", {"start": v(-12.87, -18.32) * mm, "end": v(-12.84, -18.3) * mm});
            skLineSegment(sketch, "E1256", {"start": v(-12.84, -18.3) * mm, "end": v(-12.82, -18.29) * mm});
            skLineSegment(sketch, "E1257", {"start": v(-12.82, -18.29) * mm, "end": v(-12.76, -18.25) * mm});
            skLineSegment(sketch, "E1258", {"start": v(-12.76, -18.25) * mm, "end": v(-12.66, -18.19) * mm});
            skLineSegment(sketch, "E1259", {"start": v(-12.66, -18.19) * mm, "end": v(-12.56, -18.13) * mm});
            skLineSegment(sketch, "E1260", {"start": v(-12.56, -18.13) * mm, "end": v(-12.5, -18.09) * mm});
            skLineSegment(sketch, "E1261", {"start": v(-12.5, -18.09) * mm, "end": v(-12.47, -18.08) * mm});
            skLineSegment(sketch, "E1262", {"start": v(-12.47, -18.08) * mm, "end": v(-12.45, -18.06) * mm});
            skLineSegment(sketch, "E1263", {"start": v(-12.45, -18.06) * mm, "end": v(-12.36, -18) * mm});
            skLineSegment(sketch, "E1264", {"start": v(-12.36, -18) * mm, "end": v(-12.2, -17.9) * mm});
            skLineSegment(sketch, "E1265", {"start": v(-12.2, -17.9) * mm, "end": v(-11.98, -17.77) * mm});
            skLineSegment(sketch, "E1266", {"start": v(-11.98, -17.77) * mm, "end": v(-11.81, -17.67) * mm});
            skLineSegment(sketch, "E1267", {"start": v(-11.81, -17.67) * mm, "end": v(-11.76, -17.63) * mm});
            skLineSegment(sketch, "E1268", {"start": v(-11.76, -17.63) * mm, "end": v(-11.7, -17.6) * mm});
            skLineSegment(sketch, "E1269", {"start": v(-11.7, -17.6) * mm, "end": v(-11.54, -17.5) * mm});
            skLineSegment(sketch, "E1270", {"start": v(-11.54, -17.5) * mm, "end": v(-11.33, -17.36) * mm});
            skLineSegment(sketch, "E1271", {"start": v(-11.33, -17.36) * mm, "end": v(-11.16, -17.26) * mm});
            skLineSegment(sketch, "E1272", {"start": v(-11.16, -17.26) * mm, "end": v(-11.08, -17.2) * mm});
            skLineSegment(sketch, "E1273", {"start": v(-11.08, -17.2) * mm, "end": v(-11.05, -17.2) * mm});
            skLineSegment(sketch, "E1274", {"start": v(-11.05, -17.2) * mm, "end": v(-10.9, -17.1) * mm});
            skLineSegment(sketch, "E1275", {"start": v(-10.9, -17.1) * mm, "end": v(-10.44, -16.82) * mm});
            skLineSegment(sketch, "E1276", {"start": v(-10.44, -16.82) * mm, "end": v(-9.92, -16.5) * mm});
            skLineSegment(sketch, "E1277", {"start": v(-9.92, -16.5) * mm, "end": v(-9.48, -16.21) * mm});
            skLineSegment(sketch, "E1278", {"start": v(-9.48, -16.21) * mm, "end": v(-9.1, -15.96) * mm});
            skLineSegment(sketch, "E1279", {"start": v(-9.1, -15.96) * mm, "end": v(-8.75, -15.73) * mm});
            skLineSegment(sketch, "E1280", {"start": v(-8.75, -15.73) * mm, "end": v(-8.42, -15.5) * mm});
            skLineSegment(sketch, "E1281", {"start": v(-8.42, -15.5) * mm, "end": v(-8.1, -15.25) * mm});
            skLineSegment(sketch, "E1282", {"start": v(-8.1, -15.25) * mm, "end": v(-7.85, -15.06) * mm});
            skLineSegment(sketch, "E1283", {"start": v(-7.85, -15.06) * mm, "end": v(-7.76, -15) * mm});
            skLineSegment(sketch, "E1284", {"start": v(-7.76, -15) * mm, "end": v(-7.75, -14.98) * mm});
            skLineSegment(sketch, "E1285", {"start": v(-7.75, -14.98) * mm, "end": v(-7.68, -14.93) * mm});
            skLineSegment(sketch, "E1286", {"start": v(-7.68, -14.93) * mm, "end": v(-7.54, -14.82) * mm});
            skLineSegment(sketch, "E1287", {"start": v(-7.54, -14.82) * mm, "end": v(-7.36, -14.68) * mm});
            skLineSegment(sketch, "E1288", {"start": v(-7.36, -14.68) * mm, "end": v(-7.2, -14.56) * mm});
            skLineSegment(sketch, "E1289", {"start": v(-7.2, -14.56) * mm, "end": v(-7.16, -14.52) * mm});
            skLineSegment(sketch, "E1290", {"start": v(-7.16, -14.52) * mm, "end": v(-7.1, -14.48) * mm});
            skLineSegment(sketch, "E1291", {"start": v(-7.1, -14.48) * mm, "end": v(-6.94, -14.36) * mm});
            skLineSegment(sketch, "E1292", {"start": v(-6.94, -14.36) * mm, "end": v(-6.77, -14.23) * mm});
            skLineSegment(sketch, "E1293", {"start": v(-6.77, -14.23) * mm, "end": v(-6.63, -14.14) * mm});
            skLineSegment(sketch, "E1294", {"start": v(-6.63, -14.14) * mm, "end": v(-6.52, -14.07) * mm});
            skLineSegment(sketch, "E1295", {"start": v(-6.52, -14.07) * mm, "end": v(-6.41, -14.03) * mm});
            skLineSegment(sketch, "E1296", {"start": v(-6.41, -14.03) * mm, "end": v(-6.32, -14.01) * mm});
            skLineSegment(sketch, "E1297", {"start": v(-6.32, -14.01) * mm, "end": v(-6.2, -14) * mm});
            skLineSegment(sketch, "E1298", {"start": v(-6.2, -14) * mm, "end": v(-6.12, -14) * mm});
            skLineSegment(sketch, "E1299", {"start": v(-6.12, -14) * mm, "end": v(-6.09, -14.01) * mm});
            skLineSegment(sketch, "E1300", {"start": v(-6.09, -14.01) * mm, "end": v(-6.06, -14.01) * mm});
            skLineSegment(sketch, "E1301", {"start": v(-6.06, -14.01) * mm, "end": v(-5.97, -14.02) * mm});
            skLineSegment(sketch, "E1302", {"start": v(-5.97, -14.02) * mm, "end": v(-5.86, -14.04) * mm});
            skLineSegment(sketch, "E1303", {"start": v(-5.86, -14.04) * mm, "end": v(-5.75, -14.06) * mm});
            skLineSegment(sketch, "E1304", {"start": v(-5.75, -14.06) * mm, "end": v(-5.62, -14.1) * mm});
            skLineSegment(sketch, "E1305", {"start": v(-5.62, -14.1) * mm, "end": v(-5.47, -14.15) * mm});
            skLineSegment(sketch, "E1306", {"start": v(-5.47, -14.15) * mm, "end": v(-5.3, -14.22) * mm});
            skLineSegment(sketch, "E1307", {"start": v(-5.3, -14.22) * mm, "end": v(-5.08, -14.3) * mm});
            skLineSegment(sketch, "E1308", {"start": v(-5.08, -14.3) * mm, "end": v(-4.88, -14.38) * mm});
            skLineSegment(sketch, "E1309", {"start": v(-4.88, -14.38) * mm, "end": v(-4.81, -14.4) * mm});
            skLineSegment(sketch, "E1310", {"start": v(-4.81, -14.4) * mm, "end": v(-4.7, -14.46) * mm});
            skLineSegment(sketch, "E1311", {"start": v(-4.7, -14.46) * mm, "end": v(-4.33, -14.6) * mm});
            skLineSegment(sketch, "E1312", {"start": v(-4.33, -14.6) * mm, "end": v(-3.8, -14.82) * mm});
            skLineSegment(sketch, "E1313", {"start": v(-3.8, -14.82) * mm, "end": v(-3.24, -15.06) * mm});
            skLineSegment(sketch, "E1314", {"start": v(-3.24, -15.06) * mm, "end": v(-2.77, -15.25) * mm});
            skLineSegment(sketch, "E1315", {"start": v(-2.77, -15.25) * mm, "end": v(-2.6, -15.31) * mm});
            skLineSegment(sketch, "E1316", {"start": v(-2.6, -15.31) * mm, "end": v(-2.54, -15.34) * mm});
            skLineSegment(sketch, "E1317", {"start": v(-2.54, -15.34) * mm, "end": v(-2.34, -15.42) * mm});
            skLineSegment(sketch, "E1318", {"start": v(-2.34, -15.42) * mm, "end": v(-2.03, -15.55) * mm});
            skLineSegment(sketch, "E1319", {"start": v(-2.03, -15.55) * mm, "end": v(-1.7, -15.68) * mm});
            skLineSegment(sketch, "E1320", {"start": v(-1.7, -15.68) * mm, "end": v(-1.49, -15.77) * mm});
            skLineSegment(sketch, "E1321", {"start": v(-1.49, -15.77) * mm, "end": v(-1.42, -15.8) * mm});
            skLineSegment(sketch, "E1322", {"start": v(-1.42, -15.8) * mm, "end": v(-1.36, -15.82) * mm});
            skLineSegment(sketch, "E1323", {"start": v(-1.36, -15.82) * mm, "end": v(-1.18, -15.9) * mm});
            skLineSegment(sketch, "E1324", {"start": v(-1.18, -15.9) * mm, "end": v(-1.01, -15.96) * mm});
            skLineSegment(sketch, "E1325", {"start": v(-1.01, -15.96) * mm, "end": v(-0.88, -16) * mm});
            skLineSegment(sketch, "E1326", {"start": v(-0.88, -16) * mm, "end": v(-0.79, -16.02) * mm});
            skLineSegment(sketch, "E1327", {"start": v(-0.79, -16.02) * mm, "end": v(-0.7, -16.01) * mm});
            skLineSegment(sketch, "E1328", {"start": v(-0.7, -16.01) * mm, "end": v(-0.62, -15.98) * mm});
            skLineSegment(sketch, "E1329", {"start": v(-0.62, -15.98) * mm, "end": v(-0.52, -15.92) * mm});
            skLineSegment(sketch, "E1330", {"start": v(-0.52, -15.92) * mm, "end": v(-0.43, -15.86) * mm});
            skLineSegment(sketch, "E1331", {"start": v(-0.43, -15.86) * mm, "end": v(-0.4, -15.84) * mm});
            skLineSegment(sketch, "E1332", {"start": v(-0.4, -15.84) * mm, "end": v(-0.38, -15.83) * mm});
            skLineSegment(sketch, "E1333", {"start": v(-0.38, -15.83) * mm, "end": v(-0.33, -15.8) * mm});
            skLineSegment(sketch, "E1334", {"start": v(-0.33, -15.8) * mm, "end": v(-0.27, -15.77) * mm});
            skLineSegment(sketch, "E1335", {"start": v(-0.27, -15.77) * mm, "end": v(-0.23, -15.75) * mm});
            skLineSegment(sketch, "E1336", {"start": v(-0.23, -15.75) * mm, "end": v(-0.18, -15.75) * mm});
            skLineSegment(sketch, "E1337", {"start": v(-0.18, -15.75) * mm, "end": v(-0.13, -15.76) * mm});
            skLineSegment(sketch, "E1338", {"start": v(-0.13, -15.76) * mm, "end": v(-0.07, -15.79) * mm});
            skLineSegment(sketch, "E1339", {"start": v(-0.07, -15.79) * mm, "end": v(0.02, -15.83) * mm});
            skLineSegment(sketch, "E1340", {"start": v(0.02, -15.83) * mm, "end": v(0.1, -15.87) * mm});
            skLineSegment(sketch, "E1341", {"start": v(0.1, -15.87) * mm, "end": v(0.12, -15.89) * mm});
            skLineSegment(sketch, "E1342", {"start": v(0.12, -15.89) * mm, "end": v(0.16, -15.91) * mm});
            skLineSegment(sketch, "E1343", {"start": v(0.16, -15.91) * mm, "end": v(0.27, -15.97) * mm});
            skLineSegment(sketch, "E1344", {"start": v(0.27, -15.97) * mm, "end": v(0.39, -16) * mm});
            skLineSegment(sketch, "E1345", {"start": v(0.39, -16) * mm, "end": v(0.54, -15.95) * mm});
            skLineSegment(sketch, "E1346", {"start": v(0.54, -15.95) * mm, "end": v(0.73, -15.86) * mm});
            skLineSegment(sketch, "E1347", {"start": v(0.73, -15.86) * mm, "end": v(0.8, -15.83) * mm});
            skLineSegment(sketch, "E1348", {"start": v(0.8, -15.83) * mm, "end": v(0.84, -15.81) * mm});
            skLineSegment(sketch, "E1349", {"start": v(0.84, -15.81) * mm, "end": v(0.98, -15.75) * mm});
            skLineSegment(sketch, "E1350", {"start": v(0.98, -15.75) * mm, "end": v(1.25, -15.63) * mm});
            skLineSegment(sketch, "E1351", {"start": v(1.25, -15.63) * mm, "end": v(1.57, -15.48) * mm});
            skLineSegment(sketch, "E1352", {"start": v(1.57, -15.48) * mm, "end": v(1.82, -15.37) * mm});
            skLineSegment(sketch, "E1353", {"start": v(1.82, -15.37) * mm, "end": v(1.9, -15.33) * mm});
            skLineSegment(sketch, "E1354", {"start": v(1.9, -15.33) * mm, "end": v(2, -15.3) * mm});
            skLineSegment(sketch, "E1355", {"start": v(2, -15.3) * mm, "end": v(2.24, -15.18) * mm});
            skLineSegment(sketch, "E1356", {"start": v(2.24, -15.18) * mm, "end": v(2.56, -15.04) * mm});
            skLineSegment(sketch, "E1357", {"start": v(2.56, -15.04) * mm, "end": v(2.82, -14.92) * mm});
            skLineSegment(sketch, "E1358", {"start": v(2.82, -14.92) * mm, "end": v(2.96, -14.86) * mm});
            skLineSegment(sketch, "E1359", {"start": v(2.96, -14.86) * mm, "end": v(3, -14.84) * mm});
            skLineSegment(sketch, "E1360", {"start": v(3, -14.84) * mm, "end": v(3.02, -14.83) * mm});
            skLineSegment(sketch, "E1361", {"start": v(3.02, -14.83) * mm, "end": v(3.1, -14.79) * mm});
            skLineSegment(sketch, "E1362", {"start": v(3.1, -14.79) * mm, "end": v(3.2, -14.75) * mm});
            skLineSegment(sketch, "E1363", {"start": v(3.2, -14.75) * mm, "end": v(3.26, -14.72) * mm});
            skLineSegment(sketch, "E1364", {"start": v(3.26, -14.72) * mm, "end": v(3.28, -14.7) * mm});
            skLineSegment(sketch, "E1365", {"start": v(3.28, -14.7) * mm, "end": v(3.29, -14.7) * mm});
            skLineSegment(sketch, "E1366", {"start": v(3.29, -14.7) * mm, "end": v(3.3, -14.7) * mm});
            skLineSegment(sketch, "E1367", {"start": v(3.3, -14.7) * mm, "end": v(3.32, -14.7) * mm});
            skLineSegment(sketch, "E1368", {"start": v(3.32, -14.7) * mm, "end": v(3.4, -14.66) * mm});
            skLineSegment(sketch, "E1369", {"start": v(3.4, -14.66) * mm, "end": v(3.5, -14.61) * mm});
            skLineSegment(sketch, "E1370", {"start": v(3.5, -14.61) * mm, "end": v(3.6, -14.57) * mm});
            skLineSegment(sketch, "E1371", {"start": v(3.6, -14.57) * mm, "end": v(3.63, -14.55) * mm});
            skLineSegment(sketch, "E1372", {"start": v(3.63, -14.55) * mm, "end": v(3.66, -14.54) * mm});
            skLineSegment(sketch, "E1373", {"start": v(3.66, -14.54) * mm, "end": v(3.77, -14.48) * mm});
            skLineSegment(sketch, "E1374", {"start": v(3.77, -14.48) * mm, "end": v(3.93, -14.41) * mm});
            skLineSegment(sketch, "E1375", {"start": v(3.93, -14.41) * mm, "end": v(4.08, -14.34) * mm});
            skLineSegment(sketch, "E1376", {"start": v(4.08, -14.34) * mm, "end": v(4.18, -14.3) * mm});
            skLineSegment(sketch, "E1377", {"start": v(4.18, -14.3) * mm, "end": v(4.2, -14.29) * mm});
            skLineSegment(sketch, "E1378", {"start": v(4.2, -14.29) * mm, "end": v(4.24, -14.27) * mm});
            skLineSegment(sketch, "E1379", {"start": v(4.24, -14.27) * mm, "end": v(4.47, -14.17) * mm});
            skLineSegment(sketch, "E1380", {"start": v(4.47, -14.17) * mm, "end": v(4.71, -14.06) * mm});
            skLineSegment(sketch, "E1381", {"start": v(4.71, -14.06) * mm, "end": v(4.75, -14.04) * mm});
            skLineSegment(sketch, "E1382", {"start": v(4.75, -14.04) * mm, "end": v(4.85, -14) * mm});
            skLineSegment(sketch, "E1383", {"start": v(4.85, -14) * mm, "end": v(5.14, -13.89) * mm});
            skLineSegment(sketch, "E1384", {"start": v(5.14, -13.89) * mm, "end": v(5.5, -13.8) * mm});
            skLineSegment(sketch, "E1385", {"start": v(5.5, -13.8) * mm, "end": v(5.82, -13.77) * mm});
            skLineSegment(sketch, "E1386", {"start": v(5.82, -13.77) * mm, "end": v(6.01, -13.8) * mm});
            skLineSegment(sketch, "E1387", {"start": v(6.01, -13.8) * mm, "end": v(6.07, -13.81) * mm});
            skLineSegment(sketch, "E1388", {"start": v(6.07, -13.81) * mm, "end": v(6.08, -13.82) * mm});
            skLineSegment(sketch, "E1389", {"start": v(6.08, -13.82) * mm, "end": v(6.13, -13.85) * mm});
            skLineSegment(sketch, "E1390", {"start": v(6.13, -13.85) * mm, "end": v(6.23, -13.91) * mm});
            skLineSegment(sketch, "E1391", {"start": v(6.23, -13.91) * mm, "end": v(6.35, -14) * mm});
            skLineSegment(sketch, "E1392", {"start": v(6.35, -14) * mm, "end": v(6.44, -14.06) * mm});
            skLineSegment(sketch, "E1393", {"start": v(6.44, -14.06) * mm, "end": v(6.47, -14.08) * mm});
            skLineSegment(sketch, "E1394", {"start": v(6.47, -14.08) * mm, "end": v(6.6, -14.18) * mm});
            skLineSegment(sketch, "E1395", {"start": v(6.6, -14.18) * mm, "end": v(7.01, -14.47) * mm});
            skLineSegment(sketch, "E1396", {"start": v(7.01, -14.47) * mm, "end": v(7.5, -14.82) * mm});
            skLineSegment(sketch, "E1397", {"start": v(7.5, -14.82) * mm, "end": v(7.93, -15.12) * mm});
            skLineSegment(sketch, "E1398", {"start": v(7.93, -15.12) * mm, "end": v(8.35, -15.4) * mm});
            skLineSegment(sketch, "E1399", {"start": v(8.35, -15.4) * mm, "end": v(8.76, -15.66) * mm});
            skLineSegment(sketch, "E1400", {"start": v(8.76, -15.66) * mm, "end": v(9.17, -15.92) * mm});
            skLineSegment(sketch, "E1401", {"start": v(9.17, -15.92) * mm, "end": v(9.6, -16.18) * mm});
            skLineSegment(sketch, "E1402", {"start": v(9.6, -16.18) * mm, "end": v(9.97, -16.38) * mm});
            skLineSegment(sketch, "E1403", {"start": v(9.97, -16.38) * mm, "end": v(10.08, -16.45) * mm});
            skLineSegment(sketch, "E1404", {"start": v(10.08, -16.45) * mm, "end": v(10.2, -16.52) * mm});
            skLineSegment(sketch, "E1405", {"start": v(10.2, -16.52) * mm, "end": v(10.55, -16.72) * mm});
            skLineSegment(sketch, "E1406", {"start": v(10.55, -16.72) * mm, "end": v(11.1, -17.02) * mm});
            skLineSegment(sketch, "E1407", {"start": v(11.1, -17.02) * mm, "end": v(11.63, -17.34) * mm});
            skLineSegment(sketch, "E1408", {"start": v(11.63, -17.34) * mm, "end": v(12, -17.54) * mm});
            skLineSegment(sketch, "E1409", {"start": v(12, -17.54) * mm, "end": v(12.12, -17.61) * mm});
            skLineSegment(sketch, "E1410", {"start": v(12.12, -17.61) * mm, "end": v(12.17, -17.64) * mm});
            skLineSegment(sketch, "E1411", {"start": v(12.17, -17.64) * mm, "end": v(12.33, -17.73) * mm});
            skLineSegment(sketch, "E1412", {"start": v(12.33, -17.73) * mm, "end": v(12.53, -17.85) * mm});
            skLineSegment(sketch, "E1413", {"start": v(12.53, -17.85) * mm, "end": v(12.72, -17.96) * mm});
            skLineSegment(sketch, "E1414", {"start": v(12.72, -17.96) * mm, "end": v(12.88, -18.05) * mm});
            skLineSegment(sketch, "E1415", {"start": v(12.88, -18.05) * mm, "end": v(13.02, -18.13) * mm});
            skLineSegment(sketch, "E1416", {"start": v(13.02, -18.13) * mm, "end": v(13.14, -18.2) * mm});
            skLineSegment(sketch, "E1417", {"start": v(13.14, -18.2) * mm, "end": v(13.22, -18.24) * mm});
            skLineSegment(sketch, "E1418", {"start": v(13.22, -18.24) * mm, "end": v(13.25, -18.26) * mm});
            skLineSegment(sketch, "E1419", {"start": v(13.25, -18.26) * mm, "end": v(13.26, -18.27) * mm});
            skLineSegment(sketch, "E1420", {"start": v(13.26, -18.27) * mm, "end": v(13.27, -18.27) * mm});
            skLineSegment(sketch, "E1421", {"start": v(13.27, -18.27) * mm, "end": v(13.34, -18.31) * mm});
            skLineSegment(sketch, "E1422", {"start": v(13.34, -18.31) * mm, "end": v(13.49, -18.4) * mm});
            skLineSegment(sketch, "E1423", {"start": v(13.49, -18.4) * mm, "end": v(13.68, -18.51) * mm});
            skLineSegment(sketch, "E1424", {"start": v(13.68, -18.51) * mm, "end": v(13.84, -18.6) * mm});
            skLineSegment(sketch, "E1425", {"start": v(13.84, -18.6) * mm, "end": v(13.9, -18.64) * mm});
            skLineSegment(sketch, "E1426", {"start": v(13.9, -18.64) * mm, "end": v(13.96, -18.67) * mm});
            skLineSegment(sketch, "E1427", {"start": v(13.96, -18.67) * mm, "end": v(14.14, -18.78) * mm});
            skLineSegment(sketch, "E1428", {"start": v(14.14, -18.78) * mm, "end": v(14.4, -18.93) * mm});
            skLineSegment(sketch, "E1429", {"start": v(14.4, -18.93) * mm, "end": v(14.66, -19.08) * mm});
            skLineSegment(sketch, "E1430", {"start": v(14.66, -19.08) * mm, "end": v(14.83, -19.17) * mm});
            skLineSegment(sketch, "E1431", {"start": v(14.83, -19.17) * mm, "end": v(14.88, -19.2) * mm});
            skLineSegment(sketch, "E1432", {"start": v(14.88, -19.2) * mm, "end": v(14.92, -19.22) * mm});
            skLineSegment(sketch, "E1433", {"start": v(14.92, -19.22) * mm, "end": v(15.05, -19.3) * mm});
            skLineSegment(sketch, "E1434", {"start": v(15.05, -19.3) * mm, "end": v(15.2, -19.39) * mm});
            skLineSegment(sketch, "E1435", {"start": v(15.2, -19.39) * mm, "end": v(15.29, -19.45) * mm});
            skLineSegment(sketch, "E1436", {"start": v(15.29, -19.45) * mm, "end": v(15.32, -19.47) * mm});
            skLineSegment(sketch, "E1437", {"start": v(15.32, -19.47) * mm, "end": v(15.32, -19.48) * mm});
            skLineSegment(sketch, "E1438", {"start": v(15.32, -19.48) * mm, "end": v(15.32, -19.49) * mm});
            skLineSegment(sketch, "E1439", {"start": v(15.32, -19.49) * mm, "end": v(15.31, -19.51) * mm});
            skLineSegment(sketch, "E1440", {"start": v(15.31, -19.51) * mm, "end": v(15.28, -19.57) * mm});
            skLineSegment(sketch, "E1441", {"start": v(15.28, -19.57) * mm, "end": v(15.23, -19.65) * mm});
            skLineSegment(sketch, "E1442", {"start": v(15.23, -19.65) * mm, "end": v(15.18, -19.71) * mm});
            skLineSegment(sketch, "E1443", {"start": v(15.18, -19.71) * mm, "end": v(15.17, -19.73) * mm});
            skLineSegment(sketch, "E1444", {"start": v(15.17, -19.73) * mm, "end": v(15.13, -19.78) * mm});
            skLineSegment(sketch, "E1445", {"start": v(15.13, -19.78) * mm, "end": v(15.04, -19.9) * mm});
            skLineSegment(sketch, "E1446", {"start": v(15.04, -19.9) * mm, "end": v(14.87, -20.14) * mm});
            skLineSegment(sketch, "E1447", {"start": v(14.87, -20.14) * mm, "end": v(14.67, -20.41) * mm});
            skLineSegment(sketch, "E1448", {"start": v(14.67, -20.41) * mm, "end": v(14.46, -20.7) * mm});
            skLineSegment(sketch, "E1449", {"start": v(14.46, -20.7) * mm, "end": v(14.26, -20.98) * mm});
            skLineSegment(sketch, "E1450", {"start": v(14.26, -20.98) * mm, "end": v(14.1, -21.21) * mm});
            skLineSegment(sketch, "E1451", {"start": v(14.1, -21.21) * mm, "end": v(13.98, -21.38) * mm});
            skLineSegment(sketch, "E1452", {"start": v(13.98, -21.38) * mm, "end": v(13.93, -21.44) * mm});
            skLineSegment(sketch, "E1453", {"start": v(13.93, -21.44) * mm, "end": v(13.93, -21.45) * mm});
            skLineSegment(sketch, "E1454", {"start": v(13.93, -21.45) * mm, "end": v(13.92, -21.45) * mm});
            skLineSegment(sketch, "E1455", {"start": v(13.92, -21.45) * mm, "end": v(13.9, -21.45) * mm});
            skLineSegment(sketch, "E1456", {"start": v(13.9, -21.45) * mm, "end": v(13.87, -21.44) * mm});
            skLineSegment(sketch, "E1457", {"start": v(13.87, -21.44) * mm, "end": v(13.81, -21.42) * mm});
            skLineSegment(sketch, "E1458", {"start": v(13.81, -21.42) * mm, "end": v(13.76, -21.4) * mm});
            skLineSegment(sketch, "E1459", {"start": v(13.76, -21.4) * mm, "end": v(13.75, -21.39) * mm});
            skLineSegment(sketch, "E1460", {"start": v(13.75, -21.39) * mm, "end": v(13.72, -21.38) * mm});
            skLineSegment(sketch, "E1461", {"start": v(13.72, -21.38) * mm, "end": v(13.65, -21.35) * mm});
            skLineSegment(sketch, "E1462", {"start": v(13.65, -21.35) * mm, "end": v(13.6, -21.34) * mm});
            skLineSegment(sketch, "E1463", {"start": v(13.6, -21.34) * mm, "end": v(13.57, -21.35) * mm});
            skLineSegment(sketch, "E1464", {"start": v(13.57, -21.35) * mm, "end": v(13.56, -21.37) * mm});
            skLineSegment(sketch, "E1465", {"start": v(13.56, -21.37) * mm, "end": v(13.55, -21.38) * mm});
            skLineSegment(sketch, "E1466", {"start": v(13.55, -21.38) * mm, "end": v(13.55, -21.39) * mm});
            skLineSegment(sketch, "E1467", {"start": v(13.55, -21.39) * mm, "end": v(13.56, -21.44) * mm});
            skLineSegment(sketch, "E1468", {"start": v(13.56, -21.44) * mm, "end": v(13.62, -21.51) * mm});
            skLineSegment(sketch, "E1469", {"start": v(13.62, -21.51) * mm, "end": v(13.64, -21.53) * mm});
            skLineSegment(sketch, "E1470", {"start": v(13.64, -21.53) * mm, "end": v(13.75, -21.62) * mm});
            skLineSegment(sketch, "E1471", {"start": v(13.75, -21.62) * mm, "end": v(13.7, -21.73) * mm});
            skLineSegment(sketch, "E1472", {"start": v(13.7, -21.73) * mm, "end": v(13.68, -21.74) * mm});
            skLineSegment(sketch, "E1473", {"start": v(13.68, -21.74) * mm, "end": v(13.63, -21.84) * mm});
            skLineSegment(sketch, "E1474", {"start": v(13.63, -21.84) * mm, "end": v(13.56, -21.94) * mm});
            skLineSegment(sketch, "E1475", {"start": v(13.56, -21.94) * mm, "end": v(13.55, -21.96) * mm});
            skLineSegment(sketch, "E1476", {"start": v(13.55, -21.96) * mm, "end": v(13.46, -22.07) * mm});
            skLineSegment(sketch, "E1477", {"start": v(13.46, -22.07) * mm, "end": v(13.55, -22.13) * mm});
            skLineSegment(sketch, "E1478", {"start": v(13.55, -22.13) * mm, "end": v(13.58, -22.15) * mm});
            skLineSegment(sketch, "E1479", {"start": v(13.58, -22.15) * mm, "end": v(13.68, -22.23) * mm});
            skLineSegment(sketch, "E1480", {"start": v(13.68, -22.23) * mm, "end": v(13.74, -22.29) * mm});
            skLineSegment(sketch, "E1481", {"start": v(13.74, -22.29) * mm, "end": v(13.77, -22.33) * mm});
            skLineSegment(sketch, "E1482", {"start": v(13.77, -22.33) * mm, "end": v(13.76, -22.36) * mm});
            skLineSegment(sketch, "E1483", {"start": v(13.76, -22.36) * mm, "end": v(13.76, -22.37) * mm});
            skLineSegment(sketch, "E1484", {"start": v(13.76, -22.37) * mm, "end": v(13.75, -22.38) * mm});
            skLineSegment(sketch, "E1485", {"start": v(13.75, -22.38) * mm, "end": v(13.73, -22.41) * mm});
            skLineSegment(sketch, "E1486", {"start": v(13.73, -22.41) * mm, "end": v(13.66, -22.49) * mm});
            skLineSegment(sketch, "E1487", {"start": v(13.66, -22.49) * mm, "end": v(13.58, -22.59) * mm});
            skLineSegment(sketch, "E1488", {"start": v(13.58, -22.59) * mm, "end": v(13.5, -22.67) * mm});
            skLineSegment(sketch, "E1489", {"start": v(13.5, -22.67) * mm, "end": v(13.48, -22.7) * mm});
            skLineSegment(sketch, "E1490", {"start": v(13.48, -22.7) * mm, "end": v(13.45, -22.73) * mm});
            skLineSegment(sketch, "E1491", {"start": v(13.45, -22.73) * mm, "end": v(13.37, -22.81) * mm});
            skLineSegment(sketch, "E1492", {"start": v(13.37, -22.81) * mm, "end": v(13.29, -22.91) * mm});
            skLineSegment(sketch, "E1493", {"start": v(13.29, -22.91) * mm, "end": v(13.22, -23) * mm});
            skLineSegment(sketch, "E1494", {"start": v(13.22, -23) * mm, "end": v(13.19, -23.03) * mm});
            skLineSegment(sketch, "E1495", {"start": v(13.19, -23.03) * mm, "end": v(13.18, -23.04) * mm});
            skLineSegment(sketch, "E1496", {"start": v(13.18, -23.04) * mm, "end": v(13.17, -23.05) * mm});
            skLineSegment(sketch, "E1497", {"start": v(13.17, -23.05) * mm, "end": v(13.14, -23.08) * mm});
            skLineSegment(sketch, "E1498", {"start": v(13.14, -23.08) * mm, "end": v(13.1, -23.1) * mm});
            skLineSegment(sketch, "E1499", {"start": v(13.1, -23.1) * mm, "end": v(13.03, -23.07) * mm});
            skLineSegment(sketch, "E1500", {"start": v(13.03, -23.07) * mm, "end": v(12.96, -23.03) * mm});
            skLineSegment(sketch, "E1501", {"start": v(12.96, -23.03) * mm, "end": v(12.94, -23.01) * mm});
            skLineSegment(sketch, "E1502", {"start": v(12.94, -23.01) * mm, "end": v(12.8, -22.92) * mm});
            skLineSegment(sketch, "E1503", {"start": v(12.8, -22.92) * mm, "end": v(12.66, -23.06) * mm});
            skLineSegment(sketch, "E1504", {"start": v(12.66, -23.06) * mm, "end": v(12.64, -23.08) * mm});
            skLineSegment(sketch, "E1505", {"start": v(12.64, -23.08) * mm, "end": v(12.57, -23.14) * mm});
            skLineSegment(sketch, "E1506", {"start": v(12.57, -23.14) * mm, "end": v(12.44, -23.26) * mm});
            skLineSegment(sketch, "E1507", {"start": v(12.44, -23.26) * mm, "end": v(12.28, -23.41) * mm});
            skLineSegment(sketch, "E1508", {"start": v(12.28, -23.41) * mm, "end": v(12.15, -23.53) * mm});
            skLineSegment(sketch, "E1509", {"start": v(12.15, -23.53) * mm, "end": v(12.1, -23.57) * mm});
            skLineSegment(sketch, "E1510", {"start": v(12.1, -23.57) * mm, "end": v(11.7, -23.95) * mm});
            skLineSegment(sketch, "E1511", {"start": v(11.7, -23.95) * mm, "end": v(11.48, -23.95) * mm});
            skLineSegment(sketch, "E1512", {"start": v(11.48, -23.95) * mm, "end": v(11.44, -23.94) * mm});
            skLineSegment(sketch, "E1513", {"start": v(11.44, -23.94) * mm, "end": v(11.32, -23.95) * mm});
            skLineSegment(sketch, "E1514", {"start": v(11.32, -23.95) * mm, "end": v(11.23, -23.98) * mm});
            skLineSegment(sketch, "E1515", {"start": v(11.23, -23.98) * mm, "end": v(11.22, -24.05) * mm});
            skLineSegment(sketch, "E1516", {"start": v(11.22, -24.05) * mm, "end": v(11.26, -24.12) * mm});
            skLineSegment(sketch, "E1517", {"start": v(11.26, -24.12) * mm, "end": v(11.28, -24.14) * mm});
            skLineSegment(sketch, "E1518", {"start": v(11.28, -24.14) * mm, "end": v(11.37, -24.25) * mm});
            skLineSegment(sketch, "E1519", {"start": v(11.37, -24.25) * mm, "end": v(11.22, -24.39) * mm});
            skLineSegment(sketch, "E1520", {"start": v(11.22, -24.39) * mm, "end": v(11.2, -24.4) * mm});
            skLineSegment(sketch, "E1521", {"start": v(11.2, -24.4) * mm, "end": v(11.13, -24.47) * mm});
            skLineSegment(sketch, "E1522", {"start": v(11.13, -24.47) * mm, "end": v(11, -24.58) * mm});
            skLineSegment(sketch, "E1523", {"start": v(11, -24.58) * mm, "end": v(10.86, -24.72) * mm});
            skLineSegment(sketch, "E1524", {"start": v(10.86, -24.72) * mm, "end": v(10.7, -24.87) * mm});
            skLineSegment(sketch, "E1525", {"start": v(10.7, -24.87) * mm, "end": v(10.54, -25.02) * mm});
            skLineSegment(sketch, "E1526", {"start": v(10.54, -25.02) * mm, "end": v(10.38, -25.17) * mm});
            skLineSegment(sketch, "E1527", {"start": v(10.38, -25.17) * mm, "end": v(10.23, -25.3) * mm});
            skLineSegment(sketch, "E1528", {"start": v(10.23, -25.3) * mm, "end": v(10.13, -25.4) * mm});
            skLineSegment(sketch, "E1529", {"start": v(10.13, -25.4) * mm, "end": v(10.1, -25.42) * mm});
            skLineSegment(sketch, "E1530", {"start": v(10.1, -25.42) * mm, "end": v(10.06, -25.46) * mm});
            skLineSegment(sketch, "E1531", {"start": v(10.06, -25.46) * mm, "end": v(9.94, -25.57) * mm});
            skLineSegment(sketch, "E1532", {"start": v(9.94, -25.57) * mm, "end": v(9.82, -25.69) * mm});
            skLineSegment(sketch, "E1533", {"start": v(9.82, -25.69) * mm, "end": v(9.73, -25.76) * mm});
            skLineSegment(sketch, "E1534", {"start": v(9.73, -25.76) * mm, "end": v(9.65, -25.82) * mm});
            skLineSegment(sketch, "E1535", {"start": v(9.65, -25.82) * mm, "end": v(9.6, -25.85) * mm});
            skLineSegment(sketch, "E1536", {"start": v(9.6, -25.85) * mm, "end": v(9.53, -25.86) * mm});
            skLineSegment(sketch, "E1537", {"start": v(9.53, -25.86) * mm, "end": v(9.47, -25.87) * mm});
            skLineSegment(sketch, "E1538", {"start": v(9.47, -25.87) * mm, "end": v(9.4, -25.87) * mm});
            skLineSegment(sketch, "E1539", {"start": v(9.4, -25.87) * mm, "end": v(9.39, -25.87) * mm});
            skLineSegment(sketch, "E1540", {"start": v(9.39, -25.87) * mm, "end": v(9.35, -25.87) * mm});
            skLineSegment(sketch, "E1541", {"start": v(9.35, -25.87) * mm, "end": v(9.22, -25.88) * mm});
            skLineSegment(sketch, "E1542", {"start": v(9.22, -25.88) * mm, "end": v(9.13, -25.92) * mm});
            skLineSegment(sketch, "E1543", {"start": v(9.13, -25.92) * mm, "end": v(9.12, -25.99) * mm});
            skLineSegment(sketch, "E1544", {"start": v(9.12, -25.99) * mm, "end": v(9.15, -26.07) * mm});
            skLineSegment(sketch, "E1545", {"start": v(9.15, -26.07) * mm, "end": v(9.17, -26.09) * mm});
            skLineSegment(sketch, "E1546", {"start": v(9.17, -26.09) * mm, "end": v(9.24, -26.2) * mm});
            skLineSegment(sketch, "E1547", {"start": v(9.24, -26.2) * mm, "end": v(8.99, -26.44) * mm});
            skLineSegment(sketch, "E1548", {"start": v(8.99, -26.44) * mm, "end": v(8.96, -26.46) * mm});
            skLineSegment(sketch, "E1549", {"start": v(8.96, -26.46) * mm, "end": v(8.87, -26.55) * mm});
            skLineSegment(sketch, "E1550", {"start": v(8.87, -26.55) * mm, "end": v(8.75, -26.66) * mm});
            skLineSegment(sketch, "E1551", {"start": v(8.75, -26.66) * mm, "end": v(8.63, -26.77) * mm});
            skLineSegment(sketch, "E1552", {"start": v(8.63, -26.77) * mm, "end": v(8.56, -26.83) * mm});
            skLineSegment(sketch, "E1553", {"start": v(8.56, -26.83) * mm, "end": v(8.54, -26.85) * mm});
            skLineSegment(sketch, "E1554", {"start": v(8.54, -26.85) * mm, "end": v(8.36, -27.03) * mm});
            skLineSegment(sketch, "E1555", {"start": v(8.36, -27.03) * mm, "end": v(8.42, -27.13) * mm});
            skLineSegment(sketch, "E1556", {"start": v(8.42, -27.13) * mm, "end": v(8.42, -27.15) * mm});
            skLineSegment(sketch, "E1557", {"start": v(8.42, -27.15) * mm, "end": v(8.45, -27.19) * mm});
            skLineSegment(sketch, "E1558", {"start": v(8.45, -27.19) * mm, "end": v(8.46, -27.23) * mm});
            skLineSegment(sketch, "E1559", {"start": v(8.46, -27.23) * mm, "end": v(8.45, -27.25) * mm});
            skLineSegment(sketch, "E1560", {"start": v(8.45, -27.25) * mm, "end": v(8.44, -27.27) * mm});
            skLineSegment(sketch, "E1561", {"start": v(8.44, -27.27) * mm, "end": v(8.43, -27.28) * mm});
            skLineSegment(sketch, "E1562", {"start": v(8.43, -27.28) * mm, "end": v(8.42, -27.28) * mm});
            skLineSegment(sketch, "E1563", {"start": v(8.42, -27.28) * mm, "end": v(8.38, -27.31) * mm});
            skLineSegment(sketch, "E1564", {"start": v(8.38, -27.31) * mm, "end": v(8.3, -27.38) * mm});
            skLineSegment(sketch, "E1565", {"start": v(8.3, -27.38) * mm, "end": v(8.18, -27.47) * mm});
            skLineSegment(sketch, "E1566", {"start": v(8.18, -27.47) * mm, "end": v(8.08, -27.55) * mm});
            skLineSegment(sketch, "E1567", {"start": v(8.08, -27.55) * mm, "end": v(8.05, -27.58) * mm});
            skLineSegment(sketch, "E1568", {"start": v(8.05, -27.58) * mm, "end": v(8, -27.6) * mm});
            skLineSegment(sketch, "E1569", {"start": v(8, -27.6) * mm, "end": v(7.87, -27.71) * mm});
            skLineSegment(sketch, "E1570", {"start": v(7.87, -27.71) * mm, "end": v(7.64, -27.9) * mm});
            skLineSegment(sketch, "E1571", {"start": v(7.64, -27.9) * mm, "end": v(7.38, -28.1) * mm});
            skLineSegment(sketch, "E1572", {"start": v(7.38, -28.1) * mm, "end": v(7.19, -28.25) * mm});
            skLineSegment(sketch, "E1573", {"start": v(7.19, -28.25) * mm, "end": v(7.13, -28.3) * mm});
            skLineSegment(sketch, "E1574", {"start": v(7.13, -28.3) * mm, "end": v(7.06, -28.35) * mm});
            skLineSegment(sketch, "E1575", {"start": v(7.06, -28.35) * mm, "end": v(6.85, -28.51) * mm});
            skLineSegment(sketch, "E1576", {"start": v(6.85, -28.51) * mm, "end": v(6.55, -28.75) * mm});
            skLineSegment(sketch, "E1577", {"start": v(6.55, -28.75) * mm, "end": v(6.25, -28.98) * mm});
            skLineSegment(sketch, "E1578", {"start": v(6.25, -28.98) * mm, "end": v(6.06, -29.13) * mm});
            skLineSegment(sketch, "E1579", {"start": v(6.06, -29.13) * mm, "end": v(6, -29.18) * mm});
            skLineSegment(sketch, "E1580", {"start": v(6, -29.18) * mm, "end": v(5.94, -29.22) * mm});
            skLineSegment(sketch, "E1581", {"start": v(5.94, -29.22) * mm, "end": v(5.79, -29.34) * mm});
            skLineSegment(sketch, "E1582", {"start": v(5.79, -29.34) * mm, "end": v(5.61, -29.48) * mm});
            skLineSegment(sketch, "E1583", {"start": v(5.61, -29.48) * mm, "end": v(5.5, -29.58) * mm});
            skLineSegment(sketch, "E1584", {"start": v(5.5, -29.58) * mm, "end": v(5.45, -29.62) * mm});
            skLineSegment(sketch, "E1585", {"start": v(5.45, -29.62) * mm, "end": v(5.45, -29.62) * mm});
            skLineSegment(sketch, "E1586", {"start": v(5.45, -29.62) * mm, "end": v(5.49, -29.65) * mm});
            skLineSegment(sketch, "E1587", {"start": v(5.49, -29.65) * mm, "end": v(5.59, -29.71) * mm});
            skLineSegment(sketch, "E1588", {"start": v(5.59, -29.71) * mm, "end": v(5.74, -29.8) * mm});
            skLineSegment(sketch, "E1589", {"start": v(5.74, -29.8) * mm, "end": v(5.88, -29.9) * mm});
            skLineSegment(sketch, "E1590", {"start": v(5.88, -29.9) * mm, "end": v(5.92, -29.92) * mm});
            skLineSegment(sketch, "E1591", {"start": v(5.92, -29.92) * mm, "end": v(5.97, -29.95) * mm});
            skLineSegment(sketch, "E1592", {"start": v(5.97, -29.95) * mm, "end": v(6.12, -30.04) * mm});
            skLineSegment(sketch, "E1593", {"start": v(6.12, -30.04) * mm, "end": v(6.32, -30.16) * mm});
            skLineSegment(sketch, "E1594", {"start": v(6.32, -30.16) * mm, "end": v(6.5, -30.27) * mm});
            skLineSegment(sketch, "E1595", {"start": v(6.5, -30.27) * mm, "end": v(6.58, -30.33) * mm});
            skLineSegment(sketch, "E1596", {"start": v(6.58, -30.33) * mm, "end": v(6.62, -30.35) * mm});
            skLineSegment(sketch, "E1597", {"start": v(6.62, -30.35) * mm, "end": v(6.64, -30.36) * mm});
            skLineSegment(sketch, "E1598", {"start": v(6.64, -30.36) * mm, "end": v(6.7, -30.4) * mm});
            skLineSegment(sketch, "E1599", {"start": v(6.7, -30.4) * mm, "end": v(6.8, -30.44) * mm});
            skLineSegment(sketch, "E1600", {"start": v(6.8, -30.44) * mm, "end": v(6.85, -30.48) * mm});
            skLineSegment(sketch, "E1601", {"start": v(6.85, -30.48) * mm, "end": v(6.88, -30.49) * mm});
            skLineSegment(sketch, "E1602", {"start": v(6.88, -30.49) * mm, "end": v(6.88, -30.49) * mm});
            skLineSegment(sketch, "E1603", {"start": v(6.88, -30.49) * mm, "end": v(6.9, -30.49) * mm});
            skLineSegment(sketch, "E1604", {"start": v(6.9, -30.49) * mm, "end": v(6.91, -30.47) * mm});
            skLineSegment(sketch, "E1605", {"start": v(6.91, -30.47) * mm, "end": v(7, -30.44) * mm});
            skLineSegment(sketch, "E1606", {"start": v(7, -30.44) * mm, "end": v(7.12, -30.38) * mm});
            skLineSegment(sketch, "E1607", {"start": v(7.12, -30.38) * mm, "end": v(7.3, -30.3) * mm});
            skLineSegment(sketch, "E1608", {"start": v(7.3, -30.3) * mm, "end": v(7.5, -30.19) * mm});
            skLineSegment(sketch, "E1609", {"start": v(7.5, -30.19) * mm, "end": v(7.75, -30.07) * mm});
            skLineSegment(sketch, "E1610", {"start": v(7.75, -30.07) * mm, "end": v(8.04, -29.92) * mm});
            skLineSegment(sketch, "E1611", {"start": v(8.04, -29.92) * mm, "end": v(8.36, -29.76) * mm});
            skLineSegment(sketch, "E1612", {"start": v(8.36, -29.76) * mm, "end": v(8.72, -29.59) * mm});
            skLineSegment(sketch, "E1613", {"start": v(8.72, -29.59) * mm, "end": v(9.1, -29.4) * mm});
            skLineSegment(sketch, "E1614", {"start": v(9.1, -29.4) * mm, "end": v(9.5, -29.2) * mm});
            skLineSegment(sketch, "E1615", {"start": v(9.5, -29.2) * mm, "end": v(9.94, -28.98) * mm});
            skLineSegment(sketch, "E1616", {"start": v(9.94, -28.98) * mm, "end": v(10.4, -28.75) * mm});
            skLineSegment(sketch, "E1617", {"start": v(10.4, -28.75) * mm, "end": v(10.87, -28.52) * mm});
            skLineSegment(sketch, "E1618", {"start": v(10.87, -28.52) * mm, "end": v(11.36, -28.27) * mm});
            skLineSegment(sketch, "E1619", {"start": v(11.36, -28.27) * mm, "end": v(11.74, -28.08) * mm});
            skLineSegment(sketch, "E1620", {"start": v(11.74, -28.08) * mm, "end": v(11.86, -28.02) * mm});
            skLineSegment(sketch, "E1621", {"start": v(11.86, -28.02) * mm, "end": v(12, -27.96) * mm});
            skLineSegment(sketch, "E1622", {"start": v(12, -27.96) * mm, "end": v(12.37, -27.77) * mm});
            skLineSegment(sketch, "E1623", {"start": v(12.37, -27.77) * mm, "end": v(12.86, -27.53) * mm});
            skLineSegment(sketch, "E1624", {"start": v(12.86, -27.53) * mm, "end": v(13.33, -27.3) * mm});
            skLineSegment(sketch, "E1625", {"start": v(13.33, -27.3) * mm, "end": v(13.78, -27.06) * mm});
            skLineSegment(sketch, "E1626", {"start": v(13.78, -27.06) * mm, "end": v(14.22, -26.85) * mm});
            skLineSegment(sketch, "E1627", {"start": v(14.22, -26.85) * mm, "end": v(14.63, -26.64) * mm});
            skLineSegment(sketch, "E1628", {"start": v(14.63, -26.64) * mm, "end": v(15, -26.45) * mm});
            skLineSegment(sketch, "E1629", {"start": v(15, -26.45) * mm, "end": v(15.36, -26.28) * mm});
            skLineSegment(sketch, "E1630", {"start": v(15.36, -26.28) * mm, "end": v(15.68, -26.12) * mm});
            skLineSegment(sketch, "E1631", {"start": v(15.68, -26.12) * mm, "end": v(15.97, -25.98) * mm});
            skLineSegment(sketch, "E1632", {"start": v(15.97, -25.98) * mm, "end": v(16.22, -25.85) * mm});
            skLineSegment(sketch, "E1633", {"start": v(16.22, -25.85) * mm, "end": v(16.43, -25.75) * mm});
            skLineSegment(sketch, "E1634", {"start": v(16.43, -25.75) * mm, "end": v(16.6, -25.67) * mm});
            skLineSegment(sketch, "E1635", {"start": v(16.6, -25.67) * mm, "end": v(16.73, -25.6) * mm});
            skLineSegment(sketch, "E1636", {"start": v(16.73, -25.6) * mm, "end": v(16.8, -25.57) * mm});
            skLineSegment(sketch, "E1637", {"start": v(16.8, -25.57) * mm, "end": v(16.83, -25.55) * mm});
            skLineSegment(sketch, "E1638", {"start": v(16.83, -25.55) * mm, "end": v(16.83, -25.55) * mm});
            skLineSegment(sketch, "E1639", {"start": v(16.83, -25.55) * mm, "end": v(16.85, -25.55) * mm});
            skLineSegment(sketch, "E1640", {"start": v(16.85, -25.55) * mm, "end": v(16.88, -25.58) * mm});
            skLineSegment(sketch, "E1641", {"start": v(16.88, -25.58) * mm, "end": v(17, -25.64) * mm});
            skLineSegment(sketch, "E1642", {"start": v(17, -25.64) * mm, "end": v(17.14, -25.73) * mm});
            skLineSegment(sketch, "E1643", {"start": v(17.14, -25.73) * mm, "end": v(17.28, -25.81) * mm});
            skLineSegment(sketch, "E1644", {"start": v(17.28, -25.81) * mm, "end": v(17.33, -25.84) * mm});
            skLineSegment(sketch, "E1645", {"start": v(17.33, -25.84) * mm, "end": v(17.43, -25.9) * mm});
            skLineSegment(sketch, "E1646", {"start": v(17.43, -25.9) * mm, "end": v(17.75, -26.1) * mm});
            skLineSegment(sketch, "E1647", {"start": v(17.75, -26.1) * mm, "end": v(18.13, -26.33) * mm});
            skLineSegment(sketch, "E1648", {"start": v(18.13, -26.33) * mm, "end": v(18.46, -26.52) * mm});
            skLineSegment(sketch, "E1649", {"start": v(18.46, -26.52) * mm, "end": v(18.74, -26.68) * mm});
            skLineSegment(sketch, "E1650", {"start": v(18.74, -26.68) * mm, "end": v(18.98, -26.8) * mm});
            skLineSegment(sketch, "E1651", {"start": v(18.98, -26.8) * mm, "end": v(19.17, -26.9) * mm});
            skLineSegment(sketch, "E1652", {"start": v(19.17, -26.9) * mm, "end": v(19.31, -26.96) * mm});
            skLineSegment(sketch, "E1653", {"start": v(19.31, -26.96) * mm, "end": v(19.39, -26.98) * mm});
            skLineSegment(sketch, "E1654", {"start": v(19.39, -26.98) * mm, "end": v(19.41, -26.98) * mm});
            skLineSegment(sketch, "E1655", {"start": v(19.41, -26.98) * mm, "end": v(19.45, -26.99) * mm});
            skLineSegment(sketch, "E1656", {"start": v(19.45, -26.99) * mm, "end": v(19.56, -26.98) * mm});
            skLineSegment(sketch, "E1657", {"start": v(19.56, -26.98) * mm, "end": v(19.68, -26.93) * mm});
            skLineSegment(sketch, "E1658", {"start": v(19.68, -26.93) * mm, "end": v(19.81, -26.81) * mm});
            skLineSegment(sketch, "E1659", {"start": v(19.81, -26.81) * mm, "end": v(19.92, -26.68) * mm});
            skLineSegment(sketch, "E1660", {"start": v(19.92, -26.68) * mm, "end": v(19.95, -26.63) * mm});
            skLineSegment(sketch, "E1661", {"start": v(19.95, -26.63) * mm, "end": v(19.99, -26.58) * mm});
            skLineSegment(sketch, "E1662", {"start": v(19.99, -26.58) * mm, "end": v(20.1, -26.41) * mm});
            skLineSegment(sketch, "E1663", {"start": v(20.1, -26.41) * mm, "end": v(20.2, -26.23) * mm});
            skLineSegment(sketch, "E1664", {"start": v(20.2, -26.23) * mm, "end": v(20.26, -26.06) * mm});
            skLineSegment(sketch, "E1665", {"start": v(20.26, -26.06) * mm, "end": v(20.29, -25.92) * mm});
            skLineSegment(sketch, "E1666", {"start": v(20.29, -25.92) * mm, "end": v(20.28, -25.8) * mm});
            skLineSegment(sketch, "E1667", {"start": v(20.28, -25.8) * mm, "end": v(20.24, -25.68) * mm});
            skLineSegment(sketch, "E1668", {"start": v(20.24, -25.68) * mm, "end": v(20.16, -25.57) * mm});
            skLineSegment(sketch, "E1669", {"start": v(20.16, -25.57) * mm, "end": v(20.08, -25.5) * mm});
            skLineSegment(sketch, "E1670", {"start": v(20.08, -25.5) * mm, "end": v(20.05, -25.48) * mm});
            skLineSegment(sketch, "E1671", {"start": v(20.05, -25.48) * mm, "end": v(20.04, -25.46) * mm});
            skLineSegment(sketch, "E1672", {"start": v(20.04, -25.46) * mm, "end": v(19.99, -25.43) * mm});
            skLineSegment(sketch, "E1673", {"start": v(19.99, -25.43) * mm, "end": v(19.87, -25.36) * mm});
            skLineSegment(sketch, "E1674", {"start": v(19.87, -25.36) * mm, "end": v(19.7, -25.27) * mm});
            skLineSegment(sketch, "E1675", {"start": v(19.7, -25.27) * mm, "end": v(19.52, -25.16) * mm});
            skLineSegment(sketch, "E1676", {"start": v(19.52, -25.16) * mm, "end": v(19.32, -25.04) * mm});
            skLineSegment(sketch, "E1677", {"start": v(19.32, -25.04) * mm, "end": v(19.1, -24.93) * mm});
            skLineSegment(sketch, "E1678", {"start": v(19.1, -24.93) * mm, "end": v(18.9, -24.81) * mm});
            skLineSegment(sketch, "E1679", {"start": v(18.9, -24.81) * mm, "end": v(18.76, -24.74) * mm});
            skLineSegment(sketch, "E1680", {"start": v(18.76, -24.74) * mm, "end": v(18.72, -24.71) * mm});
            skLineSegment(sketch, "E1681", {"start": v(18.72, -24.71) * mm, "end": v(18.7, -24.7) * mm});
            skLineSegment(sketch, "E1682", {"start": v(18.7, -24.7) * mm, "end": v(18.66, -24.68) * mm});
            skLineSegment(sketch, "E1683", {"start": v(18.66, -24.68) * mm, "end": v(18.61, -24.64) * mm});
            skLineSegment(sketch, "E1684", {"start": v(18.61, -24.64) * mm, "end": v(18.58, -24.62) * mm});
            skLineSegment(sketch, "E1685", {"start": v(18.58, -24.62) * mm, "end": v(18.57, -24.6) * mm});
            skLineSegment(sketch, "E1686", {"start": v(18.57, -24.6) * mm, "end": v(18.57, -24.6) * mm});
            skLineSegment(sketch, "E1687", {"start": v(18.57, -24.6) * mm, "end": v(18.6, -24.58) * mm});
            skLineSegment(sketch, "E1688", {"start": v(18.6, -24.58) * mm, "end": v(18.67, -24.54) * mm});
            skLineSegment(sketch, "E1689", {"start": v(18.67, -24.54) * mm, "end": v(18.78, -24.47) * mm});
            skLineSegment(sketch, "E1690", {"start": v(18.78, -24.47) * mm, "end": v(18.92, -24.4) * mm});
            skLineSegment(sketch, "E1691", {"start": v(18.92, -24.4) * mm, "end": v(19.1, -24.3) * mm});
            skLineSegment(sketch, "E1692", {"start": v(19.1, -24.3) * mm, "end": v(19.3, -24.2) * mm});
            skLineSegment(sketch, "E1693", {"start": v(19.3, -24.2) * mm, "end": v(19.52, -24.08) * mm});
            skLineSegment(sketch, "E1694", {"start": v(19.52, -24.08) * mm, "end": v(19.7, -23.99) * mm});
            skLineSegment(sketch, "E1695", {"start": v(19.7, -23.99) * mm, "end": v(19.76, -23.96) * mm});
            skLineSegment(sketch, "E1696", {"start": v(19.76, -23.96) * mm, "end": v(20.95, -23.36) * mm});
            skLineSegment(sketch, "E1697", {"start": v(20.95, -23.36) * mm, "end": v(21.37, -23.34) * mm});
            skLineSegment(sketch, "E1698", {"start": v(21.37, -23.34) * mm, "end": v(21.47, -23.34) * mm});
            skLineSegment(sketch, "E1699", {"start": v(21.47, -23.34) * mm, "end": v(21.8, -23.35) * mm});
            skLineSegment(sketch, "E1700", {"start": v(21.8, -23.35) * mm, "end": v(22.18, -23.4) * mm});
            skLineSegment(sketch, "E1701", {"start": v(22.18, -23.4) * mm, "end": v(22.53, -23.5) * mm});
            skLineSegment(sketch, "E1702", {"start": v(22.53, -23.5) * mm, "end": v(22.78, -23.62) * mm});
            skLineSegment(sketch, "E1703", {"start": v(22.78, -23.62) * mm, "end": v(22.86, -23.66) * mm});
            skLineSegment(sketch, "E1704", {"start": v(22.86, -23.66) * mm, "end": v(22.88, -23.67) * mm});
            skLineSegment(sketch, "E1705", {"start": v(22.88, -23.67) * mm, "end": v(22.94, -23.7) * mm});
            skLineSegment(sketch, "E1706", {"start": v(22.94, -23.7) * mm, "end": v(23.05, -23.76) * mm});
            skLineSegment(sketch, "E1707", {"start": v(23.05, -23.76) * mm, "end": v(23.17, -23.83) * mm});
            skLineSegment(sketch, "E1708", {"start": v(23.17, -23.83) * mm, "end": v(23.27, -23.88) * mm});
            skLineSegment(sketch, "E1709", {"start": v(23.27, -23.88) * mm, "end": v(23.3, -23.9) * mm});
            skLineSegment(sketch, "E1710", {"start": v(23.3, -23.9) * mm, "end": v(23.34, -23.92) * mm});
            skLineSegment(sketch, "E1711", {"start": v(23.34, -23.92) * mm, "end": v(23.47, -23.99) * mm});
            skLineSegment(sketch, "E1712", {"start": v(23.47, -23.99) * mm, "end": v(23.7, -24.12) * mm});
            skLineSegment(sketch, "E1713", {"start": v(23.7, -24.12) * mm, "end": v(23.96, -24.26) * mm});
            skLineSegment(sketch, "E1714", {"start": v(23.96, -24.26) * mm, "end": v(24.16, -24.37) * mm});
            skLineSegment(sketch, "E1715", {"start": v(24.16, -24.37) * mm, "end": v(24.22, -24.41) * mm});
            skLineSegment(sketch, "E1716", {"start": v(24.22, -24.41) * mm, "end": v(24.29, -24.45) * mm});
            skLineSegment(sketch, "E1717", {"start": v(24.29, -24.45) * mm, "end": v(24.48, -24.55) * mm});
            skLineSegment(sketch, "E1718", {"start": v(24.48, -24.55) * mm, "end": v(24.72, -24.69) * mm});
            skLineSegment(sketch, "E1719", {"start": v(24.72, -24.69) * mm, "end": v(24.92, -24.8) * mm});
            skLineSegment(sketch, "E1720", {"start": v(24.92, -24.8) * mm, "end": v(25.02, -24.85) * mm});
            skLineSegment(sketch, "E1721", {"start": v(25.02, -24.85) * mm, "end": v(25.04, -24.87) * mm});
            skLineSegment(sketch, "E1722", {"start": v(25.04, -24.87) * mm, "end": v(25.07, -24.88) * mm});
            skLineSegment(sketch, "E1723", {"start": v(25.07, -24.88) * mm, "end": v(25.18, -24.94) * mm});
            skLineSegment(sketch, "E1724", {"start": v(25.18, -24.94) * mm, "end": v(25.4, -25.06) * mm});
            skLineSegment(sketch, "E1725", {"start": v(25.4, -25.06) * mm, "end": v(25.66, -25.2) * mm});
            skLineSegment(sketch, "E1726", {"start": v(25.66, -25.2) * mm, "end": v(25.88, -25.33) * mm});
            skLineSegment(sketch, "E1727", {"start": v(25.88, -25.33) * mm, "end": v(25.95, -25.37) * mm});
            skLineSegment(sketch, "E1728", {"start": v(25.95, -25.37) * mm, "end": v(26.02, -25.41) * mm});
            skLineSegment(sketch, "E1729", {"start": v(26.02, -25.41) * mm, "end": v(26.24, -25.53) * mm});
            skLineSegment(sketch, "E1730", {"start": v(26.24, -25.53) * mm, "end": v(26.52, -25.69) * mm});
            skLineSegment(sketch, "E1731", {"start": v(26.52, -25.69) * mm, "end": v(26.75, -25.81) * mm});
            skLineSegment(sketch, "E1732", {"start": v(26.75, -25.81) * mm, "end": v(26.87, -25.88) * mm});
            skLineSegment(sketch, "E1733", {"start": v(26.87, -25.88) * mm, "end": v(26.9, -25.9) * mm});
            skLineSegment(sketch, "E1734", {"start": v(26.9, -25.9) * mm, "end": v(26.93, -25.91) * mm});
            skLineSegment(sketch, "E1735", {"start": v(26.93, -25.91) * mm, "end": v(27, -25.95) * mm});
            skLineSegment(sketch, "E1736", {"start": v(27, -25.95) * mm, "end": v(27.12, -26.01) * mm});
            skLineSegment(sketch, "E1737", {"start": v(27.12, -26.01) * mm, "end": v(27.21, -26.07) * mm});
            skLineSegment(sketch, "E1738", {"start": v(27.21, -26.07) * mm, "end": v(27.26, -26.1) * mm});
            skLineSegment(sketch, "E1739", {"start": v(27.26, -26.1) * mm, "end": v(27.28, -26.11) * mm});
            skLineSegment(sketch, "E1740", {"start": v(27.28, -26.11) * mm, "end": v(27.3, -26.12) * mm});
            skLineSegment(sketch, "E1741", {"start": v(27.3, -26.12) * mm, "end": v(27.33, -26.14) * mm});
            skLineSegment(sketch, "E1742", {"start": v(27.33, -26.14) * mm, "end": v(27.38, -26.17) * mm});
            skLineSegment(sketch, "E1743", {"start": v(27.38, -26.17) * mm, "end": v(27.41, -26.19) * mm});
            skLineSegment(sketch, "E1744", {"start": v(27.41, -26.19) * mm, "end": v(27.42, -26.2) * mm});
            skLineSegment(sketch, "E1745", {"start": v(27.42, -26.2) * mm, "end": v(27.43, -26.2) * mm});
            skLineSegment(sketch, "E1746", {"start": v(27.43, -26.2) * mm, "end": v(27.43, -26.2) * mm});
            skLineSegment(sketch, "E1747", {"start": v(27.43, -26.2) * mm, "end": v(27.44, -26.2) * mm});
            skLineSegment(sketch, "E1748", {"start": v(27.44, -26.2) * mm, "end": v(27.48, -26.21) * mm});
            skLineSegment(sketch, "E1749", {"start": v(27.48, -26.21) * mm, "end": v(27.53, -26.24) * mm});
            skLineSegment(sketch, "E1750", {"start": v(27.53, -26.24) * mm, "end": v(27.6, -26.28) * mm});
            skLineSegment(sketch, "E1751", {"start": v(27.6, -26.28) * mm, "end": v(27.67, -26.32) * mm});
            skLineSegment(sketch, "E1752", {"start": v(27.67, -26.32) * mm, "end": v(27.76, -26.37) * mm});
            skLineSegment(sketch, "E1753", {"start": v(27.76, -26.37) * mm, "end": v(27.86, -26.42) * mm});
            skLineSegment(sketch, "E1754", {"start": v(27.86, -26.42) * mm, "end": v(27.93, -26.47) * mm});
            skLineSegment(sketch, "E1755", {"start": v(27.93, -26.47) * mm, "end": v(27.96, -26.48) * mm});
            skLineSegment(sketch, "E1756", {"start": v(27.96, -26.48) * mm, "end": v(28.01, -26.51) * mm});
            skLineSegment(sketch, "E1757", {"start": v(28.01, -26.51) * mm, "end": v(28.16, -26.6) * mm});
            skLineSegment(sketch, "E1758", {"start": v(28.16, -26.6) * mm, "end": v(28.35, -26.7) * mm});
            skLineSegment(sketch, "E1759", {"start": v(28.35, -26.7) * mm, "end": v(28.5, -26.78) * mm});
            skLineSegment(sketch, "E1760", {"start": v(28.5, -26.78) * mm, "end": v(28.56, -26.82) * mm});
            skLineSegment(sketch, "E1761", {"start": v(28.56, -26.82) * mm, "end": v(28.57, -26.82) * mm});
            skLineSegment(sketch, "E1762", {"start": v(28.57, -26.82) * mm, "end": v(28.58, -26.83) * mm});
            skLineSegment(sketch, "E1763", {"start": v(28.58, -26.83) * mm, "end": v(28.64, -26.86) * mm});
            skLineSegment(sketch, "E1764", {"start": v(28.64, -26.86) * mm, "end": v(28.76, -26.92) * mm});
            skLineSegment(sketch, "E1765", {"start": v(28.76, -26.92) * mm, "end": v(28.9, -27) * mm});
            skLineSegment(sketch, "E1766", {"start": v(28.9, -27) * mm, "end": v(29.02, -27.08) * mm});
            skLineSegment(sketch, "E1767", {"start": v(29.02, -27.08) * mm, "end": v(29.06, -27.1) * mm});
            skLineSegment(sketch, "E1768", {"start": v(29.06, -27.1) * mm, "end": v(29.2, -27.18) * mm});
            skLineSegment(sketch, "E1769", {"start": v(29.2, -27.18) * mm, "end": v(29.66, -27.43) * mm});
            skLineSegment(sketch, "E1770", {"start": v(29.66, -27.43) * mm, "end": v(30.24, -27.69) * mm});
            skLineSegment(sketch, "E1771", {"start": v(30.24, -27.69) * mm, "end": v(30.8, -27.89) * mm});
            skLineSegment(sketch, "E1772", {"start": v(30.8, -27.89) * mm, "end": v(31.25, -28) * mm});
            skLineSegment(sketch, "E1773", {"start": v(31.25, -28) * mm, "end": v(31.4, -28.04) * mm});
            skLineSegment(sketch, "E1774", {"start": v(31.4, -28.04) * mm, "end": v(31.5, -28.06) * mm});
            skLineSegment(sketch, "E1775", {"start": v(31.5, -28.06) * mm, "end": v(31.82, -28.11) * mm});
            skLineSegment(sketch, "E1776", {"start": v(31.82, -28.11) * mm, "end": v(32.32, -28.17) * mm});
            skLineSegment(sketch, "E1777", {"start": v(32.32, -28.17) * mm, "end": v(32.8, -28.21) * mm});
            skLineSegment(sketch, "E1778", {"start": v(32.8, -28.21) * mm, "end": v(33.1, -28.23) * mm});
            skLineSegment(sketch, "E1779", {"start": v(33.1, -28.23) * mm, "end": v(33.2, -28.22) * mm});
            skLineSegment(sketch, "E1780", {"start": v(33.2, -28.22) * mm, "end": v(33.3, -28.22) * mm});
            skLineSegment(sketch, "E1781", {"start": v(33.3, -28.22) * mm, "end": v(33.6, -28.2) * mm});
            skLineSegment(sketch, "E1782", {"start": v(33.6, -28.2) * mm, "end": v(33.88, -28.1) * mm});
            skLineSegment(sketch, "E1783", {"start": v(33.88, -28.1) * mm, "end": v(34.07, -27.97) * mm});
            skLineSegment(sketch, "E1784", {"start": v(34.07, -27.97) * mm, "end": v(34.15, -27.78) * mm});
            skLineSegment(sketch, "E1785", {"start": v(34.15, -27.78) * mm, "end": v(34.12, -27.52) * mm});
            skLineSegment(sketch, "E1786", {"start": v(34.12, -27.52) * mm, "end": v(34, -27.2) * mm});
            skLineSegment(sketch, "E1787", {"start": v(34, -27.2) * mm, "end": v(33.76, -26.8) * mm});
            skLineSegment(sketch, "E1788", {"start": v(33.76, -26.8) * mm, "end": v(33.5, -26.43) * mm});
            skLineSegment(sketch, "E1789", {"start": v(33.5, -26.43) * mm, "end": v(33.42, -26.31) * mm});
            skLineSegment(sketch, "E1790", {"start": v(33.42, -26.31) * mm, "end": v(33.38, -26.26) * mm});
            skLineSegment(sketch, "E1791", {"start": v(33.38, -26.26) * mm, "end": v(33.27, -26.12) * mm});
            skLineSegment(sketch, "E1792", {"start": v(33.27, -26.12) * mm, "end": v(33.1, -25.92) * mm});
            skLineSegment(sketch, "E1793", {"start": v(33.1, -25.92) * mm, "end": v(32.96, -25.74) * mm});
            skLineSegment(sketch, "E1794", {"start": v(32.96, -25.74) * mm, "end": v(32.86, -25.63) * mm});
            skLineSegment(sketch, "E1795", {"start": v(32.86, -25.63) * mm, "end": v(32.83, -25.6) * mm});
            skLineSegment(sketch, "E1796", {"start": v(32.83, -25.6) * mm, "end": v(32.74, -25.5) * mm});
            skLineSegment(sketch, "E1797", {"start": v(32.74, -25.5) * mm, "end": v(32.43, -25.2) * mm});
            skLineSegment(sketch, "E1798", {"start": v(32.43, -25.2) * mm, "end": v(31.95, -24.8) * mm});
            skLineSegment(sketch, "E1799", {"start": v(31.95, -24.8) * mm, "end": v(31.42, -24.44) * mm});
            skLineSegment(sketch, "E1800", {"start": v(31.42, -24.44) * mm, "end": v(31, -24.18) * mm});
            skLineSegment(sketch, "E1801", {"start": v(31, -24.18) * mm, "end": v(30.85, -24.1) * mm});
            skLineSegment(sketch, "E1802", {"start": v(30.85, -24.1) * mm, "end": v(30.8, -24.08) * mm});
            skLineSegment(sketch, "E1803", {"start": v(30.8, -24.08) * mm, "end": v(30.67, -24) * mm});
            skLineSegment(sketch, "E1804", {"start": v(30.67, -24) * mm, "end": v(30.4, -23.86) * mm});
            skLineSegment(sketch, "E1805", {"start": v(30.4, -23.86) * mm, "end": v(30.11, -23.7) * mm});
            skLineSegment(sketch, "E1806", {"start": v(30.11, -23.7) * mm, "end": v(29.89, -23.56) * mm});
            skLineSegment(sketch, "E1807", {"start": v(29.89, -23.56) * mm, "end": v(29.81, -23.52) * mm});
            skLineSegment(sketch, "E1808", {"start": v(29.81, -23.52) * mm, "end": v(29.74, -23.48) * mm});
            skLineSegment(sketch, "E1809", {"start": v(29.74, -23.48) * mm, "end": v(29.53, -23.36) * mm});
            skLineSegment(sketch, "E1810", {"start": v(29.53, -23.36) * mm, "end": v(29.28, -23.22) * mm});
            skLineSegment(sketch, "E1811", {"start": v(29.28, -23.22) * mm, "end": v(29.08, -23.11) * mm});
            skLineSegment(sketch, "E1812", {"start": v(29.08, -23.11) * mm, "end": v(29, -23.06) * mm});
            skLineSegment(sketch, "E1813", {"start": v(29, -23.06) * mm, "end": v(28.97, -23.05) * mm});
            skLineSegment(sketch, "E1814", {"start": v(28.97, -23.05) * mm, "end": v(28.94, -23.03) * mm});
            skLineSegment(sketch, "E1815", {"start": v(28.94, -23.03) * mm, "end": v(28.83, -22.97) * mm});
            skLineSegment(sketch, "E1816", {"start": v(28.83, -22.97) * mm, "end": v(28.6, -22.84) * mm});
            skLineSegment(sketch, "E1817", {"start": v(28.6, -22.84) * mm, "end": v(28.3, -22.68) * mm});
            skLineSegment(sketch, "E1818", {"start": v(28.3, -22.68) * mm, "end": v(27.99, -22.5) * mm});
            skLineSegment(sketch, "E1819", {"start": v(27.99, -22.5) * mm, "end": v(27.67, -22.32) * mm});
            skLineSegment(sketch, "E1820", {"start": v(27.67, -22.32) * mm, "end": v(27.4, -22.16) * mm});
            skLineSegment(sketch, "E1821", {"start": v(27.4, -22.16) * mm, "end": v(27.17, -22.04) * mm});
            skLineSegment(sketch, "E1822", {"start": v(27.17, -22.04) * mm, "end": v(27.08, -21.98) * mm});
            skLineSegment(sketch, "E1823", {"start": v(27.08, -21.98) * mm, "end": v(27.05, -21.96) * mm});
            skLineSegment(sketch, "E1824", {"start": v(27.05, -21.96) * mm, "end": v(27.03, -21.95) * mm});
            skLineSegment(sketch, "E1825", {"start": v(27.03, -21.95) * mm, "end": v(26.98, -21.92) * mm});
            skLineSegment(sketch, "E1826", {"start": v(26.98, -21.92) * mm, "end": v(26.92, -21.9) * mm});
            skLineSegment(sketch, "E1827", {"start": v(26.92, -21.9) * mm, "end": v(26.88, -21.87) * mm});
            skLineSegment(sketch, "E1828", {"start": v(26.88, -21.87) * mm, "end": v(26.87, -21.86) * mm});
            skLineSegment(sketch, "E1829", {"start": v(26.87, -21.86) * mm, "end": v(26.86, -21.86) * mm});
            skLineSegment(sketch, "E1830", {"start": v(26.86, -21.86) * mm, "end": v(26.85, -21.86) * mm});
            skLineSegment(sketch, "E1831", {"start": v(26.85, -21.86) * mm, "end": v(26.83, -21.85) * mm});
            skLineSegment(sketch, "E1832", {"start": v(26.83, -21.85) * mm, "end": v(26.76, -21.8) * mm});
            skLineSegment(sketch, "E1833", {"start": v(26.76, -21.8) * mm, "end": v(26.65, -21.75) * mm});
            skLineSegment(sketch, "E1834", {"start": v(26.65, -21.75) * mm, "end": v(26.55, -21.7) * mm});
            skLineSegment(sketch, "E1835", {"start": v(26.55, -21.7) * mm, "end": v(26.52, -21.67) * mm});
            skLineSegment(sketch, "E1836", {"start": v(26.52, -21.67) * mm, "end": v(26.44, -21.63) * mm});
            skLineSegment(sketch, "E1837", {"start": v(26.44, -21.63) * mm, "end": v(26.2, -21.49) * mm});
            skLineSegment(sketch, "E1838", {"start": v(26.2, -21.49) * mm, "end": v(25.96, -21.36) * mm});
            skLineSegment(sketch, "E1839", {"start": v(25.96, -21.36) * mm, "end": v(25.78, -21.26) * mm});
            skLineSegment(sketch, "E1840", {"start": v(25.78, -21.26) * mm, "end": v(25.67, -21.2) * mm});
            skLineSegment(sketch, "E1841", {"start": v(25.67, -21.2) * mm, "end": v(25.63, -21.17) * mm});
            skLineSegment(sketch, "E1842", {"start": v(25.63, -21.17) * mm, "end": v(25.52, -21.11) * mm});
            skLineSegment(sketch, "E1843", {"start": v(25.52, -21.11) * mm, "end": v(25.19, -20.93) * mm});
            skLineSegment(sketch, "E1844", {"start": v(25.19, -20.93) * mm, "end": v(24.83, -20.72) * mm});
            skLineSegment(sketch, "E1845", {"start": v(24.83, -20.72) * mm, "end": v(24.55, -20.55) * mm});
            skLineSegment(sketch, "E1846", {"start": v(24.55, -20.55) * mm, "end": v(24.33, -20.4) * mm});
            skLineSegment(sketch, "E1847", {"start": v(24.33, -20.4) * mm, "end": v(24.16, -20.27) * mm});
            skLineSegment(sketch, "E1848", {"start": v(24.16, -20.27) * mm, "end": v(24.01, -20.14) * mm});
            skLineSegment(sketch, "E1849", {"start": v(24.01, -20.14) * mm, "end": v(23.89, -20) * mm});
            skLineSegment(sketch, "E1850", {"start": v(23.89, -20) * mm, "end": v(23.8, -19.89) * mm});
            skLineSegment(sketch, "E1851", {"start": v(23.8, -19.89) * mm, "end": v(23.76, -19.85) * mm});
            skLineSegment(sketch, "E1852", {"start": v(23.76, -19.85) * mm, "end": v(23.71, -19.78) * mm});
            skLineSegment(sketch, "E1853", {"start": v(23.71, -19.78) * mm, "end": v(23.57, -19.56) * mm});
            skLineSegment(sketch, "E1854", {"start": v(23.57, -19.56) * mm, "end": v(23.43, -19.3) * mm});
            skLineSegment(sketch, "E1855", {"start": v(23.43, -19.3) * mm, "end": v(23.34, -19.06) * mm});
            skLineSegment(sketch, "E1856", {"start": v(23.34, -19.06) * mm, "end": v(23.3, -18.88) * mm});
            skLineSegment(sketch, "E1857", {"start": v(23.3, -18.88) * mm, "end": v(23.3, -18.82) * mm});
            skLineSegment(sketch, "E1858", {"start": v(23.3, -18.82) * mm, "end": v(23.3, -18.8) * mm});
            skLineSegment(sketch, "E1859", {"start": v(23.3, -18.8) * mm, "end": v(23.3, -18.7) * mm});
            skLineSegment(sketch, "E1860", {"start": v(23.3, -18.7) * mm, "end": v(23.28, -18.6) * mm});
            skLineSegment(sketch, "E1861", {"start": v(23.28, -18.6) * mm, "end": v(23.27, -18.5) * mm});
            skLineSegment(sketch, "E1862", {"start": v(23.27, -18.5) * mm, "end": v(23.27, -18.44) * mm});
            skLineSegment(sketch, "E1863", {"start": v(23.27, -18.44) * mm, "end": v(23.26, -18.42) * mm});
            skLineSegment(sketch, "E1864", {"start": v(23.26, -18.42) * mm, "end": v(23.26, -18.4) * mm});
            skLineSegment(sketch, "E1865", {"start": v(23.26, -18.4) * mm, "end": v(23.25, -18.26) * mm});
            skLineSegment(sketch, "E1866", {"start": v(23.25, -18.26) * mm, "end": v(23.23, -18.1) * mm});
            skLineSegment(sketch, "E1867", {"start": v(23.23, -18.1) * mm, "end": v(23.23, -18.07) * mm});
            skLineSegment(sketch, "E1868", {"start": v(23.23, -18.07) * mm, "end": v(23.22, -17.93) * mm});
            skLineSegment(sketch, "E1869", {"start": v(23.22, -17.93) * mm, "end": v(23.19, -17.54) * mm});
            skLineSegment(sketch, "E1870", {"start": v(23.19, -17.54) * mm, "end": v(23.15, -17.06) * mm});
            skLineSegment(sketch, "E1871", {"start": v(23.15, -17.06) * mm, "end": v(23.11, -16.7) * mm});
            skLineSegment(sketch, "E1872", {"start": v(23.11, -16.7) * mm, "end": v(23.1, -16.55) * mm});
            skLineSegment(sketch, "E1873", {"start": v(23.1, -16.55) * mm, "end": v(23.1, -16.52) * mm});
            skLineSegment(sketch, "E1874", {"start": v(23.1, -16.52) * mm, "end": v(23.1, -16.5) * mm});
            skLineSegment(sketch, "E1875", {"start": v(23.1, -16.5) * mm, "end": v(23.09, -16.46) * mm});
            skLineSegment(sketch, "E1876", {"start": v(23.09, -16.46) * mm, "end": v(23.09, -16.43) * mm});
            skLineSegment(sketch, "E1877", {"start": v(23.09, -16.43) * mm, "end": v(23.11, -16.42) * mm});
            skLineSegment(sketch, "E1878", {"start": v(23.11, -16.42) * mm, "end": v(23.15, -16.43) * mm});
            skLineSegment(sketch, "E1879", {"start": v(23.15, -16.43) * mm, "end": v(23.16, -16.43) * mm});
            skLineSegment(sketch, "E1880", {"start": v(23.16, -16.43) * mm, "end": v(23.17, -16.44) * mm});
            skLineSegment(sketch, "E1881", {"start": v(23.17, -16.44) * mm, "end": v(23.22, -16.46) * mm});
            skLineSegment(sketch, "E1882", {"start": v(23.22, -16.46) * mm, "end": v(23.33, -16.51) * mm});
            skLineSegment(sketch, "E1883", {"start": v(23.33, -16.51) * mm, "end": v(23.47, -16.59) * mm});
            skLineSegment(sketch, "E1884", {"start": v(23.47, -16.59) * mm, "end": v(23.58, -16.65) * mm});
            skLineSegment(sketch, "E1885", {"start": v(23.58, -16.65) * mm, "end": v(23.62, -16.68) * mm});
            skLineSegment(sketch, "E1886", {"start": v(23.62, -16.68) * mm, "end": v(23.71, -16.73) * mm});
            skLineSegment(sketch, "E1887", {"start": v(23.71, -16.73) * mm, "end": v(24, -16.89) * mm});
            skLineSegment(sketch, "E1888", {"start": v(24, -16.89) * mm, "end": v(24.28, -17.05) * mm});
            skLineSegment(sketch, "E1889", {"start": v(24.28, -17.05) * mm, "end": v(24.52, -17.17) * mm});
            skLineSegment(sketch, "E1890", {"start": v(24.52, -17.17) * mm, "end": v(24.7, -17.24) * mm});
            skLineSegment(sketch, "E1891", {"start": v(24.7, -17.24) * mm, "end": v(24.84, -17.27) * mm});
            skLineSegment(sketch, "E1892", {"start": v(24.84, -17.27) * mm, "end": v(24.95, -17.27) * mm});
            skLineSegment(sketch, "E1893", {"start": v(24.95, -17.27) * mm, "end": v(25.05, -17.24) * mm});
            skLineSegment(sketch, "E1894", {"start": v(25.05, -17.24) * mm, "end": v(25.13, -17.2) * mm});
            skLineSegment(sketch, "E1895", {"start": v(25.13, -17.2) * mm, "end": v(25.15, -17.19) * mm});
            skLineSegment(sketch, "E1896", {"start": v(25.15, -17.19) * mm, "end": v(25.17, -17.17) * mm});
            skLineSegment(sketch, "E1897", {"start": v(25.17, -17.17) * mm, "end": v(25.23, -17.12) * mm});
            skLineSegment(sketch, "E1898", {"start": v(25.23, -17.12) * mm, "end": v(25.31, -17) * mm});
            skLineSegment(sketch, "E1899", {"start": v(25.31, -17) * mm, "end": v(25.4, -16.87) * mm});
            skLineSegment(sketch, "E1900", {"start": v(25.4, -16.87) * mm, "end": v(25.49, -16.72) * mm});
            skLineSegment(sketch, "E1901", {"start": v(25.49, -16.72) * mm, "end": v(25.56, -16.57) * mm});
            skLineSegment(sketch, "E1902", {"start": v(25.56, -16.57) * mm, "end": v(25.62, -16.41) * mm});
            skLineSegment(sketch, "E1903", {"start": v(25.62, -16.41) * mm, "end": v(25.66, -16.28) * mm});
            skLineSegment(sketch, "E1904", {"start": v(25.66, -16.28) * mm, "end": v(25.68, -16.2) * mm});
            skLineSegment(sketch, "E1905", {"start": v(25.68, -16.2) * mm, "end": v(25.68, -16.17) * mm});
            skLineSegment(sketch, "E1906", {"start": v(25.68, -16.17) * mm, "end": v(25.68, -16.14) * mm});
            skLineSegment(sketch, "E1907", {"start": v(25.68, -16.14) * mm, "end": v(25.67, -16.06) * mm});
            skLineSegment(sketch, "E1908", {"start": v(25.67, -16.06) * mm, "end": v(25.64, -15.95) * mm});
            skLineSegment(sketch, "E1909", {"start": v(25.64, -15.95) * mm, "end": v(25.56, -15.85) * mm});
            skLineSegment(sketch, "E1910", {"start": v(25.56, -15.85) * mm, "end": v(25.42, -15.74) * mm});
            skLineSegment(sketch, "E1911", {"start": v(25.42, -15.74) * mm, "end": v(25.2, -15.6) * mm});
            skLineSegment(sketch, "E1912", {"start": v(25.2, -15.6) * mm, "end": v(24.88, -15.42) * mm});
            skLineSegment(sketch, "E1913", {"start": v(24.88, -15.42) * mm, "end": v(24.45, -15.19) * mm});
            skLineSegment(sketch, "E1914", {"start": v(24.45, -15.19) * mm, "end": v(24.03, -14.97) * mm});
            skLineSegment(sketch, "E1915", {"start": v(24.03, -14.97) * mm, "end": v(23.89, -14.9) * mm});
            skLineSegment(sketch, "E1916", {"start": v(23.89, -14.9) * mm, "end": v(23.8, -14.86) * mm});
            skLineSegment(sketch, "E1917", {"start": v(23.8, -14.86) * mm, "end": v(23.58, -14.74) * mm});
            skLineSegment(sketch, "E1918", {"start": v(23.58, -14.74) * mm, "end": v(23.32, -14.6) * mm});
            skLineSegment(sketch, "E1919", {"start": v(23.32, -14.6) * mm, "end": v(23.13, -14.5) * mm});
            skLineSegment(sketch, "E1920", {"start": v(23.13, -14.5) * mm, "end": v(23.06, -14.46) * mm});
            skLineSegment(sketch, "E1921", {"start": v(23.06, -14.46) * mm, "end": v(23.06, -14.46) * mm});
            skLineSegment(sketch, "E1922", {"start": v(23.06, -14.46) * mm, "end": v(23.05, -14.45) * mm});
            skLineSegment(sketch, "E1923", {"start": v(23.05, -14.45) * mm, "end": v(23.03, -14.36) * mm});
            skLineSegment(sketch, "E1924", {"start": v(23.03, -14.36) * mm, "end": v(22.99, -14.11) * mm});
            skLineSegment(sketch, "E1925", {"start": v(22.99, -14.11) * mm, "end": v(22.95, -13.72) * mm});
            skLineSegment(sketch, "E1926", {"start": v(22.95, -13.72) * mm, "end": v(22.9, -13.31) * mm});
            skLineSegment(sketch, "E1927", {"start": v(22.9, -13.31) * mm, "end": v(22.9, -13.18) * mm});
            skLineSegment(sketch, "E1928", {"start": v(22.9, -13.18) * mm, "end": v(22.9, -13.16) * mm});
            skLineSegment(sketch, "E1929", {"start": v(22.9, -13.16) * mm, "end": v(22.88, -12.95) * mm});
            skLineSegment(sketch, "E1930", {"start": v(22.88, -12.95) * mm, "end": v(22.85, -12.7) * mm});
            skLineSegment(sketch, "E1931", {"start": v(22.85, -12.7) * mm, "end": v(22.85, -12.64) * mm});
            skLineSegment(sketch, "E1932", {"start": v(22.85, -12.64) * mm, "end": v(22.84, -12.6) * mm});
            skLineSegment(sketch, "E1933", {"start": v(22.84, -12.6) * mm, "end": v(22.83, -12.44) * mm});
            skLineSegment(sketch, "E1934", {"start": v(22.83, -12.44) * mm, "end": v(22.8, -12.15) * mm});
            skLineSegment(sketch, "E1935", {"start": v(22.8, -12.15) * mm, "end": v(22.77, -11.83) * mm});
            skLineSegment(sketch, "E1936", {"start": v(22.77, -11.83) * mm, "end": v(22.75, -11.58) * mm});
            skLineSegment(sketch, "E1937", {"start": v(22.75, -11.58) * mm, "end": v(22.74, -11.5) * mm});
            skLineSegment(sketch, "E1938", {"start": v(22.74, -11.5) * mm, "end": v(22.74, -11.42) * mm});
            skLineSegment(sketch, "E1939", {"start": v(22.74, -11.42) * mm, "end": v(22.71, -11.16) * mm});
            skLineSegment(sketch, "E1940", {"start": v(22.71, -11.16) * mm, "end": v(22.68, -10.8) * mm});
            skLineSegment(sketch, "E1941", {"start": v(22.68, -10.8) * mm, "end": v(22.65, -10.48) * mm});
            skLineSegment(sketch, "E1942", {"start": v(22.65, -10.48) * mm, "end": v(22.63, -10.29) * mm});
            skLineSegment(sketch, "E1943", {"start": v(22.63, -10.29) * mm, "end": v(22.63, -10.22) * mm});
            skLineSegment(sketch, "E1944", {"start": v(22.63, -10.22) * mm, "end": v(22.62, -10.17) * mm});
            skLineSegment(sketch, "E1945", {"start": v(22.62, -10.17) * mm, "end": v(22.6, -10.01) * mm});
            skLineSegment(sketch, "E1946", {"start": v(22.6, -10.01) * mm, "end": v(22.59, -9.8) * mm});
            skLineSegment(sketch, "E1947", {"start": v(22.59, -9.8) * mm, "end": v(22.57, -9.63) * mm});
            skLineSegment(sketch, "E1948", {"start": v(22.57, -9.63) * mm, "end": v(22.56, -9.53) * mm});
            skLineSegment(sketch, "E1949", {"start": v(22.56, -9.53) * mm, "end": v(22.56, -9.5) * mm});
            skLineSegment(sketch, "E1950", {"start": v(22.56, -9.5) * mm, "end": v(22.56, -9.45) * mm});
            skLineSegment(sketch, "E1951", {"start": v(22.56, -9.45) * mm, "end": v(22.54, -9.31) * mm});
            skLineSegment(sketch, "E1952", {"start": v(22.54, -9.31) * mm, "end": v(22.51, -8.97) * mm});
            skLineSegment(sketch, "E1953", {"start": v(22.51, -8.97) * mm, "end": v(22.47, -8.52) * mm});
            skLineSegment(sketch, "E1954", {"start": v(22.47, -8.52) * mm, "end": v(22.43, -8.02) * mm});
            skLineSegment(sketch, "E1955", {"start": v(22.43, -8.02) * mm, "end": v(22.38, -7.53) * mm});
            skLineSegment(sketch, "E1956", {"start": v(22.38, -7.53) * mm, "end": v(22.34, -7.09) * mm});
            skLineSegment(sketch, "E1957", {"start": v(22.34, -7.09) * mm, "end": v(22.31, -6.75) * mm});
            skLineSegment(sketch, "E1958", {"start": v(22.31, -6.75) * mm, "end": v(22.3, -6.61) * mm});
            skLineSegment(sketch, "E1959", {"start": v(22.3, -6.61) * mm, "end": v(22.3, -6.56) * mm});
            skLineSegment(sketch, "E1960", {"start": v(22.3, -6.56) * mm, "end": v(22.3, -6.54) * mm});
            skLineSegment(sketch, "E1961", {"start": v(22.3, -6.54) * mm, "end": v(22.28, -6.38) * mm});
            skLineSegment(sketch, "E1962", {"start": v(22.28, -6.38) * mm, "end": v(22.26, -6.2) * mm});
            skLineSegment(sketch, "E1963", {"start": v(22.26, -6.2) * mm, "end": v(22.26, -6.18) * mm});
            skLineSegment(sketch, "E1964", {"start": v(22.26, -6.18) * mm, "end": v(22.25, -6.15) * mm});
            skLineSegment(sketch, "E1965", {"start": v(22.25, -6.15) * mm, "end": v(22.24, -6) * mm});
            skLineSegment(sketch, "E1966", {"start": v(22.24, -6) * mm, "end": v(22.21, -5.7) * mm});
            skLineSegment(sketch, "E1967", {"start": v(22.21, -5.7) * mm, "end": v(22.18, -5.32) * mm});
            skLineSegment(sketch, "E1968", {"start": v(22.18, -5.32) * mm, "end": v(22.15, -5) * mm});
            skLineSegment(sketch, "E1969", {"start": v(22.15, -5) * mm, "end": v(22.14, -4.89) * mm});
            skLineSegment(sketch, "E1970", {"start": v(22.14, -4.89) * mm, "end": v(22.13, -4.78) * mm});
            skLineSegment(sketch, "E1971", {"start": v(22.13, -4.78) * mm, "end": v(22.1, -4.45) * mm});
            skLineSegment(sketch, "E1972", {"start": v(22.1, -4.45) * mm, "end": v(22.06, -4.06) * mm});
            skLineSegment(sketch, "E1973", {"start": v(22.06, -4.06) * mm, "end": v(22.04, -3.76) * mm});
            skLineSegment(sketch, "E1974", {"start": v(22.04, -3.76) * mm, "end": v(22.02, -3.62) * mm});
            skLineSegment(sketch, "E1975", {"start": v(22.02, -3.62) * mm, "end": v(22.02, -3.6) * mm});
            skLineSegment(sketch, "E1976", {"start": v(22.02, -3.6) * mm, "end": v(22, -3.37) * mm});
            skLineSegment(sketch, "E1977", {"start": v(22, -3.37) * mm, "end": v(21.83, -3.28) * mm});
            skLineSegment(sketch, "E1978", {"start": v(21.83, -3.28) * mm, "end": v(21.76, -3.24) * mm});
            skLineSegment(sketch, "E1979", {"start": v(21.76, -3.24) * mm, "end": v(21.56, -3.14) * mm});
            skLineSegment(sketch, "E1980", {"start": v(21.56, -3.14) * mm, "end": v(21.3, -3) * mm});
            skLineSegment(sketch, "E1981", {"start": v(21.3, -3) * mm, "end": v(21.1, -2.9) * mm});
            skLineSegment(sketch, "E1982", {"start": v(21.1, -2.9) * mm, "end": v(20.9, -2.8) * mm});
            skLineSegment(sketch, "E1983", {"start": v(20.9, -2.8) * mm, "end": v(20.75, -2.72) * mm});
            skLineSegment(sketch, "E1984", {"start": v(20.75, -2.72) * mm, "end": v(20.63, -2.67) * mm});
            skLineSegment(sketch, "E1985", {"start": v(20.63, -2.67) * mm, "end": v(20.55, -2.63) * mm});
            skLineSegment(sketch, "E1986", {"start": v(20.55, -2.63) * mm, "end": v(20.52, -2.62) * mm});
            skLineSegment(sketch, "E1987", {"start": v(20.52, -2.62) * mm, "end": v(20.51, -2.62) * mm});
            skLineSegment(sketch, "E1988", {"start": v(20.51, -2.62) * mm, "end": v(20.5, -2.62) * mm});
            skLineSegment(sketch, "E1989", {"start": v(20.5, -2.62) * mm, "end": v(20.5, -2.64) * mm});
            skLineSegment(sketch, "E1990", {"start": v(20.5, -2.64) * mm, "end": v(20.47, -2.72) * mm});
            skLineSegment(sketch, "E1991", {"start": v(20.47, -2.72) * mm, "end": v(20.45, -2.86) * mm});
            skLineSegment(sketch, "E1992", {"start": v(20.45, -2.86) * mm, "end": v(20.44, -3) * mm});
            skLineSegment(sketch, "E1993", {"start": v(20.44, -3) * mm, "end": v(20.43, -3.05) * mm});
            skLineSegment(sketch, "E1994", {"start": v(20.43, -3.05) * mm, "end": v(20.43, -3.1) * mm});
            skLineSegment(sketch, "E1995", {"start": v(20.43, -3.1) * mm, "end": v(20.4, -3.47) * mm});
            skLineSegment(sketch, "E1996", {"start": v(20.4, -3.47) * mm, "end": v(20.35, -3.82) * mm});
            skLineSegment(sketch, "E1997", {"start": v(20.35, -3.82) * mm, "end": v(20.35, -3.88) * mm});
            skLineSegment(sketch, "E1998", {"start": v(20.35, -3.88) * mm, "end": v(20.34, -3.92) * mm});
            skLineSegment(sketch, "E1999", {"start": v(20.34, -3.92) * mm, "end": v(20.33, -4.05) * mm});
            skLineSegment(sketch, "E2000", {"start": v(20.33, -4.05) * mm, "end": v(20.3, -4.22) * mm});
            skLineSegment(sketch, "E2001", {"start": v(20.3, -4.22) * mm, "end": v(20.3, -4.36) * mm});
            skLineSegment(sketch, "E2002", {"start": v(20.3, -4.36) * mm, "end": v(20.28, -4.44) * mm});
            skLineSegment(sketch, "E2003", {"start": v(20.28, -4.44) * mm, "end": v(20.28, -4.47) * mm});
            skLineSegment(sketch, "E2004", {"start": v(20.28, -4.47) * mm, "end": v(20.28, -4.5) * mm});
            skLineSegment(sketch, "E2005", {"start": v(20.28, -4.5) * mm, "end": v(20.27, -4.57) * mm});
            skLineSegment(sketch, "E2006", {"start": v(20.27, -4.57) * mm, "end": v(20.25, -4.73) * mm});
            skLineSegment(sketch, "E2007", {"start": v(20.25, -4.73) * mm, "end": v(20.23, -4.92) * mm});
            skLineSegment(sketch, "E2008", {"start": v(20.23, -4.92) * mm, "end": v(20.21, -5.07) * mm});
            skLineSegment(sketch, "E2009", {"start": v(20.21, -5.07) * mm, "end": v(20.2, -5.12) * mm});
            skLineSegment(sketch, "E2010", {"start": v(20.2, -5.12) * mm, "end": v(20.2, -5.17) * mm});
            skLineSegment(sketch, "E2011", {"start": v(20.2, -5.17) * mm, "end": v(20.18, -5.34) * mm});
            skLineSegment(sketch, "E2012", {"start": v(20.18, -5.34) * mm, "end": v(20.16, -5.58) * mm});
            skLineSegment(sketch, "E2013", {"start": v(20.16, -5.58) * mm, "end": v(20.13, -5.81) * mm});
            skLineSegment(sketch, "E2014", {"start": v(20.13, -5.81) * mm, "end": v(20.11, -5.96) * mm});
            skLineSegment(sketch, "E2015", {"start": v(20.11, -5.96) * mm, "end": v(20.1, -6.01) * mm});
            skLineSegment(sketch, "E2016", {"start": v(20.1, -6.01) * mm, "end": v(20.1, -6.05) * mm});
            skLineSegment(sketch, "E2017", {"start": v(20.1, -6.05) * mm, "end": v(20.09, -6.17) * mm});
            skLineSegment(sketch, "E2018", {"start": v(20.09, -6.17) * mm, "end": v(20.07, -6.3) * mm});
            skLineSegment(sketch, "E2019", {"start": v(20.07, -6.3) * mm, "end": v(20.06, -6.4) * mm});
            skLineSegment(sketch, "E2020", {"start": v(20.06, -6.4) * mm, "end": v(20.06, -6.44) * mm});
            skLineSegment(sketch, "E2021", {"start": v(20.06, -6.44) * mm, "end": v(20.06, -6.44) * mm});
            skLineSegment(sketch, "E2022", {"start": v(20.06, -6.44) * mm, "end": v(20.02, -6.44) * mm});
            skLineSegment(sketch, "E2023", {"start": v(20.02, -6.44) * mm, "end": v(19.96, -6.45) * mm});
            skLineSegment(sketch, "E2024", {"start": v(19.96, -6.45) * mm, "end": v(19.94, -6.45) * mm});
            skLineSegment(sketch, "E2025", {"start": v(19.94, -6.45) * mm, "end": v(19.93, -6.45) * mm});
            skLineSegment(sketch, "E2026", {"start": v(19.93, -6.45) * mm, "end": v(19.9, -6.45) * mm});
            skLineSegment(sketch, "E2027", {"start": v(19.9, -6.45) * mm, "end": v(19.86, -6.45) * mm});
            skLineSegment(sketch, "E2028", {"start": v(19.86, -6.45) * mm, "end": v(19.84, -6.47) * mm});
            skLineSegment(sketch, "E2029", {"start": v(19.84, -6.47) * mm, "end": v(19.82, -6.5) * mm});
            skLineSegment(sketch, "E2030", {"start": v(19.82, -6.5) * mm, "end": v(19.8, -6.58) * mm});
            skLineSegment(sketch, "E2031", {"start": v(19.8, -6.58) * mm, "end": v(19.77, -6.7) * mm});
            skLineSegment(sketch, "E2032", {"start": v(19.77, -6.7) * mm, "end": v(19.73, -6.86) * mm});
            skLineSegment(sketch, "E2033", {"start": v(19.73, -6.86) * mm, "end": v(19.7, -7.03) * mm});
            skLineSegment(sketch, "E2034", {"start": v(19.7, -7.03) * mm, "end": v(19.69, -7.08) * mm});
            skLineSegment(sketch, "E2035", {"start": v(19.69, -7.08) * mm, "end": v(19.68, -7.14) * mm});
            skLineSegment(sketch, "E2036", {"start": v(19.68, -7.14) * mm, "end": v(19.65, -7.29) * mm});
            skLineSegment(sketch, "E2037", {"start": v(19.65, -7.29) * mm, "end": v(19.6, -7.46) * mm});
            skLineSegment(sketch, "E2038", {"start": v(19.6, -7.46) * mm, "end": v(19.58, -7.58) * mm});
            skLineSegment(sketch, "E2039", {"start": v(19.58, -7.58) * mm, "end": v(19.57, -7.63) * mm});
            skLineSegment(sketch, "E2040", {"start": v(19.57, -7.63) * mm, "end": v(19.57, -7.63) * mm});
            skLineSegment(sketch, "E2041", {"start": v(19.57, -7.63) * mm, "end": v(19.56, -7.63) * mm});
            skLineSegment(sketch, "E2042", {"start": v(19.56, -7.63) * mm, "end": v(19.52, -7.64) * mm});
            skLineSegment(sketch, "E2043", {"start": v(19.52, -7.64) * mm, "end": v(19.46, -7.64) * mm});
            skLineSegment(sketch, "E2044", {"start": v(19.46, -7.64) * mm, "end": v(19.45, -7.63) * mm});
            skLineSegment(sketch, "E2045", {"start": v(19.45, -7.63) * mm, "end": v(19.43, -7.63) * mm});
            skLineSegment(sketch, "E2046", {"start": v(19.43, -7.63) * mm, "end": v(19.38, -7.63) * mm});
            skLineSegment(sketch, "E2047", {"start": v(19.38, -7.63) * mm, "end": v(19.32, -7.64) * mm});
            skLineSegment(sketch, "E2048", {"start": v(19.32, -7.64) * mm, "end": v(19.3, -7.68) * mm});
            skLineSegment(sketch, "E2049", {"start": v(19.3, -7.68) * mm, "end": v(19.28, -7.72) * mm});
            skLineSegment(sketch, "E2050", {"start": v(19.28, -7.72) * mm, "end": v(19.28, -7.78) * mm});
            skLineSegment(sketch, "E2051", {"start": v(19.28, -7.78) * mm, "end": v(19.3, -7.85) * mm});
            skLineSegment(sketch, "E2052", {"start": v(19.3, -7.85) * mm, "end": v(19.35, -7.92) * mm});
            skLineSegment(sketch, "E2053", {"start": v(19.35, -7.92) * mm, "end": v(19.4, -7.98) * mm});
            skLineSegment(sketch, "E2054", {"start": v(19.4, -7.98) * mm, "end": v(19.4, -8) * mm});
            skLineSegment(sketch, "E2055", {"start": v(19.4, -8) * mm, "end": v(19.42, -8) * mm});
            skLineSegment(sketch, "E2056", {"start": v(19.42, -8) * mm, "end": v(19.44, -8.03) * mm});
            skLineSegment(sketch, "E2057", {"start": v(19.44, -8.03) * mm, "end": v(19.46, -8.06) * mm});
            skLineSegment(sketch, "E2058", {"start": v(19.46, -8.06) * mm, "end": v(19.47, -8.1) * mm});
            skLineSegment(sketch, "E2059", {"start": v(19.47, -8.1) * mm, "end": v(19.48, -8.16) * mm});
            skLineSegment(sketch, "E2060", {"start": v(19.48, -8.16) * mm, "end": v(19.47, -8.25) * mm});
            skLineSegment(sketch, "E2061", {"start": v(19.47, -8.25) * mm, "end": v(19.45, -8.38) * mm});
            skLineSegment(sketch, "E2062", {"start": v(19.45, -8.38) * mm, "end": v(19.41, -8.55) * mm});
            skLineSegment(sketch, "E2063", {"start": v(19.41, -8.55) * mm, "end": v(19.38, -8.72) * mm});
            skLineSegment(sketch, "E2064", {"start": v(19.38, -8.72) * mm, "end": v(19.37, -8.78) * mm});
            skLineSegment(sketch, "E2065", {"start": v(19.37, -8.78) * mm, "end": v(19.36, -8.84) * mm});
            skLineSegment(sketch, "E2066", {"start": v(19.36, -8.84) * mm, "end": v(19.3, -9.18) * mm});
            skLineSegment(sketch, "E2067", {"start": v(19.3, -9.18) * mm, "end": v(19.23, -9.52) * mm});
            skLineSegment(sketch, "E2068", {"start": v(19.23, -9.52) * mm, "end": v(19.22, -9.57) * mm});
            skLineSegment(sketch, "E2069", {"start": v(19.22, -9.57) * mm, "end": v(19.21, -9.6) * mm});
            skLineSegment(sketch, "E2070", {"start": v(19.21, -9.6) * mm, "end": v(19.2, -9.73) * mm});
            skLineSegment(sketch, "E2071", {"start": v(19.2, -9.73) * mm, "end": v(19.16, -9.88) * mm});
            skLineSegment(sketch, "E2072", {"start": v(19.16, -9.88) * mm, "end": v(19.14, -10) * mm});
            skLineSegment(sketch, "E2073", {"start": v(19.14, -10) * mm, "end": v(19.13, -10.06) * mm});
            skLineSegment(sketch, "E2074", {"start": v(19.13, -10.06) * mm, "end": v(19.12, -10.07) * mm});
            skLineSegment(sketch, "E2075", {"start": v(19.12, -10.07) * mm, "end": v(19.12, -10.09) * mm});
            skLineSegment(sketch, "E2076", {"start": v(19.12, -10.09) * mm, "end": v(19.1, -10.2) * mm});
            skLineSegment(sketch, "E2077", {"start": v(19.1, -10.2) * mm, "end": v(19.07, -10.31) * mm});
            skLineSegment(sketch, "E2078", {"start": v(19.07, -10.31) * mm, "end": v(19.07, -10.33) * mm});
            skLineSegment(sketch, "E2079", {"start": v(19.07, -10.33) * mm, "end": v(19.04, -10.47) * mm});
            skLineSegment(sketch, "E2080", {"start": v(19.04, -10.47) * mm, "end": v(18.9, -10.45) * mm});
            skLineSegment(sketch, "E2081", {"start": v(18.9, -10.45) * mm, "end": v(18.88, -10.45) * mm});
            skLineSegment(sketch, "E2082", {"start": v(18.88, -10.45) * mm, "end": v(18.81, -10.44) * mm});
            skLineSegment(sketch, "E2083", {"start": v(18.81, -10.44) * mm, "end": v(18.77, -10.45) * mm});
            skLineSegment(sketch, "E2084", {"start": v(18.77, -10.45) * mm, "end": v(18.75, -10.47) * mm});
            skLineSegment(sketch, "E2085", {"start": v(18.75, -10.47) * mm, "end": v(18.75, -10.5) * mm});
            skLineSegment(sketch, "E2086", {"start": v(18.75, -10.5) * mm, "end": v(18.75, -10.52) * mm});
            skLineSegment(sketch, "E2087", {"start": v(18.75, -10.52) * mm, "end": v(18.75, -10.53) * mm});
            skLineSegment(sketch, "E2088", {"start": v(18.75, -10.53) * mm, "end": v(18.76, -10.56) * mm});
            skLineSegment(sketch, "E2089", {"start": v(18.76, -10.56) * mm, "end": v(18.78, -10.62) * mm});
            skLineSegment(sketch, "E2090", {"start": v(18.78, -10.62) * mm, "end": v(18.81, -10.68) * mm});
            skLineSegment(sketch, "E2091", {"start": v(18.81, -10.68) * mm, "end": v(18.84, -10.73) * mm});
            skLineSegment(sketch, "E2092", {"start": v(18.84, -10.73) * mm, "end": v(18.85, -10.75) * mm});
            skLineSegment(sketch, "E2093", {"start": v(18.85, -10.75) * mm, "end": v(18.96, -10.9) * mm});
            skLineSegment(sketch, "E2094", {"start": v(18.96, -10.9) * mm, "end": v(18.84, -11.55) * mm});
            skLineSegment(sketch, "E2095", {"start": v(18.84, -11.55) * mm, "end": v(18.82, -11.61) * mm});
            skLineSegment(sketch, "E2096", {"start": v(18.82, -11.61) * mm, "end": v(18.78, -11.81) * mm});
            skLineSegment(sketch, "E2097", {"start": v(18.78, -11.81) * mm, "end": v(18.74, -12.04) * mm});
            skLineSegment(sketch, "E2098", {"start": v(18.74, -12.04) * mm, "end": v(18.7, -12.2) * mm});
            skLineSegment(sketch, "E2099", {"start": v(18.7, -12.2) * mm, "end": v(18.7, -12.28) * mm});
            skLineSegment(sketch, "E2100", {"start": v(18.7, -12.28) * mm, "end": v(18.7, -12.3) * mm});
            skLineSegment(sketch, "E2101", {"start": v(18.7, -12.3) * mm, "end": v(18.7, -12.3) * mm});
            skLineSegment(sketch, "E2102", {"start": v(18.7, -12.3) * mm, "end": v(18.69, -12.35) * mm});
            skLineSegment(sketch, "E2103", {"start": v(18.69, -12.35) * mm, "end": v(18.7, -12.39) * mm});
            skLineSegment(sketch, "E2104", {"start": v(18.7, -12.39) * mm, "end": v(18.75, -12.42) * mm});
            skLineSegment(sketch, "E2105", {"start": v(18.75, -12.42) * mm, "end": v(18.8, -12.45) * mm});
            skLineSegment(sketch, "E2106", {"start": v(18.8, -12.45) * mm, "end": v(18.83, -12.46) * mm});
            skLineSegment(sketch, "E2107", {"start": v(18.83, -12.46) * mm, "end": v(18.84, -12.47) * mm});
            skLineSegment(sketch, "E2108", {"start": v(18.84, -12.47) * mm, "end": v(18.89, -12.5) * mm});
            skLineSegment(sketch, "E2109", {"start": v(18.89, -12.5) * mm, "end": v(18.94, -12.53) * mm});
            skLineSegment(sketch, "E2110", {"start": v(18.94, -12.53) * mm, "end": v(18.97, -12.56) * mm});
            skLineSegment(sketch, "E2111", {"start": v(18.97, -12.56) * mm, "end": v(18.98, -12.57) * mm});
            skLineSegment(sketch, "E2112", {"start": v(18.98, -12.57) * mm, "end": v(18.98, -12.58) * mm});
            skLineSegment(sketch, "E2113", {"start": v(18.98, -12.58) * mm, "end": v(18.98, -12.59) * mm});
            skLineSegment(sketch, "E2114", {"start": v(18.98, -12.59) * mm, "end": v(18.98, -12.61) * mm});
            skLineSegment(sketch, "E2115", {"start": v(18.98, -12.61) * mm, "end": v(18.96, -12.68) * mm});
            skLineSegment(sketch, "E2116", {"start": v(18.96, -12.68) * mm, "end": v(18.93, -12.78) * mm});
            skLineSegment(sketch, "E2117", {"start": v(18.93, -12.78) * mm, "end": v(18.9, -12.85) * mm});
            skLineSegment(sketch, "E2118", {"start": v(18.9, -12.85) * mm, "end": v(18.9, -12.88) * mm});
            skLineSegment(sketch, "E2119", {"start": v(18.9, -12.88) * mm, "end": v(18.89, -12.9) * mm});
            skLineSegment(sketch, "E2120", {"start": v(18.89, -12.9) * mm, "end": v(18.86, -13) * mm});
            skLineSegment(sketch, "E2121", {"start": v(18.86, -13) * mm, "end": v(18.82, -13.12) * mm});
            skLineSegment(sketch, "E2122", {"start": v(18.82, -13.12) * mm, "end": v(18.79, -13.24) * mm});
            skLineSegment(sketch, "E2123", {"start": v(18.79, -13.24) * mm, "end": v(18.77, -13.31) * mm});
            skLineSegment(sketch, "E2124", {"start": v(18.77, -13.31) * mm, "end": v(18.76, -13.34) * mm});
            skLineSegment(sketch, "E2125", {"start": v(18.76, -13.34) * mm, "end": v(18.76, -13.35) * mm});
            skLineSegment(sketch, "E2126", {"start": v(18.76, -13.35) * mm, "end": v(18.74, -13.4) * mm});
            skLineSegment(sketch, "E2127", {"start": v(18.74, -13.4) * mm, "end": v(18.72, -13.46) * mm});
            skLineSegment(sketch, "E2128", {"start": v(18.72, -13.46) * mm, "end": v(18.7, -13.5) * mm});
            skLineSegment(sketch, "E2129", {"start": v(18.7, -13.5) * mm, "end": v(18.67, -13.52) * mm});
            skLineSegment(sketch, "E2130", {"start": v(18.67, -13.52) * mm, "end": v(18.64, -13.53) * mm});
            skLineSegment(sketch, "E2131", {"start": v(18.64, -13.53) * mm, "end": v(18.6, -13.52) * mm});
            skLineSegment(sketch, "E2132", {"start": v(18.6, -13.52) * mm, "end": v(18.55, -13.5) * mm});
            skLineSegment(sketch, "E2133", {"start": v(18.55, -13.5) * mm, "end": v(18.5, -13.49) * mm});
            skLineSegment(sketch, "E2134", {"start": v(18.5, -13.49) * mm, "end": v(18.49, -13.48) * mm});
            skLineSegment(sketch, "E2135", {"start": v(18.49, -13.48) * mm, "end": v(18.47, -13.48) * mm});
            skLineSegment(sketch, "E2136", {"start": v(18.47, -13.48) * mm, "end": v(18.4, -13.45) * mm});
            skLineSegment(sketch, "E2137", {"start": v(18.4, -13.45) * mm, "end": v(18.34, -13.43) * mm});
            skLineSegment(sketch, "E2138", {"start": v(18.34, -13.43) * mm, "end": v(18.33, -13.43) * mm});
            skLineSegment(sketch, "E2139", {"start": v(18.33, -13.43) * mm, "end": v(18.32, -13.43) * mm});
            skLineSegment(sketch, "E2140", {"start": v(18.32, -13.43) * mm, "end": v(18.3, -13.45) * mm});
            skLineSegment(sketch, "E2141", {"start": v(18.3, -13.45) * mm, "end": v(18.27, -13.5) * mm});
            skLineSegment(sketch, "E2142", {"start": v(18.27, -13.5) * mm, "end": v(18.22, -13.56) * mm});
            skLineSegment(sketch, "E2143", {"start": v(18.22, -13.56) * mm, "end": v(18.2, -13.63) * mm});
            skLineSegment(sketch, "E2144", {"start": v(18.2, -13.63) * mm, "end": v(18.18, -13.65) * mm});
            skLineSegment(sketch, "E2145", {"start": v(18.18, -13.65) * mm, "end": v(18.17, -13.67) * mm});
            skLineSegment(sketch, "E2146", {"start": v(18.17, -13.67) * mm, "end": v(18.14, -13.73) * mm});
            skLineSegment(sketch, "E2147", {"start": v(18.14, -13.73) * mm, "end": v(18.1, -13.8) * mm});
            skLineSegment(sketch, "E2148", {"start": v(18.1, -13.8) * mm, "end": v(18.07, -13.85) * mm});
            skLineSegment(sketch, "E2149", {"start": v(18.07, -13.85) * mm, "end": v(18.05, -13.87) * mm});
            skLineSegment(sketch, "E2150", {"start": v(18.05, -13.87) * mm, "end": v(18.05, -13.87) * mm});
            skLineSegment(sketch, "E2151", {"start": v(18.05, -13.87) * mm, "end": v(18.04, -13.87) * mm});
            skLineSegment(sketch, "E2152", {"start": v(18.04, -13.87) * mm, "end": v(18, -13.86) * mm});
            skLineSegment(sketch, "E2153", {"start": v(18, -13.86) * mm, "end": v(17.93, -13.84) * mm});
            skLineSegment(sketch, "E2154", {"start": v(17.93, -13.84) * mm, "end": v(17.91, -13.83) * mm});
            skLineSegment(sketch, "E2155", {"start": v(17.91, -13.83) * mm, "end": v(17.9, -13.82) * mm});
            skLineSegment(sketch, "E2156", {"start": v(17.9, -13.82) * mm, "end": v(17.84, -13.81) * mm});
            skLineSegment(sketch, "E2157", {"start": v(17.84, -13.81) * mm, "end": v(17.78, -13.8) * mm});
            skLineSegment(sketch, "E2158", {"start": v(17.78, -13.8) * mm, "end": v(17.74, -13.82) * mm});
            skLineSegment(sketch, "E2159", {"start": v(17.74, -13.82) * mm, "end": v(17.73, -13.84) * mm});
            skLineSegment(sketch, "E2160", {"start": v(17.73, -13.84) * mm, "end": v(17.73, -13.87) * mm});
            skLineSegment(sketch, "E2161", {"start": v(17.73, -13.87) * mm, "end": v(17.75, -13.91) * mm});
            skLineSegment(sketch, "E2162", {"start": v(17.75, -13.91) * mm, "end": v(17.8, -13.96) * mm});
            skLineSegment(sketch, "E2163", {"start": v(17.8, -13.96) * mm, "end": v(17.84, -14) * mm});
            skLineSegment(sketch, "E2164", {"start": v(17.84, -14) * mm, "end": v(17.86, -14) * mm});
            skLineSegment(sketch, "E2165", {"start": v(17.86, -14) * mm, "end": v(17.88, -14.02) * mm});
            skLineSegment(sketch, "E2166", {"start": v(17.88, -14.02) * mm, "end": v(17.94, -14.07) * mm});
            skLineSegment(sketch, "E2167", {"start": v(17.94, -14.07) * mm, "end": v(17.98, -14.1) * mm});
            skLineSegment(sketch, "E2168", {"start": v(17.98, -14.1) * mm, "end": v(17.98, -14.12) * mm});
            skLineSegment(sketch, "E2169", {"start": v(17.98, -14.12) * mm, "end": v(17.98, -14.13) * mm});
            skLineSegment(sketch, "E2170", {"start": v(17.98, -14.13) * mm, "end": v(17.97, -14.15) * mm});
            skLineSegment(sketch, "E2171", {"start": v(17.97, -14.15) * mm, "end": v(17.96, -14.2) * mm});
            skLineSegment(sketch, "E2172", {"start": v(17.96, -14.2) * mm, "end": v(17.94, -14.26) * mm});
            skLineSegment(sketch, "E2173", {"start": v(17.94, -14.26) * mm, "end": v(17.9, -14.33) * mm});
            skLineSegment(sketch, "E2174", {"start": v(17.9, -14.33) * mm, "end": v(17.88, -14.41) * mm});
            skLineSegment(sketch, "E2175", {"start": v(17.88, -14.41) * mm, "end": v(17.84, -14.5) * mm});
            skLineSegment(sketch, "E2176", {"start": v(17.84, -14.5) * mm, "end": v(17.8, -14.58) * mm});
            skLineSegment(sketch, "E2177", {"start": v(17.8, -14.58) * mm, "end": v(17.78, -14.64) * mm});
            skLineSegment(sketch, "E2178", {"start": v(17.78, -14.64) * mm, "end": v(17.77, -14.66) * mm});
            skLineSegment(sketch, "E2179", {"start": v(17.77, -14.66) * mm, "end": v(17.77, -14.67) * mm});
            skLineSegment(sketch, "E2180", {"start": v(17.77, -14.67) * mm, "end": v(17.75, -14.72) * mm});
            skLineSegment(sketch, "E2181", {"start": v(17.75, -14.72) * mm, "end": v(17.7, -14.82) * mm});
            skLineSegment(sketch, "E2182", {"start": v(17.7, -14.82) * mm, "end": v(17.64, -14.97) * mm});
            skLineSegment(sketch, "E2183", {"start": v(17.64, -14.97) * mm, "end": v(17.57, -15.14) * mm});
            skLineSegment(sketch, "E2184", {"start": v(17.57, -15.14) * mm, "end": v(17.5, -15.34) * mm});
            skLineSegment(sketch, "E2185", {"start": v(17.5, -15.34) * mm, "end": v(17.41, -15.54) * mm});
            skLineSegment(sketch, "E2186", {"start": v(17.41, -15.54) * mm, "end": v(17.33, -15.75) * mm});
            skLineSegment(sketch, "E2187", {"start": v(17.33, -15.75) * mm, "end": v(17.27, -15.9) * mm});
            skLineSegment(sketch, "E2188", {"start": v(17.27, -15.9) * mm, "end": v(17.25, -15.95) * mm});
            skLineSegment(sketch, "E2189", {"start": v(17.25, -15.95) * mm, "end": v(17.23, -15.99) * mm});
            skLineSegment(sketch, "E2190", {"start": v(17.23, -15.99) * mm, "end": v(17.19, -16.1) * mm});
            skLineSegment(sketch, "E2191", {"start": v(17.19, -16.1) * mm, "end": v(17.13, -16.23) * mm});
            skLineSegment(sketch, "E2192", {"start": v(17.13, -16.23) * mm, "end": v(17.1, -16.31) * mm});
            skLineSegment(sketch, "E2193", {"start": v(17.1, -16.31) * mm, "end": v(17.08, -16.35) * mm});
            skLineSegment(sketch, "E2194", {"start": v(17.08, -16.35) * mm, "end": v(17.08, -16.35) * mm});
            skLineSegment(sketch, "E2195", {"start": v(17.08, -16.35) * mm, "end": v(17.02, -16.34) * mm});
            skLineSegment(sketch, "E2196", {"start": v(17.02, -16.34) * mm, "end": v(16.89, -16.27) * mm});
            skLineSegment(sketch, "E2197", {"start": v(16.89, -16.27) * mm, "end": v(16.68, -16.17) * mm});
            skLineSegment(sketch, "E2198", {"start": v(16.68, -16.17) * mm, "end": v(16.48, -16.06) * mm});
            skLineSegment(sketch, "E2199", {"start": v(16.48, -16.06) * mm, "end": v(16.41, -16.02) * mm});
            skLineSegment(sketch, "E2200", {"start": v(16.41, -16.02) * mm, "end": v(16.38, -16) * mm});
            skLineSegment(sketch, "E2201", {"start": v(16.38, -16) * mm, "end": v(16.27, -15.94) * mm});
            skLineSegment(sketch, "E2202", {"start": v(16.27, -15.94) * mm, "end": v(16.03, -15.81) * mm});
            skLineSegment(sketch, "E2203", {"start": v(16.03, -15.81) * mm, "end": v(15.74, -15.65) * mm});
            skLineSegment(sketch, "E2204", {"start": v(15.74, -15.65) * mm, "end": v(15.42, -15.48) * mm});
            skLineSegment(sketch, "E2205", {"start": v(15.42, -15.48) * mm, "end": v(15.09, -15.3) * mm});
            skLineSegment(sketch, "E2206", {"start": v(15.09, -15.3) * mm, "end": v(14.78, -15.13) * mm});
            skLineSegment(sketch, "E2207", {"start": v(14.78, -15.13) * mm, "end": v(14.52, -15) * mm});
            skLineSegment(sketch, "E2208", {"start": v(14.52, -15) * mm, "end": v(14.38, -14.92) * mm});
            skLineSegment(sketch, "E2209", {"start": v(14.38, -14.92) * mm, "end": v(14.33, -14.9) * mm});
            skLineSegment(sketch, "E2210", {"start": v(14.33, -14.9) * mm, "end": v(14.3, -14.88) * mm});
            skLineSegment(sketch, "E2211", {"start": v(14.3, -14.88) * mm, "end": v(14.21, -14.83) * mm});
            skLineSegment(sketch, "E2212", {"start": v(14.21, -14.83) * mm, "end": v(14.06, -14.75) * mm});
            skLineSegment(sketch, "E2213", {"start": v(14.06, -14.75) * mm, "end": v(13.9, -14.66) * mm});
            skLineSegment(sketch, "E2214", {"start": v(13.9, -14.66) * mm, "end": v(13.78, -14.6) * mm});
            skLineSegment(sketch, "E2215", {"start": v(13.78, -14.6) * mm, "end": v(13.74, -14.57) * mm});
            skLineSegment(sketch, "E2216", {"start": v(13.74, -14.57) * mm, "end": v(13.7, -14.55) * mm});
            skLineSegment(sketch, "E2217", {"start": v(13.7, -14.55) * mm, "end": v(13.53, -14.46) * mm});
            skLineSegment(sketch, "E2218", {"start": v(13.53, -14.46) * mm, "end": v(13.2, -14.28) * mm});
            skLineSegment(sketch, "E2219", {"start": v(13.2, -14.28) * mm, "end": v(12.82, -14.07) * mm});
            skLineSegment(sketch, "E2220", {"start": v(12.82, -14.07) * mm, "end": v(12.52, -13.9) * mm});
            skLineSegment(sketch, "E2221", {"start": v(12.52, -13.9) * mm, "end": v(12.42, -13.85) * mm});
            skLineSegment(sketch, "E2222", {"start": v(12.42, -13.85) * mm, "end": v(12.32, -13.8) * mm});
            skLineSegment(sketch, "E2223", {"start": v(12.32, -13.8) * mm, "end": v(12.03, -13.64) * mm});
            skLineSegment(sketch, "E2224", {"start": v(12.03, -13.64) * mm, "end": v(11.68, -13.45) * mm});
            skLineSegment(sketch, "E2225", {"start": v(11.68, -13.45) * mm, "end": v(11.4, -13.3) * mm});
            skLineSegment(sketch, "E2226", {"start": v(11.4, -13.3) * mm, "end": v(11.29, -13.23) * mm});
            skLineSegment(sketch, "E2227", {"start": v(11.29, -13.23) * mm, "end": v(11.26, -13.22) * mm});
            skLineSegment(sketch, "E2228", {"start": v(11.26, -13.22) * mm, "end": v(11.1, -13.13) * mm});
            skLineSegment(sketch, "E2229", {"start": v(11.1, -13.13) * mm, "end": v(10.61, -12.87) * mm});
            skLineSegment(sketch, "E2230", {"start": v(10.61, -12.87) * mm, "end": v(9.94, -12.55) * mm});
            skLineSegment(sketch, "E2231", {"start": v(9.94, -12.55) * mm, "end": v(9.2, -12.22) * mm});
            skLineSegment(sketch, "E2232", {"start": v(9.2, -12.22) * mm, "end": v(8.55, -11.94) * mm});
            skLineSegment(sketch, "E2233", {"start": v(8.55, -11.94) * mm, "end": v(8.34, -11.85) * mm});
            skLineSegment(sketch, "E2234", {"start": v(8.34, -11.85) * mm, "end": v(8.26, -11.82) * mm});
            skLineSegment(sketch, "E2235", {"start": v(8.26, -11.82) * mm, "end": v(8.02, -11.72) * mm});
            skLineSegment(sketch, "E2236", {"start": v(8.02, -11.72) * mm, "end": v(7.78, -11.62) * mm});
            skLineSegment(sketch, "E2237", {"start": v(7.78, -11.62) * mm, "end": v(7.6, -11.55) * mm});
            skLineSegment(sketch, "E2238", {"start": v(7.6, -11.55) * mm, "end": v(7.48, -11.5) * mm});
            skLineSegment(sketch, "E2239", {"start": v(7.48, -11.5) * mm, "end": v(7.4, -11.45) * mm});
            skLineSegment(sketch, "E2240", {"start": v(7.4, -11.45) * mm, "end": v(7.35, -11.41) * mm});
            skLineSegment(sketch, "E2241", {"start": v(7.35, -11.41) * mm, "end": v(7.31, -11.38) * mm});
            skLineSegment(sketch, "E2242", {"start": v(7.31, -11.38) * mm, "end": v(7.28, -11.35) * mm});
            skLineSegment(sketch, "E2243", {"start": v(7.28, -11.35) * mm, "end": v(7.27, -11.34) * mm});
            skLineSegment(sketch, "E2244", {"start": v(7.27, -11.34) * mm, "end": v(7.25, -11.3) * mm});
            skLineSegment(sketch, "E2245", {"start": v(7.25, -11.3) * mm, "end": v(7.2, -11.22) * mm});
            skLineSegment(sketch, "E2246", {"start": v(7.2, -11.22) * mm, "end": v(7.1, -11.05) * mm});
            skLineSegment(sketch, "E2247", {"start": v(7.1, -11.05) * mm, "end": v(7.02, -10.86) * mm});
            skLineSegment(sketch, "E2248", {"start": v(7.02, -10.86) * mm, "end": v(6.98, -10.74) * mm});
            skLineSegment(sketch, "E2249", {"start": v(6.98, -10.74) * mm, "end": v(6.97, -10.7) * mm});
            skLineSegment(sketch, "E2250", {"start": v(6.97, -10.7) * mm, "end": v(6.96, -10.68) * mm});
            skLineSegment(sketch, "E2251", {"start": v(6.96, -10.68) * mm, "end": v(6.95, -10.62) * mm});
            skLineSegment(sketch, "E2252", {"start": v(6.95, -10.62) * mm, "end": v(6.93, -10.45) * mm});
            skLineSegment(sketch, "E2253", {"start": v(6.93, -10.45) * mm, "end": v(6.9, -10.2) * mm});
            skLineSegment(sketch, "E2254", {"start": v(6.9, -10.2) * mm, "end": v(6.85, -9.89) * mm});
            skLineSegment(sketch, "E2255", {"start": v(6.85, -9.89) * mm, "end": v(6.8, -9.5) * mm});
            skLineSegment(sketch, "E2256", {"start": v(6.8, -9.5) * mm, "end": v(6.74, -9.08) * mm});
            skLineSegment(sketch, "E2257", {"start": v(6.74, -9.08) * mm, "end": v(6.67, -8.62) * mm});
            skLineSegment(sketch, "E2258", {"start": v(6.67, -8.62) * mm, "end": v(6.63, -8.25) * mm});
            skLineSegment(sketch, "E2259", {"start": v(6.63, -8.25) * mm, "end": v(6.6, -8.13) * mm});
            skLineSegment(sketch, "E2260", {"start": v(6.6, -8.13) * mm, "end": v(6.6, -8) * mm});
            skLineSegment(sketch, "E2261", {"start": v(6.6, -8) * mm, "end": v(6.54, -7.63) * mm});
            skLineSegment(sketch, "E2262", {"start": v(6.54, -7.63) * mm, "end": v(6.48, -7.17) * mm});
            skLineSegment(sketch, "E2263", {"start": v(6.48, -7.17) * mm, "end": v(6.43, -6.75) * mm});
            skLineSegment(sketch, "E2264", {"start": v(6.43, -6.75) * mm, "end": v(6.38, -6.37) * mm});
            skLineSegment(sketch, "E2265", {"start": v(6.38, -6.37) * mm, "end": v(6.33, -6.05) * mm});
            skLineSegment(sketch, "E2266", {"start": v(6.33, -6.05) * mm, "end": v(6.3, -5.8) * mm});
            skLineSegment(sketch, "E2267", {"start": v(6.3, -5.8) * mm, "end": v(6.28, -5.64) * mm});
            skLineSegment(sketch, "E2268", {"start": v(6.28, -5.64) * mm, "end": v(6.27, -5.58) * mm});
            skLineSegment(sketch, "E2269", {"start": v(6.27, -5.58) * mm, "end": v(6.27, -5.57) * mm});
            skLineSegment(sketch, "E2270", {"start": v(6.27, -5.57) * mm, "end": v(6.27, -5.56) * mm});
            skLineSegment(sketch, "E2271", {"start": v(6.27, -5.56) * mm, "end": v(6.26, -5.53) * mm});
            skLineSegment(sketch, "E2272", {"start": v(6.26, -5.53) * mm, "end": v(6.25, -5.5) * mm});
            skLineSegment(sketch, "E2273", {"start": v(6.25, -5.5) * mm, "end": v(6.23, -5.46) * mm});
            skLineSegment(sketch, "E2274", {"start": v(6.23, -5.46) * mm, "end": v(6.2, -5.43) * mm});
            skLineSegment(sketch, "E2275", {"start": v(6.2, -5.43) * mm, "end": v(6.17, -5.4) * mm});
            skLineSegment(sketch, "E2276", {"start": v(6.17, -5.4) * mm, "end": v(6.1, -5.37) * mm});
            skLineSegment(sketch, "E2277", {"start": v(6.1, -5.37) * mm, "end": v(6.03, -5.32) * mm});
            skLineSegment(sketch, "E2278", {"start": v(6.03, -5.32) * mm, "end": v(5.96, -5.28) * mm});
            skLineSegment(sketch, "E2279", {"start": v(5.96, -5.28) * mm, "end": v(5.94, -5.27) * mm});
            skLineSegment(sketch, "E2280", {"start": v(5.94, -5.27) * mm, "end": v(5.63, -5.1) * mm});
            skLineSegment(sketch, "E2281", {"start": v(5.63, -5.1) * mm, "end": v(5.6, -4.7) * mm});
            skLineSegment(sketch, "E2282", {"start": v(5.6, -4.7) * mm, "end": v(5.6, -4.66) * mm});
            skLineSegment(sketch, "E2283", {"start": v(5.6, -4.66) * mm, "end": v(5.6, -4.57) * mm});
            skLineSegment(sketch, "E2284", {"start": v(5.6, -4.57) * mm, "end": v(5.6, -4.47) * mm});
            skLineSegment(sketch, "E2285", {"start": v(5.6, -4.47) * mm, "end": v(5.59, -4.4) * mm});
            skLineSegment(sketch, "E2286", {"start": v(5.59, -4.4) * mm, "end": v(5.58, -4.34) * mm});
            skLineSegment(sketch, "E2287", {"start": v(5.58, -4.34) * mm, "end": v(5.57, -4.3) * mm});
            skLineSegment(sketch, "E2288", {"start": v(5.57, -4.3) * mm, "end": v(5.55, -4.27) * mm});
            skLineSegment(sketch, "E2289", {"start": v(5.55, -4.27) * mm, "end": v(5.53, -4.25) * mm});
            skLineSegment(sketch, "E2290", {"start": v(5.53, -4.25) * mm, "end": v(5.52, -4.24) * mm});
            skLineSegment(sketch, "E2291", {"start": v(5.52, -4.24) * mm, "end": v(5.51, -4.23) * mm});
            skLineSegment(sketch, "E2292", {"start": v(5.51, -4.23) * mm, "end": v(5.5, -4.23) * mm});
            skLineSegment(sketch, "E2293", {"start": v(5.5, -4.23) * mm, "end": v(5.46, -4.2) * mm});
            skLineSegment(sketch, "E2294", {"start": v(5.46, -4.2) * mm, "end": v(5.37, -4.13) * mm});
            skLineSegment(sketch, "E2295", {"start": v(5.37, -4.13) * mm, "end": v(5.25, -4.05) * mm});
            skLineSegment(sketch, "E2296", {"start": v(5.25, -4.05) * mm, "end": v(5.15, -3.98) * mm});
            skLineSegment(sketch, "E2297", {"start": v(5.15, -3.98) * mm, "end": v(5.12, -3.96) * mm});
            skLineSegment(sketch, "E2298", {"start": v(5.12, -3.96) * mm, "end": v(4.98, -3.86) * mm});
            skLineSegment(sketch, "E2299", {"start": v(4.98, -3.86) * mm, "end": v(4.55, -3.57) * mm});
            skLineSegment(sketch, "E2300", {"start": v(4.55, -3.57) * mm, "end": v(4.06, -3.23) * mm});
            skLineSegment(sketch, "E2301", {"start": v(4.06, -3.23) * mm, "end": v(3.68, -2.97) * mm});
            skLineSegment(sketch, "E2302", {"start": v(3.68, -2.97) * mm, "end": v(3.5, -2.84) * mm});
            skLineSegment(sketch, "E2303", {"start": v(3.5, -2.84) * mm, "end": v(3.44, -2.8) * mm});
            skLineSegment(sketch, "E2304", {"start": v(3.44, -2.8) * mm, "end": v(3.39, -2.76) * mm});
            skLineSegment(sketch, "E2305", {"start": v(3.39, -2.76) * mm, "end": v(3.24, -2.66) * mm});
            skLineSegment(sketch, "E2306", {"start": v(3.24, -2.66) * mm, "end": v(3, -2.5) * mm});
            skLineSegment(sketch, "E2307", {"start": v(3, -2.5) * mm, "end": v(2.77, -2.33) * mm});
            skLineSegment(sketch, "E2308", {"start": v(2.77, -2.33) * mm, "end": v(2.52, -2.16) * mm});
            skLineSegment(sketch, "E2309", {"start": v(2.52, -2.16) * mm, "end": v(2.28, -2) * mm});
            skLineSegment(sketch, "E2310", {"start": v(2.28, -2) * mm, "end": v(2.06, -1.85) * mm});
            skLineSegment(sketch, "E2311", {"start": v(2.06, -1.85) * mm, "end": v(1.88, -1.73) * mm});
            skLineSegment(sketch, "E2312", {"start": v(1.88, -1.73) * mm, "end": v(1.77, -1.66) * mm});
            skLineSegment(sketch, "E2313", {"start": v(1.77, -1.66) * mm, "end": v(1.74, -1.64) * mm});
            skLineSegment(sketch, "E2314", {"start": v(1.74, -1.64) * mm, "end": v(1.7, -1.61) * mm});
            skLineSegment(sketch, "E2315", {"start": v(1.7, -1.61) * mm, "end": v(1.6, -1.53) * mm});
            skLineSegment(sketch, "E2316", {"start": v(1.6, -1.53) * mm, "end": v(1.44, -1.4) * mm});
            skLineSegment(sketch, "E2317", {"start": v(1.44, -1.4) * mm, "end": v(1.28, -1.27) * mm});
            skLineSegment(sketch, "E2318", {"start": v(1.28, -1.27) * mm, "end": v(1.18, -1.18) * mm});
            skLineSegment(sketch, "E2319", {"start": v(1.18, -1.18) * mm, "end": v(1.15, -1.14) * mm});
            skLineSegment(sketch, "E2320", {"start": v(1.15, -1.14) * mm, "end": v(1.1, -1.09) * mm});
            skLineSegment(sketch, "E2321", {"start": v(1.1, -1.09) * mm, "end": v(0.94, -0.91) * mm});
            skLineSegment(sketch, "E2322", {"start": v(0.94, -0.91) * mm, "end": v(0.81, -0.72) * mm});
            skLineSegment(sketch, "E2323", {"start": v(0.81, -0.72) * mm, "end": v(0.76, -0.53) * mm});
            skLineSegment(sketch, "E2324", {"start": v(0.76, -0.53) * mm, "end": v(0.76, -0.36) * mm});
            skLineSegment(sketch, "E2325", {"start": v(0.76, -0.36) * mm, "end": v(0.76, -0.3) * mm});
            skLineSegment(sketch, "E2326", {"start": v(0.76, -0.3) * mm, "end": v(0.77, -0.28) * mm});
            skLineSegment(sketch, "E2327", {"start": v(0.77, -0.28) * mm, "end": v(0.78, -0.14) * mm});
            skLineSegment(sketch, "E2328", {"start": v(0.78, -0.14) * mm, "end": v(0.8, 0.16) * mm});
            skLineSegment(sketch, "E2329", {"start": v(0.8, 0.16) * mm, "end": v(0.84, 0.54) * mm});
            skLineSegment(sketch, "E2330", {"start": v(0.84, 0.54) * mm, "end": v(0.86, 0.85) * mm});
            skLineSegment(sketch, "E2331", {"start": v(0.86, 0.85) * mm, "end": v(0.87, 0.96) * mm});
            skLineSegment(sketch, "E2332", {"start": v(0.87, 0.96) * mm, "end": v(0.88, 1.07) * mm});
            skLineSegment(sketch, "E2333", {"start": v(0.88, 1.07) * mm, "end": v(0.9, 1.4) * mm});
            skLineSegment(sketch, "E2334", {"start": v(0.9, 1.4) * mm, "end": v(0.93, 1.84) * mm});
            skLineSegment(sketch, "E2335", {"start": v(0.93, 1.84) * mm, "end": v(0.95, 2.3) * mm});
            skLineSegment(sketch, "E2336", {"start": v(0.95, 2.3) * mm, "end": v(0.96, 2.8) * mm});
            skLineSegment(sketch, "E2337", {"start": v(0.96, 2.8) * mm, "end": v(0.96, 3.37) * mm});
            skLineSegment(sketch, "E2338", {"start": v(0.96, 3.37) * mm, "end": v(0.95, 4.04) * mm});
            skLineSegment(sketch, "E2339", {"start": v(0.95, 4.04) * mm, "end": v(0.94, 4.83) * mm});
            skLineSegment(sketch, "E2340", {"start": v(0.94, 4.83) * mm, "end": v(0.93, 5.53) * mm});
            skLineSegment(sketch, "E2341", {"start": v(0.93, 5.53) * mm, "end": v(0.92, 5.76) * mm});
            skLineSegment(sketch, "E2342", {"start": v(0.92, 5.76) * mm, "end": v(0.91, 6) * mm});
            skLineSegment(sketch, "E2343", {"start": v(0.91, 6) * mm, "end": v(0.9, 6.75) * mm});
            skLineSegment(sketch, "E2344", {"start": v(0.9, 6.75) * mm, "end": v(0.88, 7.65) * mm});
            skLineSegment(sketch, "E2345", {"start": v(0.88, 7.65) * mm, "end": v(0.87, 8.43) * mm});
            skLineSegment(sketch, "E2346", {"start": v(0.87, 8.43) * mm, "end": v(0.86, 9.1) * mm});
            skLineSegment(sketch, "E2347", {"start": v(0.86, 9.1) * mm, "end": v(0.85, 9.63) * mm});
            skLineSegment(sketch, "E2348", {"start": v(0.85, 9.63) * mm, "end": v(0.86, 10.02) * mm});
            skLineSegment(sketch, "E2349", {"start": v(0.86, 10.02) * mm, "end": v(0.86, 10.26) * mm});
            skLineSegment(sketch, "E2350", {"start": v(0.86, 10.26) * mm, "end": v(0.87, 10.34) * mm});
            skLineSegment(sketch, "E2351", {"start": v(0.87, 10.34) * mm, "end": v(0.87, 10.33) * mm});
            skLineSegment(sketch, "E2352", {"start": v(0.87, 10.33) * mm, "end": v(0.9, 10.33) * mm});
            skLineSegment(sketch, "E2353", {"start": v(0.9, 10.33) * mm, "end": v(1, 10.32) * mm});
            skLineSegment(sketch, "E2354", {"start": v(1, 10.32) * mm, "end": v(1.1, 10.3) * mm});
            skLineSegment(sketch, "E2355", {"start": v(1.1, 10.3) * mm, "end": v(1.2, 10.3) * mm});
            skLineSegment(sketch, "E2356", {"start": v(1.2, 10.3) * mm, "end": v(1.24, 10.3) * mm});
            skLineSegment(sketch, "E2357", {"start": v(1.24, 10.3) * mm, "end": v(1.27, 10.3) * mm});
            skLineSegment(sketch, "E2358", {"start": v(1.27, 10.3) * mm, "end": v(1.38, 10.29) * mm});
            skLineSegment(sketch, "E2359", {"start": v(1.38, 10.29) * mm, "end": v(1.52, 10.27) * mm});
            skLineSegment(sketch, "E2360", {"start": v(1.52, 10.27) * mm, "end": v(1.64, 10.27) * mm});
            skLineSegment(sketch, "E2361", {"start": v(1.64, 10.27) * mm, "end": v(1.7, 10.26) * mm});
            skLineSegment(sketch, "E2362", {"start": v(1.7, 10.26) * mm, "end": v(1.72, 10.26) * mm});
            skLineSegment(sketch, "E2363", {"start": v(1.72, 10.26) * mm, "end": v(1.77, 10.25) * mm});
            skLineSegment(sketch, "E2364", {"start": v(1.77, 10.25) * mm, "end": v(1.92, 10.24) * mm});
            skLineSegment(sketch, "E2365", {"start": v(1.92, 10.24) * mm, "end": v(2.13, 10.22) * mm});
            skLineSegment(sketch, "E2366", {"start": v(2.13, 10.22) * mm, "end": v(2.39, 10.2) * mm});
            skLineSegment(sketch, "E2367", {"start": v(2.39, 10.2) * mm, "end": v(2.65, 10.18) * mm});
            skLineSegment(sketch, "E2368", {"start": v(2.65, 10.18) * mm, "end": v(2.73, 10.17) * mm});
            skLineSegment(sketch, "E2369", {"start": v(2.73, 10.17) * mm, "end": v(2.78, 10.17) * mm});
            skLineSegment(sketch, "E2370", {"start": v(2.78, 10.17) * mm, "end": v(2.93, 10.15) * mm});
            skLineSegment(sketch, "E2371", {"start": v(2.93, 10.15) * mm, "end": v(3.1, 10.13) * mm});
            skLineSegment(sketch, "E2372", {"start": v(3.1, 10.13) * mm, "end": v(3.22, 10.11) * mm});
            skLineSegment(sketch, "E2373", {"start": v(3.22, 10.11) * mm, "end": v(3.27, 10.1) * mm});
            skLineSegment(sketch, "E2374", {"start": v(3.27, 10.1) * mm, "end": v(3.27, 10.1) * mm});
            skLineSegment(sketch, "E2375", {"start": v(3.27, 10.1) * mm, "end": v(3.28, 10.09) * mm});
            skLineSegment(sketch, "E2376", {"start": v(3.28, 10.09) * mm, "end": v(3.3, 10.04) * mm});
            skLineSegment(sketch, "E2377", {"start": v(3.3, 10.04) * mm, "end": v(3.3, 9.98) * mm});
            skLineSegment(sketch, "E2378", {"start": v(3.3, 9.98) * mm, "end": v(3.3, 9.96) * mm});
            skLineSegment(sketch, "E2379", {"start": v(3.3, 9.96) * mm, "end": v(3.3, 9.94) * mm});
            skLineSegment(sketch, "E2380", {"start": v(3.3, 9.94) * mm, "end": v(3.31, 9.88) * mm});
            skLineSegment(sketch, "E2381", {"start": v(3.31, 9.88) * mm, "end": v(3.33, 9.81) * mm});
            skLineSegment(sketch, "E2382", {"start": v(3.33, 9.81) * mm, "end": v(3.34, 9.8) * mm});
            skLineSegment(sketch, "E2383", {"start": v(3.34, 9.8) * mm, "end": v(3.35, 9.8) * mm});
            skLineSegment(sketch, "E2384", {"start": v(3.35, 9.8) * mm, "end": v(3.38, 9.76) * mm});
            skLineSegment(sketch, "E2385", {"start": v(3.38, 9.76) * mm, "end": v(3.42, 9.77) * mm});
            skLineSegment(sketch, "E2386", {"start": v(3.42, 9.77) * mm, "end": v(3.46, 9.84) * mm});
            skLineSegment(sketch, "E2387", {"start": v(3.46, 9.84) * mm, "end": v(3.48, 9.92) * mm});
            skLineSegment(sketch, "E2388", {"start": v(3.48, 9.92) * mm, "end": v(3.49, 9.94) * mm});
            skLineSegment(sketch, "E2389", {"start": v(3.49, 9.94) * mm, "end": v(3.5, 10.07) * mm});
            skLineSegment(sketch, "E2390", {"start": v(3.5, 10.07) * mm, "end": v(4.03, 10.07) * mm});
            skLineSegment(sketch, "E2391", {"start": v(4.03, 10.07) * mm, "end": v(4.08, 10.48) * mm});
            skLineSegment(sketch, "E2392", {"start": v(4.08, 10.48) * mm, "end": v(4.18, 10.46) * mm});
            skLineSegment(sketch, "E2393", {"start": v(4.18, 10.46) * mm, "end": v(4.24, 10.45) * mm});
            skLineSegment(sketch, "E2394", {"start": v(4.24, 10.45) * mm, "end": v(4.4, 10.42) * mm});
            skLineSegment(sketch, "E2395", {"start": v(4.4, 10.42) * mm, "end": v(4.66, 10.37) * mm});
            skLineSegment(sketch, "E2396", {"start": v(4.66, 10.37) * mm, "end": v(4.91, 10.32) * mm});
            skLineSegment(sketch, "E2397", {"start": v(4.91, 10.32) * mm, "end": v(5.04, 10.3) * mm});
            skLineSegment(sketch, "E2398", {"start": v(5.04, 10.3) * mm, "end": v(5.06, 10.29) * mm});
            skLineSegment(sketch, "E2399", {"start": v(5.06, 10.29) * mm, "end": v(5.07, 10.28) * mm});
            skLineSegment(sketch, "E2400", {"start": v(5.07, 10.28) * mm, "end": v(5.08, 10.27) * mm});
            skLineSegment(sketch, "E2401", {"start": v(5.08, 10.27) * mm, "end": v(5.1, 10.24) * mm});
            skLineSegment(sketch, "E2402", {"start": v(5.1, 10.24) * mm, "end": v(5.11, 10.18) * mm});
            skLineSegment(sketch, "E2403", {"start": v(5.11, 10.18) * mm, "end": v(5.11, 10.12) * mm});
            skLineSegment(sketch, "E2404", {"start": v(5.11, 10.12) * mm, "end": v(5.11, 10.1) * mm});
            skLineSegment(sketch, "E2405", {"start": v(5.11, 10.1) * mm, "end": v(5.11, 9.92) * mm});
            skLineSegment(sketch, "E2406", {"start": v(5.11, 9.92) * mm, "end": v(5.85, 9.7) * mm});
            skLineSegment(sketch, "E2407", {"start": v(5.85, 9.7) * mm, "end": v(6.59, 9.5) * mm});
            skLineSegment(sketch, "E2408", {"start": v(6.59, 9.5) * mm, "end": v(6.64, 9.35) * mm});
            skLineSegment(sketch, "E2409", {"start": v(6.64, 9.35) * mm, "end": v(6.65, 9.32) * mm});
            skLineSegment(sketch, "E2410", {"start": v(6.65, 9.32) * mm, "end": v(6.68, 9.26) * mm});
            skLineSegment(sketch, "E2411", {"start": v(6.68, 9.26) * mm, "end": v(6.73, 9.2) * mm});
            skLineSegment(sketch, "E2412", {"start": v(6.73, 9.2) * mm, "end": v(6.77, 9.15) * mm});
            skLineSegment(sketch, "E2413", {"start": v(6.77, 9.15) * mm, "end": v(6.81, 9.13) * mm});
            skLineSegment(sketch, "E2414", {"start": v(6.81, 9.13) * mm, "end": v(6.86, 9.13) * mm});
            skLineSegment(sketch, "E2415", {"start": v(6.86, 9.13) * mm, "end": v(6.9, 9.15) * mm});
            skLineSegment(sketch, "E2416", {"start": v(6.9, 9.15) * mm, "end": v(6.92, 9.2) * mm});
            skLineSegment(sketch, "E2417", {"start": v(6.92, 9.2) * mm, "end": v(6.94, 9.25) * mm});
            skLineSegment(sketch, "E2418", {"start": v(6.94, 9.25) * mm, "end": v(6.95, 9.27) * mm});
            skLineSegment(sketch, "E2419", {"start": v(6.95, 9.27) * mm, "end": v(6.95, 9.29) * mm});
            skLineSegment(sketch, "E2420", {"start": v(6.95, 9.29) * mm, "end": v(6.97, 9.34) * mm});
            skLineSegment(sketch, "E2421", {"start": v(6.97, 9.34) * mm, "end": v(6.98, 9.37) * mm});
            skLineSegment(sketch, "E2422", {"start": v(6.98, 9.37) * mm, "end": v(6.99, 9.37) * mm});
            skLineSegment(sketch, "E2423", {"start": v(6.99, 9.37) * mm, "end": v(7.01, 9.37) * mm});
            skLineSegment(sketch, "E2424", {"start": v(7.01, 9.37) * mm, "end": v(7.09, 9.35) * mm});
            skLineSegment(sketch, "E2425", {"start": v(7.09, 9.35) * mm, "end": v(7.32, 9.28) * mm});
            skLineSegment(sketch, "E2426", {"start": v(7.32, 9.28) * mm, "end": v(7.67, 9.18) * mm});
            skLineSegment(sketch, "E2427", {"start": v(7.67, 9.18) * mm, "end": v(8, 9.08) * mm});
            skLineSegment(sketch, "E2428", {"start": v(8, 9.08) * mm, "end": v(8.1, 9.05) * mm});
            skLineSegment(sketch, "E2429", {"start": v(8.1, 9.05) * mm, "end": v(8.15, 9.04) * mm});
            skLineSegment(sketch, "E2430", {"start": v(8.15, 9.04) * mm, "end": v(8.28, 9) * mm});
            skLineSegment(sketch, "E2431", {"start": v(8.28, 9) * mm, "end": v(8.46, 8.94) * mm});
            skLineSegment(sketch, "E2432", {"start": v(8.46, 8.94) * mm, "end": v(8.62, 8.9) * mm});
            skLineSegment(sketch, "E2433", {"start": v(8.62, 8.9) * mm, "end": v(8.71, 8.87) * mm});
            skLineSegment(sketch, "E2434", {"start": v(8.71, 8.87) * mm, "end": v(8.74, 8.86) * mm});
            skLineSegment(sketch, "E2435", {"start": v(8.74, 8.86) * mm, "end": v(8.77, 8.86) * mm});
            skLineSegment(sketch, "E2436", {"start": v(8.77, 8.86) * mm, "end": v(8.84, 8.83) * mm});
            skLineSegment(sketch, "E2437", {"start": v(8.84, 8.83) * mm, "end": v(8.94, 8.8) * mm});
            skLineSegment(sketch, "E2438", {"start": v(8.94, 8.8) * mm, "end": v(9.03, 8.77) * mm});
            skLineSegment(sketch, "E2439", {"start": v(9.03, 8.77) * mm, "end": v(9.08, 8.76) * mm});
            skLineSegment(sketch, "E2440", {"start": v(9.08, 8.76) * mm, "end": v(9.1, 8.75) * mm});
            skLineSegment(sketch, "E2441", {"start": v(9.1, 8.75) * mm, "end": v(9.12, 8.74) * mm});
            skLineSegment(sketch, "E2442", {"start": v(9.12, 8.74) * mm, "end": v(9.2, 8.72) * mm});
            skLineSegment(sketch, "E2443", {"start": v(9.2, 8.72) * mm, "end": v(9.25, 8.72) * mm});
            skLineSegment(sketch, "E2444", {"start": v(9.25, 8.72) * mm, "end": v(9.26, 8.72) * mm});
            skLineSegment(sketch, "E2445", {"start": v(9.26, 8.72) * mm, "end": v(9.26, 8.72) * mm});
            skLineSegment(sketch, "E2446", {"start": v(9.26, 8.72) * mm, "end": v(9.27, 8.71) * mm});
            skLineSegment(sketch, "E2447", {"start": v(9.27, 8.71) * mm, "end": v(9.29, 8.68) * mm});
            skLineSegment(sketch, "E2448", {"start": v(9.29, 8.68) * mm, "end": v(9.32, 8.64) * mm});
            skLineSegment(sketch, "E2449", {"start": v(9.32, 8.64) * mm, "end": v(9.34, 8.6) * mm});
            skLineSegment(sketch, "E2450", {"start": v(9.34, 8.6) * mm, "end": v(9.35, 8.58) * mm});
            skLineSegment(sketch, "E2451", {"start": v(9.35, 8.58) * mm, "end": v(9.37, 8.53) * mm});
            skLineSegment(sketch, "E2452", {"start": v(9.37, 8.53) * mm, "end": v(9.44, 8.4) * mm});
            skLineSegment(sketch, "E2453", {"start": v(9.44, 8.4) * mm, "end": v(9.52, 8.3) * mm});
            skLineSegment(sketch, "E2454", {"start": v(9.52, 8.3) * mm, "end": v(9.6, 8.32) * mm});
            skLineSegment(sketch, "E2455", {"start": v(9.6, 8.32) * mm, "end": v(9.66, 8.4) * mm});
            skLineSegment(sketch, "E2456", {"start": v(9.66, 8.4) * mm, "end": v(9.68, 8.43) * mm});
            skLineSegment(sketch, "E2457", {"start": v(9.68, 8.43) * mm, "end": v(9.75, 8.55) * mm});
            skLineSegment(sketch, "E2458", {"start": v(9.75, 8.55) * mm, "end": v(10.1, 8.46) * mm});
            skLineSegment(sketch, "E2459", {"start": v(10.1, 8.46) * mm, "end": v(10.17, 8.43) * mm});
            skLineSegment(sketch, "E2460", {"start": v(10.17, 8.43) * mm, "end": v(10.39, 8.37) * mm});
            skLineSegment(sketch, "E2461", {"start": v(10.39, 8.37) * mm, "end": v(10.6, 8.31) * mm});
            skLineSegment(sketch, "E2462", {"start": v(10.6, 8.31) * mm, "end": v(10.75, 8.27) * mm});
            skLineSegment(sketch, "E2463", {"start": v(10.75, 8.27) * mm, "end": v(10.85, 8.26) * mm});
            skLineSegment(sketch, "E2464", {"start": v(10.85, 8.26) * mm, "end": v(10.91, 8.26) * mm});
            skLineSegment(sketch, "E2465", {"start": v(10.91, 8.26) * mm, "end": v(10.95, 8.28) * mm});
            skLineSegment(sketch, "E2466", {"start": v(10.95, 8.28) * mm, "end": v(10.98, 8.32) * mm});
            skLineSegment(sketch, "E2467", {"start": v(10.98, 8.32) * mm, "end": v(11, 8.36) * mm});
            skLineSegment(sketch, "E2468", {"start": v(11, 8.36) * mm, "end": v(11, 8.38) * mm});
            skLineSegment(sketch, "E2469", {"start": v(11, 8.38) * mm, "end": v(11.01, 8.39) * mm});
            skLineSegment(sketch, "E2470", {"start": v(11.01, 8.39) * mm, "end": v(11.04, 8.4) * mm});
            skLineSegment(sketch, "E2471", {"start": v(11.04, 8.4) * mm, "end": v(11.09, 8.4) * mm});
            skLineSegment(sketch, "E2472", {"start": v(11.09, 8.4) * mm, "end": v(11.18, 8.38) * mm});
            skLineSegment(sketch, "E2473", {"start": v(11.18, 8.38) * mm, "end": v(11.3, 8.33) * mm});
            skLineSegment(sketch, "E2474", {"start": v(11.3, 8.33) * mm, "end": v(11.34, 8.32) * mm});
            skLineSegment(sketch, "E2475", {"start": v(11.34, 8.32) * mm, "end": v(11.38, 8.3) * mm});
            skLineSegment(sketch, "E2476", {"start": v(11.38, 8.3) * mm, "end": v(11.5, 8.25) * mm});
            skLineSegment(sketch, "E2477", {"start": v(11.5, 8.25) * mm, "end": v(11.72, 8.17) * mm});
            skLineSegment(sketch, "E2478", {"start": v(11.72, 8.17) * mm, "end": v(11.96, 8.08) * mm});
            skLineSegment(sketch, "E2479", {"start": v(11.96, 8.08) * mm, "end": v(12.21, 7.98) * mm});
            skLineSegment(sketch, "E2480", {"start": v(12.21, 7.98) * mm, "end": v(12.48, 7.88) * mm});
            skLineSegment(sketch, "E2481", {"start": v(12.48, 7.88) * mm, "end": v(12.74, 7.78) * mm});
            skLineSegment(sketch, "E2482", {"start": v(12.74, 7.78) * mm, "end": v(12.97, 7.7) * mm});
            skLineSegment(sketch, "E2483", {"start": v(12.97, 7.7) * mm, "end": v(13.12, 7.64) * mm});
            skLineSegment(sketch, "E2484", {"start": v(13.12, 7.64) * mm, "end": v(13.17, 7.62) * mm});
            skLineSegment(sketch, "E2485", {"start": v(13.17, 7.62) * mm, "end": v(13.2, 7.6) * mm});
            skLineSegment(sketch, "E2486", {"start": v(13.2, 7.6) * mm, "end": v(13.32, 7.57) * mm});
            skLineSegment(sketch, "E2487", {"start": v(13.32, 7.57) * mm, "end": v(13.44, 7.52) * mm});
            skLineSegment(sketch, "E2488", {"start": v(13.44, 7.52) * mm, "end": v(13.54, 7.48) * mm});
            skLineSegment(sketch, "E2489", {"start": v(13.54, 7.48) * mm, "end": v(13.58, 7.46) * mm});
            skLineSegment(sketch, "E2490", {"start": v(13.58, 7.46) * mm, "end": v(13.6, 7.45) * mm});
            skLineSegment(sketch, "E2491", {"start": v(13.6, 7.45) * mm, "end": v(13.62, 7.44) * mm});
            skLineSegment(sketch, "E2492", {"start": v(13.62, 7.44) * mm, "end": v(13.7, 7.41) * mm});
            skLineSegment(sketch, "E2493", {"start": v(13.7, 7.41) * mm, "end": v(13.84, 7.36) * mm});
            skLineSegment(sketch, "E2494", {"start": v(13.84, 7.36) * mm, "end": v(14, 7.3) * mm});
            skLineSegment(sketch, "E2495", {"start": v(14, 7.3) * mm, "end": v(14.18, 7.23) * mm});
            skLineSegment(sketch, "E2496", {"start": v(14.18, 7.23) * mm, "end": v(14.35, 7.17) * mm});
            skLineSegment(sketch, "E2497", {"start": v(14.35, 7.17) * mm, "end": v(14.5, 7.12) * mm});
            skLineSegment(sketch, "E2498", {"start": v(14.5, 7.12) * mm, "end": v(14.6, 7.09) * mm});
            skLineSegment(sketch, "E2499", {"start": v(14.6, 7.09) * mm, "end": v(14.63, 7.08) * mm});
            skLineSegment(sketch, "E2500", {"start": v(14.63, 7.08) * mm, "end": v(14.63, 7.08) * mm});
            skLineSegment(sketch, "E2501", {"start": v(14.63, 7.08) * mm, "end": v(14.64, 7.08) * mm});
            skLineSegment(sketch, "E2502", {"start": v(14.64, 7.08) * mm, "end": v(14.64, 7.15) * mm});
            skLineSegment(sketch, "E2503", {"start": v(14.64, 7.15) * mm, "end": v(14.65, 7.34) * mm});
            skLineSegment(sketch, "E2504", {"start": v(14.65, 7.34) * mm, "end": v(14.65, 7.6) * mm});
            skLineSegment(sketch, "E2505", {"start": v(14.65, 7.6) * mm, "end": v(14.65, 7.85) * mm});
            skLineSegment(sketch, "E2506", {"start": v(14.65, 7.85) * mm, "end": v(14.65, 7.93) * mm});
            skLineSegment(sketch, "E2507", {"start": v(14.65, 7.93) * mm, "end": v(14.65, 8.76) * mm});
            skLineSegment(sketch, "E2508", {"start": v(14.65, 8.76) * mm, "end": v(14.48, 8.87) * mm});
            skLineSegment(sketch, "E2509", {"start": v(14.48, 8.87) * mm, "end": v(14.45, 8.88) * mm});
            skLineSegment(sketch, "E2510", {"start": v(14.45, 8.88) * mm, "end": v(14.38, 8.93) * mm});
            skLineSegment(sketch, "E2511", {"start": v(14.38, 8.93) * mm, "end": v(14.24, 9.02) * mm});
            skLineSegment(sketch, "E2512", {"start": v(14.24, 9.02) * mm, "end": v(14.08, 9.12) * mm});
            skLineSegment(sketch, "E2513", {"start": v(14.08, 9.12) * mm, "end": v(13.95, 9.2) * mm});
            skLineSegment(sketch, "E2514", {"start": v(13.95, 9.2) * mm, "end": v(13.91, 9.22) * mm});
            skLineSegment(sketch, "E2515", {"start": v(13.91, 9.22) * mm, "end": v(13.87, 9.25) * mm});
            skLineSegment(sketch, "E2516", {"start": v(13.87, 9.25) * mm, "end": v(13.73, 9.34) * mm});
            skLineSegment(sketch, "E2517", {"start": v(13.73, 9.34) * mm, "end": v(13.52, 9.48) * mm});
            skLineSegment(sketch, "E2518", {"start": v(13.52, 9.48) * mm, "end": v(13.31, 9.6) * mm});
            skLineSegment(sketch, "E2519", {"start": v(13.31, 9.6) * mm, "end": v(13.17, 9.7) * mm});
            skLineSegment(sketch, "E2520", {"start": v(13.17, 9.7) * mm, "end": v(13.12, 9.73) * mm});
            skLineSegment(sketch, "E2521", {"start": v(13.12, 9.73) * mm, "end": v(13.08, 9.75) * mm});
            skLineSegment(sketch, "E2522", {"start": v(13.08, 9.75) * mm, "end": v(12.95, 9.83) * mm});
            skLineSegment(sketch, "E2523", {"start": v(12.95, 9.83) * mm, "end": v(12.8, 9.94) * mm});
            skLineSegment(sketch, "E2524", {"start": v(12.8, 9.94) * mm, "end": v(12.65, 10.03) * mm});
            skLineSegment(sketch, "E2525", {"start": v(12.65, 10.03) * mm, "end": v(12.58, 10.08) * mm});
            skLineSegment(sketch, "E2526", {"start": v(12.58, 10.08) * mm, "end": v(12.55, 10.1) * mm});
            skLineSegment(sketch, "E2527", {"start": v(12.55, 10.1) * mm, "end": v(12.53, 10.1) * mm});
            skLineSegment(sketch, "E2528", {"start": v(12.53, 10.1) * mm, "end": v(12.44, 10.16) * mm});
            skLineSegment(sketch, "E2529", {"start": v(12.44, 10.16) * mm, "end": v(12.27, 10.27) * mm});
            skLineSegment(sketch, "E2530", {"start": v(12.27, 10.27) * mm, "end": v(12.06, 10.4) * mm});
            skLineSegment(sketch, "E2531", {"start": v(12.06, 10.4) * mm, "end": v(11.89, 10.51) * mm});
            skLineSegment(sketch, "E2532", {"start": v(11.89, 10.51) * mm, "end": v(11.83, 10.55) * mm});
            skLineSegment(sketch, "E2533", {"start": v(11.83, 10.55) * mm, "end": v(11.8, 10.57) * mm});
            skLineSegment(sketch, "E2534", {"start": v(11.8, 10.57) * mm, "end": v(11.7, 10.63) * mm});
            skLineSegment(sketch, "E2535", {"start": v(11.7, 10.63) * mm, "end": v(11.53, 10.74) * mm});
            skLineSegment(sketch, "E2536", {"start": v(11.53, 10.74) * mm, "end": v(11.3, 10.89) * mm});
            skLineSegment(sketch, "E2537", {"start": v(11.3, 10.89) * mm, "end": v(11.04, 11.05) * mm});
            skLineSegment(sketch, "E2538", {"start": v(11.04, 11.05) * mm, "end": v(10.74, 11.24) * mm});
            skLineSegment(sketch, "E2539", {"start": v(10.74, 11.24) * mm, "end": v(10.42, 11.45) * mm});
            skLineSegment(sketch, "E2540", {"start": v(10.42, 11.45) * mm, "end": v(10.08, 11.67) * mm});
            skLineSegment(sketch, "E2541", {"start": v(10.08, 11.67) * mm, "end": v(9.73, 11.9) * mm});
            skLineSegment(sketch, "E2542", {"start": v(9.73, 11.9) * mm, "end": v(9.37, 12.12) * mm});
            skLineSegment(sketch, "E2543", {"start": v(9.37, 12.12) * mm, "end": v(9.02, 12.34) * mm});
            skLineSegment(sketch, "E2544", {"start": v(9.02, 12.34) * mm, "end": v(8.68, 12.56) * mm});
            skLineSegment(sketch, "E2545", {"start": v(8.68, 12.56) * mm, "end": v(8.35, 12.77) * mm});
            skLineSegment(sketch, "E2546", {"start": v(8.35, 12.77) * mm, "end": v(8.05, 12.96) * mm});
            skLineSegment(sketch, "E2547", {"start": v(8.05, 12.96) * mm, "end": v(7.79, 13.13) * mm});
            skLineSegment(sketch, "E2548", {"start": v(7.79, 13.13) * mm, "end": v(7.56, 13.27) * mm});
            skLineSegment(sketch, "E2549", {"start": v(7.56, 13.27) * mm, "end": v(7.43, 13.36) * mm});
            skLineSegment(sketch, "E2550", {"start": v(7.43, 13.36) * mm, "end": v(7.38, 13.39) * mm});
            skLineSegment(sketch, "E2551", {"start": v(7.38, 13.39) * mm, "end": v(7.34, 13.41) * mm});
            skLineSegment(sketch, "E2552", {"start": v(7.34, 13.41) * mm, "end": v(7.22, 13.5) * mm});
            skLineSegment(sketch, "E2553", {"start": v(7.22, 13.5) * mm, "end": v(7.03, 13.62) * mm});
            skLineSegment(sketch, "E2554", {"start": v(7.03, 13.62) * mm, "end": v(6.82, 13.74) * mm});
            skLineSegment(sketch, "E2555", {"start": v(6.82, 13.74) * mm, "end": v(6.69, 13.83) * mm});
            skLineSegment(sketch, "E2556", {"start": v(6.69, 13.83) * mm, "end": v(6.64, 13.86) * mm});
            skLineSegment(sketch, "E2557", {"start": v(6.64, 13.86) * mm, "end": v(6.6, 13.9) * mm});
            skLineSegment(sketch, "E2558", {"start": v(6.6, 13.9) * mm, "end": v(6.45, 13.99) * mm});
            skLineSegment(sketch, "E2559", {"start": v(6.45, 13.99) * mm, "end": v(6.21, 14.13) * mm});
            skLineSegment(sketch, "E2560", {"start": v(6.21, 14.13) * mm, "end": v(5.98, 14.28) * mm});
            skLineSegment(sketch, "E2561", {"start": v(5.98, 14.28) * mm, "end": v(5.81, 14.39) * mm});
            skLineSegment(sketch, "E2562", {"start": v(5.81, 14.39) * mm, "end": v(5.76, 14.42) * mm});
            skLineSegment(sketch, "E2563", {"start": v(5.76, 14.42) * mm, "end": v(5.29, 14.72) * mm});
            skLineSegment(sketch, "E2564", {"start": v(5.29, 14.72) * mm, "end": v(5.28, 16.12) * mm});
            skLineSegment(sketch, "E2565", {"start": v(5.28, 16.12) * mm, "end": v(5.28, 16.23) * mm});
            skLineSegment(sketch, "E2566", {"start": v(5.28, 16.23) * mm, "end": v(5.27, 16.57) * mm});
            skLineSegment(sketch, "E2567", {"start": v(5.27, 16.57) * mm, "end": v(5.27, 16.92) * mm});
            skLineSegment(sketch, "E2568", {"start": v(5.27, 16.92) * mm, "end": v(5.26, 17.17) * mm});
            skLineSegment(sketch, "E2569", {"start": v(5.26, 17.17) * mm, "end": v(5.26, 17.35) * mm});
            skLineSegment(sketch, "E2570", {"start": v(5.26, 17.35) * mm, "end": v(5.25, 17.47) * mm});
            skLineSegment(sketch, "E2571", {"start": v(5.25, 17.47) * mm, "end": v(5.23, 17.56) * mm});
            skLineSegment(sketch, "E2572", {"start": v(5.23, 17.56) * mm, "end": v(5.21, 17.62) * mm});
            skLineSegment(sketch, "E2573", {"start": v(5.21, 17.62) * mm, "end": v(5.2, 17.66) * mm});
            skLineSegment(sketch, "E2574", {"start": v(5.2, 17.66) * mm, "end": v(5.19, 17.67) * mm});
            skLineSegment(sketch, "E2575", {"start": v(5.19, 17.67) * mm, "end": v(5.17, 17.7) * mm});
            skLineSegment(sketch, "E2576", {"start": v(5.17, 17.7) * mm, "end": v(5.1, 17.82) * mm});
            skLineSegment(sketch, "E2577", {"start": v(5.1, 17.82) * mm, "end": v(4.96, 17.9) * mm});
            skLineSegment(sketch, "E2578", {"start": v(4.96, 17.9) * mm, "end": v(4.74, 17.95) * mm});
            skLineSegment(sketch, "E2579", {"start": v(4.74, 17.95) * mm, "end": v(4.5, 17.96) * mm});
            skLineSegment(sketch, "E2580", {"start": v(4.5, 17.96) * mm, "end": v(4.42, 17.96) * mm});
            skLineSegment(sketch, "E2581", {"start": v(4.42, 17.96) * mm, "end": v(4.36, 17.96) * mm});
            skLineSegment(sketch, "E2582", {"start": v(4.36, 17.96) * mm, "end": v(4.18, 17.96) * mm});
            skLineSegment(sketch, "E2583", {"start": v(4.18, 17.96) * mm, "end": v(4.03, 17.95) * mm});
            skLineSegment(sketch, "E2584", {"start": v(4.03, 17.95) * mm, "end": v(3.93, 17.93) * mm});
            skLineSegment(sketch, "E2585", {"start": v(3.93, 17.93) * mm, "end": v(3.86, 17.9) * mm});
            skLineSegment(sketch, "E2586", {"start": v(3.86, 17.9) * mm, "end": v(3.84, 17.89) * mm});
            skLineSegment(sketch, "E2587", {"start": v(3.84, 17.89) * mm, "end": v(3.82, 17.88) * mm});
            skLineSegment(sketch, "E2588", {"start": v(3.82, 17.88) * mm, "end": v(3.75, 17.84) * mm});
            skLineSegment(sketch, "E2589", {"start": v(3.75, 17.84) * mm, "end": v(3.68, 17.79) * mm});
            skLineSegment(sketch, "E2590", {"start": v(3.68, 17.79) * mm, "end": v(3.63, 17.72) * mm});
            skLineSegment(sketch, "E2591", {"start": v(3.63, 17.72) * mm, "end": v(3.6, 17.62) * mm});
            skLineSegment(sketch, "E2592", {"start": v(3.6, 17.62) * mm, "end": v(3.58, 17.47) * mm});
            skLineSegment(sketch, "E2593", {"start": v(3.58, 17.47) * mm, "end": v(3.58, 17.27) * mm});
            skLineSegment(sketch, "E2594", {"start": v(3.58, 17.27) * mm, "end": v(3.58, 17) * mm});
            skLineSegment(sketch, "E2595", {"start": v(3.58, 17) * mm, "end": v(3.58, 16.72) * mm});
            skLineSegment(sketch, "E2596", {"start": v(3.58, 16.72) * mm, "end": v(3.58, 16.63) * mm});
            skLineSegment(sketch, "E2597", {"start": v(3.58, 16.63) * mm, "end": v(3.58, 16.52) * mm});
            skLineSegment(sketch, "E2598", {"start": v(3.58, 16.52) * mm, "end": v(3.58, 16.2) * mm});
            skLineSegment(sketch, "E2599", {"start": v(3.58, 16.2) * mm, "end": v(3.58, 15.9) * mm});
            skLineSegment(sketch, "E2600", {"start": v(3.58, 15.9) * mm, "end": v(3.57, 15.74) * mm});
            skLineSegment(sketch, "E2601", {"start": v(3.57, 15.74) * mm, "end": v(3.56, 15.7) * mm});
            skLineSegment(sketch, "E2602", {"start": v(3.56, 15.7) * mm, "end": v(3.55, 15.7) * mm});
            skLineSegment(sketch, "E2603", {"start": v(3.55, 15.7) * mm, "end": v(3.5, 15.74) * mm});
            skLineSegment(sketch, "E2604", {"start": v(3.5, 15.74) * mm, "end": v(3.37, 15.83) * mm});
            skLineSegment(sketch, "E2605", {"start": v(3.37, 15.83) * mm, "end": v(3.18, 15.94) * mm});
            skLineSegment(sketch, "E2606", {"start": v(3.18, 15.94) * mm, "end": v(3.02, 16.05) * mm});
            skLineSegment(sketch, "E2607", {"start": v(3.02, 16.05) * mm, "end": v(2.97, 16.08) * mm});
            skLineSegment(sketch, "E2608", {"start": v(2.97, 16.08) * mm, "end": v(2.9, 16.12) * mm});
            skLineSegment(sketch, "E2609", {"start": v(2.9, 16.12) * mm, "end": v(2.7, 16.24) * mm});
            skLineSegment(sketch, "E2610", {"start": v(2.7, 16.24) * mm, "end": v(2.4, 16.43) * mm});
            skLineSegment(sketch, "E2611", {"start": v(2.4, 16.43) * mm, "end": v(2.11, 16.62) * mm});
            skLineSegment(sketch, "E2612", {"start": v(2.11, 16.62) * mm, "end": v(1.92, 16.74) * mm});
            skLineSegment(sketch, "E2613", {"start": v(1.92, 16.74) * mm, "end": v(1.85, 16.78) * mm});
            skLineSegment(sketch, "E2614", {"start": v(1.85, 16.78) * mm, "end": v(1.8, 16.81) * mm});
            skLineSegment(sketch, "E2615", {"start": v(1.8, 16.81) * mm, "end": v(1.67, 16.9) * mm});
            skLineSegment(sketch, "E2616", {"start": v(1.67, 16.9) * mm, "end": v(1.54, 16.98) * mm});
            skLineSegment(sketch, "E2617", {"start": v(1.54, 16.98) * mm, "end": v(1.43, 17.06) * mm});
            skLineSegment(sketch, "E2618", {"start": v(1.43, 17.06) * mm, "end": v(1.35, 17.12) * mm});
            skLineSegment(sketch, "E2619", {"start": v(1.35, 17.12) * mm, "end": v(1.28, 17.18) * mm});
            skLineSegment(sketch, "E2620", {"start": v(1.28, 17.18) * mm, "end": v(1.23, 17.23) * mm});
            skLineSegment(sketch, "E2621", {"start": v(1.23, 17.23) * mm, "end": v(1.18, 17.3) * mm});
            skLineSegment(sketch, "E2622", {"start": v(1.18, 17.3) * mm, "end": v(1.14, 17.36) * mm});
            skLineSegment(sketch, "E2623", {"start": v(1.14, 17.36) * mm, "end": v(1.12, 17.37) * mm});
            skLineSegment(sketch, "E2624", {"start": v(1.12, 17.37) * mm, "end": v(1.04, 17.49) * mm});
            skLineSegment(sketch, "E2625", {"start": v(1.04, 17.49) * mm, "end": v(0.75, 18.05) * mm});
            skLineSegment(sketch, "E2626", {"start": v(0.75, 18.05) * mm, "end": v(0.6, 18.6) * mm});
            skLineSegment(sketch, "E2627", {"start": v(0.6, 18.6) * mm, "end": v(0.58, 18.72) * mm});
            skLineSegment(sketch, "E2628", {"start": v(0.58, 18.72) * mm, "end": v(0.58, 18.74) * mm});
            skLineSegment(sketch, "E2629", {"start": v(0.58, 18.74) * mm, "end": v(0.57, 18.8) * mm});
            skLineSegment(sketch, "E2630", {"start": v(0.57, 18.8) * mm, "end": v(0.57, 18.95) * mm});
            skLineSegment(sketch, "E2631", {"start": v(0.57, 18.95) * mm, "end": v(0.56, 19.15) * mm});
            skLineSegment(sketch, "E2632", {"start": v(0.56, 19.15) * mm, "end": v(0.54, 19.39) * mm});
            skLineSegment(sketch, "E2633", {"start": v(0.54, 19.39) * mm, "end": v(0.53, 19.66) * mm});
            skLineSegment(sketch, "E2634", {"start": v(0.53, 19.66) * mm, "end": v(0.52, 19.96) * mm});
            skLineSegment(sketch, "E2635", {"start": v(0.52, 19.96) * mm, "end": v(0.5, 20.29) * mm});
            skLineSegment(sketch, "E2636", {"start": v(0.5, 20.29) * mm, "end": v(0.5, 20.53) * mm});
            skLineSegment(sketch, "E2637", {"start": v(0.5, 20.53) * mm, "end": v(0.5, 20.62) * mm});
            skLineSegment(sketch, "E2638", {"start": v(0.5, 20.62) * mm, "end": v(0.5, 20.8) * mm});
            skLineSegment(sketch, "E2639", {"start": v(0.5, 20.8) * mm, "end": v(0.48, 21.32) * mm});
            skLineSegment(sketch, "E2640", {"start": v(0.48, 21.32) * mm, "end": v(0.45, 22.02) * mm});
            skLineSegment(sketch, "E2641", {"start": v(0.45, 22.02) * mm, "end": v(0.43, 22.65) * mm});
            skLineSegment(sketch, "E2642", {"start": v(0.43, 22.65) * mm, "end": v(0.42, 23) * mm});
            skLineSegment(sketch, "E2643", {"start": v(0.42, 23) * mm, "end": v(0.41, 23.12) * mm});
            skLineSegment(sketch, "E2644", {"start": v(0.41, 23.12) * mm, "end": v(0.4, 23.23) * mm});
            skLineSegment(sketch, "E2645", {"start": v(0.4, 23.23) * mm, "end": v(0.4, 23.55) * mm});
            skLineSegment(sketch, "E2646", {"start": v(0.4, 23.55) * mm, "end": v(0.38, 24.08) * mm});
            skLineSegment(sketch, "E2647", {"start": v(0.38, 24.08) * mm, "end": v(0.36, 24.64) * mm});
            skLineSegment(sketch, "E2648", {"start": v(0.36, 24.64) * mm, "end": v(0.35, 25.04) * mm});
            skLineSegment(sketch, "E2649", {"start": v(0.35, 25.04) * mm, "end": v(0.35, 25.17) * mm});
            skLineSegment(sketch, "E2650", {"start": v(0.35, 25.17) * mm, "end": v(0.34, 25.3) * mm});
            skLineSegment(sketch, "E2651", {"start": v(0.34, 25.3) * mm, "end": v(0.33, 25.67) * mm});
            skLineSegment(sketch, "E2652", {"start": v(0.33, 25.67) * mm, "end": v(0.32, 26.06) * mm});
            skLineSegment(sketch, "E2653", {"start": v(0.32, 26.06) * mm, "end": v(0.3, 26.37) * mm});
            skLineSegment(sketch, "E2654", {"start": v(0.3, 26.37) * mm, "end": v(0.3, 26.62) * mm});
            skLineSegment(sketch, "E2655", {"start": v(0.3, 26.62) * mm, "end": v(0.28, 26.8) * mm});
            skLineSegment(sketch, "E2656", {"start": v(0.28, 26.8) * mm, "end": v(0.27, 26.96) * mm});
            skLineSegment(sketch, "E2657", {"start": v(0.27, 26.96) * mm, "end": v(0.25, 27.1) * mm});
            skLineSegment(sketch, "E2658", {"start": v(0.25, 27.1) * mm, "end": v(0.23, 27.21) * mm});
            skLineSegment(sketch, "E2659", {"start": v(0.23, 27.21) * mm, "end": v(0.23, 27.25) * mm});
            skLineSegment(sketch, "E2660", {"start": v(0.23, 27.25) * mm, "end": v(0.2, 27.38) * mm});
            skLineSegment(sketch, "E2661", {"start": v(0.2, 27.38) * mm, "end": v(0.13, 27.78) * mm});
            skLineSegment(sketch, "E2662", {"start": v(0.13, 27.78) * mm, "end": v(0, 28.25) * mm});
            skLineSegment(sketch, "E2663", {"start": v(0, 28.25) * mm, "end": v(-0.16, 28.72) * mm});
            skLineSegment(sketch, "E2664", {"start": v(-0.16, 28.72) * mm, "end": v(-0.32, 29.1) * mm});
            skLineSegment(sketch, "E2665", {"start": v(-0.32, 29.1) * mm, "end": v(-0.38, 29.23) * mm});
            skLineSegment(sketch, "E2666", {"start": v(-0.38, 29.23) * mm, "end": v(-0.42, 29.34) * mm});
            skLineSegment(sketch, "E2667", {"start": v(-0.42, 29.34) * mm, "end": v(-0.57, 29.65) * mm});
            skLineSegment(sketch, "E2668", {"start": v(-0.57, 29.65) * mm, "end": v(-0.73, 29.96) * mm});
            skLineSegment(sketch, "E2669", {"start": v(-0.73, 29.96) * mm, "end": v(-0.88, 30.2) * mm});
            skLineSegment(sketch, "E2670", {"start": v(-0.88, 30.2) * mm, "end": v(-1, 30.36) * mm});
            skLineSegment(sketch, "E2671", {"start": v(-1, 30.36) * mm, "end": v(-1.04, 30.4) * mm});
            skLineSegment(sketch, "E2672", {"start": v(-1.04, 30.4) * mm, "end": v(-1.08, 30.46) * mm});
            skLineSegment(sketch, "E2673", {"start": v(-1.08, 30.46) * mm, "end": v(-1.21, 30.6) * mm});
            skLineSegment(sketch, "E2674", {"start": v(-1.21, 30.6) * mm, "end": v(-1.39, 30.71) * mm});
            skLineSegment(sketch, "E2675", {"start": v(-1.39, 30.71) * mm, "end": v(-1.55, 30.76) * mm});
            skLineSegment(sketch, "E2676", {"start": v(-1.55, 30.76) * mm, "end": v(-1.67, 30.75) * mm});
            skLineSegment(sketch, "E2677", {"start": v(-1.67, 30.75) * mm, "end": v(-1.7, 30.73) * mm});
            skLineSegment(sketch, "E2678", {"start": v(0.6, -4.4) * mm, "end": v(0.68, -4.41) * mm});
            skLineSegment(sketch, "E2679", {"start": v(0.68, -4.41) * mm, "end": v(0.92, -4.46) * mm});
            skLineSegment(sketch, "E2680", {"start": v(0.92, -4.46) * mm, "end": v(1.4, -4.56) * mm});
            skLineSegment(sketch, "E2681", {"start": v(1.4, -4.56) * mm, "end": v(1.97, -4.68) * mm});
            skLineSegment(sketch, "E2682", {"start": v(1.97, -4.68) * mm, "end": v(2.6, -4.81) * mm});
            skLineSegment(sketch, "E2683", {"start": v(2.6, -4.81) * mm, "end": v(3.23, -4.94) * mm});
            skLineSegment(sketch, "E2684", {"start": v(3.23, -4.94) * mm, "end": v(3.81, -5.06) * mm});
            skLineSegment(sketch, "E2685", {"start": v(3.81, -5.06) * mm, "end": v(4.29, -5.16) * mm});
            skLineSegment(sketch, "E2686", {"start": v(4.29, -5.16) * mm, "end": v(4.53, -5.2) * mm});
            skLineSegment(sketch, "E2687", {"start": v(4.53, -5.2) * mm, "end": v(4.61, -5.22) * mm});
            skLineSegment(sketch, "E2688", {"start": v(4.61, -5.22) * mm, "end": v(4.66, -5.23) * mm});
            skLineSegment(sketch, "E2689", {"start": v(4.66, -5.23) * mm, "end": v(4.79, -5.26) * mm});
            skLineSegment(sketch, "E2690", {"start": v(4.79, -5.26) * mm, "end": v(4.94, -5.3) * mm});
            skLineSegment(sketch, "E2691", {"start": v(4.94, -5.3) * mm, "end": v(5.05, -5.32) * mm});
            skLineSegment(sketch, "E2692", {"start": v(5.05, -5.32) * mm, "end": v(5.09, -5.34) * mm});
            skLineSegment(sketch, "E2693", {"start": v(5.09, -5.34) * mm, "end": v(5.1, -5.34) * mm});
            skLineSegment(sketch, "E2694", {"start": v(5.1, -5.34) * mm, "end": v(5.1, -5.34) * mm});
            skLineSegment(sketch, "E2695", {"start": v(5.1, -5.34) * mm, "end": v(5.1, -5.37) * mm});
            skLineSegment(sketch, "E2696", {"start": v(5.1, -5.37) * mm, "end": v(5.08, -5.45) * mm});
            skLineSegment(sketch, "E2697", {"start": v(5.08, -5.45) * mm, "end": v(5.06, -5.56) * mm});
            skLineSegment(sketch, "E2698", {"start": v(5.06, -5.56) * mm, "end": v(5.04, -5.66) * mm});
            skLineSegment(sketch, "E2699", {"start": v(5.04, -5.66) * mm, "end": v(5.03, -5.7) * mm});
            skLineSegment(sketch, "E2700", {"start": v(5.03, -5.7) * mm, "end": v(5.02, -5.73) * mm});
            skLineSegment(sketch, "E2701", {"start": v(5.02, -5.73) * mm, "end": v(5, -5.83) * mm});
            skLineSegment(sketch, "E2702", {"start": v(5, -5.83) * mm, "end": v(4.96, -5.96) * mm});
            skLineSegment(sketch, "E2703", {"start": v(4.96, -5.96) * mm, "end": v(4.93, -6.06) * mm});
            skLineSegment(sketch, "E2704", {"start": v(4.93, -6.06) * mm, "end": v(4.92, -6.11) * mm});
            skLineSegment(sketch, "E2705", {"start": v(4.92, -6.11) * mm, "end": v(4.91, -6.13) * mm});
            skLineSegment(sketch, "E2706", {"start": v(4.91, -6.13) * mm, "end": v(4.9, -6.14) * mm});
            skLineSegment(sketch, "E2707", {"start": v(4.9, -6.14) * mm, "end": v(4.89, -6.2) * mm});
            skLineSegment(sketch, "E2708", {"start": v(4.89, -6.2) * mm, "end": v(4.85, -6.36) * mm});
            skLineSegment(sketch, "E2709", {"start": v(4.85, -6.36) * mm, "end": v(4.8, -6.56) * mm});
            skLineSegment(sketch, "E2710", {"start": v(4.8, -6.56) * mm, "end": v(4.74, -6.73) * mm});
            skLineSegment(sketch, "E2711", {"start": v(4.74, -6.73) * mm, "end": v(4.73, -6.78) * mm});
            skLineSegment(sketch, "E2712", {"start": v(4.73, -6.78) * mm, "end": v(4.71, -6.84) * mm});
            skLineSegment(sketch, "E2713", {"start": v(4.71, -6.84) * mm, "end": v(4.66, -7.01) * mm});
            skLineSegment(sketch, "E2714", {"start": v(4.66, -7.01) * mm, "end": v(4.6, -7.22) * mm});
            skLineSegment(sketch, "E2715", {"start": v(4.6, -7.22) * mm, "end": v(4.56, -7.4) * mm});
            skLineSegment(sketch, "E2716", {"start": v(4.56, -7.4) * mm, "end": v(4.53, -7.48) * mm});
            skLineSegment(sketch, "E2717", {"start": v(4.53, -7.48) * mm, "end": v(4.53, -7.5) * mm});
            skLineSegment(sketch, "E2718", {"start": v(4.53, -7.5) * mm, "end": v(4.5, -7.63) * mm});
            skLineSegment(sketch, "E2719", {"start": v(4.5, -7.63) * mm, "end": v(4.38, -8.02) * mm});
            skLineSegment(sketch, "E2720", {"start": v(4.38, -8.02) * mm, "end": v(4.24, -8.52) * mm});
            skLineSegment(sketch, "E2721", {"start": v(4.24, -8.52) * mm, "end": v(4.11, -9) * mm});
            skLineSegment(sketch, "E2722", {"start": v(4.11, -9) * mm, "end": v(4, -9.43) * mm});
            skLineSegment(sketch, "E2723", {"start": v(4, -9.43) * mm, "end": v(3.89, -9.8) * mm});
            skLineSegment(sketch, "E2724", {"start": v(3.89, -9.8) * mm, "end": v(3.8, -10.07) * mm});
            skLineSegment(sketch, "E2725", {"start": v(3.8, -10.07) * mm, "end": v(3.75, -10.26) * mm});
            skLineSegment(sketch, "E2726", {"start": v(3.75, -10.26) * mm, "end": v(3.73, -10.33) * mm});
            skLineSegment(sketch, "E2727", {"start": v(3.73, -10.33) * mm, "end": v(3.73, -10.33) * mm});
            skLineSegment(sketch, "E2728", {"start": v(3.73, -10.33) * mm, "end": v(3.71, -10.33) * mm});
            skLineSegment(sketch, "E2729", {"start": v(3.71, -10.33) * mm, "end": v(3.67, -10.32) * mm});
            skLineSegment(sketch, "E2730", {"start": v(3.67, -10.32) * mm, "end": v(3.62, -10.3) * mm});
            skLineSegment(sketch, "E2731", {"start": v(3.62, -10.3) * mm, "end": v(3.57, -10.3) * mm});
            skLineSegment(sketch, "E2732", {"start": v(3.57, -10.3) * mm, "end": v(3.55, -10.3) * mm});
            skLineSegment(sketch, "E2733", {"start": v(3.55, -10.3) * mm, "end": v(3.5, -10.27) * mm});
            skLineSegment(sketch, "E2734", {"start": v(3.5, -10.27) * mm, "end": v(3.2, -10.22) * mm});
            skLineSegment(sketch, "E2735", {"start": v(3.2, -10.22) * mm, "end": v(2.88, -10.22) * mm});
            skLineSegment(sketch, "E2736", {"start": v(2.88, -10.22) * mm, "end": v(2.82, -10.22) * mm});
            skLineSegment(sketch, "E2737", {"start": v(2.82, -10.22) * mm, "end": v(2.8, -10.22) * mm});
            skLineSegment(sketch, "E2738", {"start": v(2.8, -10.22) * mm, "end": v(2.72, -10.23) * mm});
            skLineSegment(sketch, "E2739", {"start": v(2.72, -10.23) * mm, "end": v(2.65, -10.25) * mm});
            skLineSegment(sketch, "E2740", {"start": v(2.65, -10.25) * mm, "end": v(2.6, -10.26) * mm});
            skLineSegment(sketch, "E2741", {"start": v(2.6, -10.26) * mm, "end": v(2.57, -10.28) * mm});
            skLineSegment(sketch, "E2742", {"start": v(2.57, -10.28) * mm, "end": v(2.55, -10.3) * mm});
            skLineSegment(sketch, "E2743", {"start": v(2.55, -10.3) * mm, "end": v(2.55, -10.35) * mm});
            skLineSegment(sketch, "E2744", {"start": v(2.55, -10.35) * mm, "end": v(2.56, -10.4) * mm});
            skLineSegment(sketch, "E2745", {"start": v(2.56, -10.4) * mm, "end": v(2.58, -10.45) * mm});
            skLineSegment(sketch, "E2746", {"start": v(2.58, -10.45) * mm, "end": v(2.58, -10.46) * mm});
            skLineSegment(sketch, "E2747", {"start": v(2.58, -10.46) * mm, "end": v(2.6, -10.5) * mm});
            skLineSegment(sketch, "E2748", {"start": v(2.6, -10.5) * mm, "end": v(2.66, -10.63) * mm});
            skLineSegment(sketch, "E2749", {"start": v(2.66, -10.63) * mm, "end": v(2.77, -10.81) * mm});
            skLineSegment(sketch, "E2750", {"start": v(2.77, -10.81) * mm, "end": v(2.9, -10.99) * mm});
            skLineSegment(sketch, "E2751", {"start": v(2.9, -10.99) * mm, "end": v(3.01, -11.1) * mm});
            skLineSegment(sketch, "E2752", {"start": v(3.01, -11.1) * mm, "end": v(3.05, -11.14) * mm});
            skLineSegment(sketch, "E2753", {"start": v(3.05, -11.14) * mm, "end": v(3.07, -11.16) * mm});
            skLineSegment(sketch, "E2754", {"start": v(3.07, -11.16) * mm, "end": v(3.14, -11.23) * mm});
            skLineSegment(sketch, "E2755", {"start": v(3.14, -11.23) * mm, "end": v(3.18, -11.28) * mm});
            skLineSegment(sketch, "E2756", {"start": v(3.18, -11.28) * mm, "end": v(3.18, -11.32) * mm});
            skLineSegment(sketch, "E2757", {"start": v(3.18, -11.32) * mm, "end": v(3.15, -11.35) * mm});
            skLineSegment(sketch, "E2758", {"start": v(3.15, -11.35) * mm, "end": v(3.14, -11.36) * mm});
            skLineSegment(sketch, "E2759", {"start": v(3.14, -11.36) * mm, "end": v(3.13, -11.37) * mm});
            skLineSegment(sketch, "E2760", {"start": v(3.13, -11.37) * mm, "end": v(3.1, -11.4) * mm});
            skLineSegment(sketch, "E2761", {"start": v(3.1, -11.4) * mm, "end": v(3.05, -11.47) * mm});
            skLineSegment(sketch, "E2762", {"start": v(3.05, -11.47) * mm, "end": v(2.95, -11.56) * mm});
            skLineSegment(sketch, "E2763", {"start": v(2.95, -11.56) * mm, "end": v(2.84, -11.69) * mm});
            skLineSegment(sketch, "E2764", {"start": v(2.84, -11.69) * mm, "end": v(2.7, -11.83) * mm});
            skLineSegment(sketch, "E2765", {"start": v(2.7, -11.83) * mm, "end": v(2.56, -12) * mm});
            skLineSegment(sketch, "E2766", {"start": v(2.56, -12) * mm, "end": v(2.4, -12.16) * mm});
            skLineSegment(sketch, "E2767", {"start": v(2.4, -12.16) * mm, "end": v(2.24, -12.34) * mm});
            skLineSegment(sketch, "E2768", {"start": v(2.24, -12.34) * mm, "end": v(2.08, -12.52) * mm});
            skLineSegment(sketch, "E2769", {"start": v(2.08, -12.52) * mm, "end": v(1.91, -12.7) * mm});
            skLineSegment(sketch, "E2770", {"start": v(1.91, -12.7) * mm, "end": v(1.76, -12.87) * mm});
            skLineSegment(sketch, "E2771", {"start": v(1.76, -12.87) * mm, "end": v(1.6, -13.03) * mm});
            skLineSegment(sketch, "E2772", {"start": v(1.6, -13.03) * mm, "end": v(1.48, -13.17) * mm});
            skLineSegment(sketch, "E2773", {"start": v(1.48, -13.17) * mm, "end": v(1.36, -13.3) * mm});
            skLineSegment(sketch, "E2774", {"start": v(1.36, -13.3) * mm, "end": v(1.27, -13.4) * mm});
            skLineSegment(sketch, "E2775", {"start": v(1.27, -13.4) * mm, "end": v(1.22, -13.45) * mm});
            skLineSegment(sketch, "E2776", {"start": v(1.22, -13.45) * mm, "end": v(1.2, -13.46) * mm});
            skLineSegment(sketch, "E2777", {"start": v(1.2, -13.46) * mm, "end": v(1.18, -13.5) * mm});
            skLineSegment(sketch, "E2778", {"start": v(1.18, -13.5) * mm, "end": v(1.08, -13.6) * mm});
            skLineSegment(sketch, "E2779", {"start": v(1.08, -13.6) * mm, "end": v(0.88, -13.82) * mm});
            skLineSegment(sketch, "E2780", {"start": v(0.88, -13.82) * mm, "end": v(0.65, -14.07) * mm});
            skLineSegment(sketch, "E2781", {"start": v(0.65, -14.07) * mm, "end": v(0.46, -14.28) * mm});
            skLineSegment(sketch, "E2782", {"start": v(0.46, -14.28) * mm, "end": v(0.4, -14.35) * mm});
            skLineSegment(sketch, "E2783", {"start": v(0.4, -14.35) * mm, "end": v(0.34, -14.41) * mm});
            skLineSegment(sketch, "E2784", {"start": v(0.34, -14.41) * mm, "end": v(0.16, -14.6) * mm});
            skLineSegment(sketch, "E2785", {"start": v(0.16, -14.6) * mm, "end": v(-0.03, -14.82) * mm});
            skLineSegment(sketch, "E2786", {"start": v(-0.03, -14.82) * mm, "end": v(-0.17, -14.96) * mm});
            skLineSegment(sketch, "E2787", {"start": v(-0.17, -14.96) * mm, "end": v(-0.21, -15) * mm});
            skLineSegment(sketch, "E2788", {"start": v(-0.21, -15) * mm, "end": v(-0.23, -15) * mm});
            skLineSegment(sketch, "E2789", {"start": v(-0.23, -15) * mm, "end": v(-0.24, -15) * mm});
            skLineSegment(sketch, "E2790", {"start": v(-0.24, -15) * mm, "end": v(-0.27, -14.97) * mm});
            skLineSegment(sketch, "E2791", {"start": v(-0.27, -14.97) * mm, "end": v(-0.38, -14.86) * mm});
            skLineSegment(sketch, "E2792", {"start": v(-0.38, -14.86) * mm, "end": v(-0.56, -14.68) * mm});
            skLineSegment(sketch, "E2793", {"start": v(-0.56, -14.68) * mm, "end": v(-0.78, -14.46) * mm});
            skLineSegment(sketch, "E2794", {"start": v(-0.78, -14.46) * mm, "end": v(-1.05, -14.2) * mm});
            skLineSegment(sketch, "E2795", {"start": v(-1.05, -14.2) * mm, "end": v(-1.35, -13.9) * mm});
            skLineSegment(sketch, "E2796", {"start": v(-1.35, -13.9) * mm, "end": v(-1.66, -13.58) * mm});
            skLineSegment(sketch, "E2797", {"start": v(-1.66, -13.58) * mm, "end": v(-1.99, -13.25) * mm});
            skLineSegment(sketch, "E2798", {"start": v(-1.99, -13.25) * mm, "end": v(-2.31, -12.92) * mm});
            skLineSegment(sketch, "E2799", {"start": v(-2.31, -12.92) * mm, "end": v(-2.63, -12.6) * mm});
            skLineSegment(sketch, "E2800", {"start": v(-2.63, -12.6) * mm, "end": v(-2.93, -12.3) * mm});
            skLineSegment(sketch, "E2801", {"start": v(-2.93, -12.3) * mm, "end": v(-3.2, -12.03) * mm});
            skLineSegment(sketch, "E2802", {"start": v(-3.2, -12.03) * mm, "end": v(-3.41, -11.8) * mm});
            skLineSegment(sketch, "E2803", {"start": v(-3.41, -11.8) * mm, "end": v(-3.59, -11.62) * mm});
            skLineSegment(sketch, "E2804", {"start": v(-3.59, -11.62) * mm, "end": v(-3.7, -11.5) * mm});
            skLineSegment(sketch, "E2805", {"start": v(-3.7, -11.5) * mm, "end": v(-3.74, -11.46) * mm});
            skLineSegment(sketch, "E2806", {"start": v(-3.74, -11.46) * mm, "end": v(-3.74, -11.45) * mm});
            skLineSegment(sketch, "E2807", {"start": v(-3.74, -11.45) * mm, "end": v(-3.74, -11.45) * mm});
            skLineSegment(sketch, "E2808", {"start": v(-3.74, -11.45) * mm, "end": v(-3.73, -11.43) * mm});
            skLineSegment(sketch, "E2809", {"start": v(-3.73, -11.43) * mm, "end": v(-3.7, -11.38) * mm});
            skLineSegment(sketch, "E2810", {"start": v(-3.7, -11.38) * mm, "end": v(-3.64, -11.31) * mm});
            skLineSegment(sketch, "E2811", {"start": v(-3.64, -11.31) * mm, "end": v(-3.58, -11.25) * mm});
            skLineSegment(sketch, "E2812", {"start": v(-3.58, -11.25) * mm, "end": v(-3.57, -11.23) * mm});
            skLineSegment(sketch, "E2813", {"start": v(-3.57, -11.23) * mm, "end": v(-3.53, -11.19) * mm});
            skLineSegment(sketch, "E2814", {"start": v(-3.53, -11.19) * mm, "end": v(-3.42, -11.05) * mm});
            skLineSegment(sketch, "E2815", {"start": v(-3.42, -11.05) * mm, "end": v(-3.28, -10.83) * mm});
            skLineSegment(sketch, "E2816", {"start": v(-3.28, -10.83) * mm, "end": v(-3.18, -10.63) * mm});
            skLineSegment(sketch, "E2817", {"start": v(-3.18, -10.63) * mm, "end": v(-3.15, -10.53) * mm});
            skLineSegment(sketch, "E2818", {"start": v(-3.15, -10.53) * mm, "end": v(-3.15, -10.49) * mm});
            skLineSegment(sketch, "E2819", {"start": v(-3.15, -10.49) * mm, "end": v(-3.15, -10.48) * mm});
            skLineSegment(sketch, "E2820", {"start": v(-3.15, -10.48) * mm, "end": v(-3.15, -10.45) * mm});
            skLineSegment(sketch, "E2821", {"start": v(-3.15, -10.45) * mm, "end": v(-3.17, -10.42) * mm});
            skLineSegment(sketch, "E2822", {"start": v(-3.17, -10.42) * mm, "end": v(-3.2, -10.4) * mm});
            skLineSegment(sketch, "E2823", {"start": v(-3.2, -10.4) * mm, "end": v(-3.25, -10.39) * mm});
            skLineSegment(sketch, "E2824", {"start": v(-3.25, -10.39) * mm, "end": v(-3.27, -10.39) * mm});
            skLineSegment(sketch, "E2825", {"start": v(-3.27, -10.39) * mm, "end": v(-3.32, -10.38) * mm});
            skLineSegment(sketch, "E2826", {"start": v(-3.32, -10.38) * mm, "end": v(-3.46, -10.37) * mm});
            skLineSegment(sketch, "E2827", {"start": v(-3.46, -10.37) * mm, "end": v(-3.7, -10.37) * mm});
            skLineSegment(sketch, "E2828", {"start": v(-3.7, -10.37) * mm, "end": v(-3.92, -10.4) * mm});
            skLineSegment(sketch, "E2829", {"start": v(-3.92, -10.4) * mm, "end": v(-4.06, -10.43) * mm});
            skLineSegment(sketch, "E2830", {"start": v(-4.06, -10.43) * mm, "end": v(-4.1, -10.44) * mm});
            skLineSegment(sketch, "E2831", {"start": v(-4.1, -10.44) * mm, "end": v(-4.13, -10.45) * mm});
            skLineSegment(sketch, "E2832", {"start": v(-4.13, -10.45) * mm, "end": v(-4.19, -10.47) * mm});
            skLineSegment(sketch, "E2833", {"start": v(-4.19, -10.47) * mm, "end": v(-4.25, -10.48) * mm});
            skLineSegment(sketch, "E2834", {"start": v(-4.25, -10.48) * mm, "end": v(-4.3, -10.49) * mm});
            skLineSegment(sketch, "E2835", {"start": v(-4.3, -10.49) * mm, "end": v(-4.32, -10.49) * mm});
            skLineSegment(sketch, "E2836", {"start": v(-4.32, -10.49) * mm, "end": v(-4.33, -10.48) * mm});
            skLineSegment(sketch, "E2837", {"start": v(-4.33, -10.48) * mm, "end": v(-4.33, -10.48) * mm});
            skLineSegment(sketch, "E2838", {"start": v(-4.33, -10.48) * mm, "end": v(-4.36, -10.4) * mm});
            skLineSegment(sketch, "E2839", {"start": v(-4.36, -10.4) * mm, "end": v(-4.44, -10.18) * mm});
            skLineSegment(sketch, "E2840", {"start": v(-4.44, -10.18) * mm, "end": v(-4.54, -9.88) * mm});
            skLineSegment(sketch, "E2841", {"start": v(-4.54, -9.88) * mm, "end": v(-4.63, -9.6) * mm});
            skLineSegment(sketch, "E2842", {"start": v(-4.63, -9.6) * mm, "end": v(-4.66, -9.5) * mm});
            skLineSegment(sketch, "E2843", {"start": v(-4.66, -9.5) * mm, "end": v(-4.7, -9.4) * mm});
            skLineSegment(sketch, "E2844", {"start": v(-4.7, -9.4) * mm, "end": v(-4.8, -9.07) * mm});
            skLineSegment(sketch, "E2845", {"start": v(-4.8, -9.07) * mm, "end": v(-4.94, -8.6) * mm});
            skLineSegment(sketch, "E2846", {"start": v(-4.94, -8.6) * mm, "end": v(-5.08, -8.17) * mm});
            skLineSegment(sketch, "E2847", {"start": v(-5.08, -8.17) * mm, "end": v(-5.17, -7.9) * mm});
            skLineSegment(sketch, "E2848", {"start": v(-5.17, -7.9) * mm, "end": v(-5.2, -7.8) * mm});
            skLineSegment(sketch, "E2849", {"start": v(-5.2, -7.8) * mm, "end": v(-5.22, -7.73) * mm});
            skLineSegment(sketch, "E2850", {"start": v(-5.22, -7.73) * mm, "end": v(-5.3, -7.48) * mm});
            skLineSegment(sketch, "E2851", {"start": v(-5.3, -7.48) * mm, "end": v(-5.41, -7.13) * mm});
            skLineSegment(sketch, "E2852", {"start": v(-5.41, -7.13) * mm, "end": v(-5.51, -6.8) * mm});
            skLineSegment(sketch, "E2853", {"start": v(-5.51, -6.8) * mm, "end": v(-5.58, -6.61) * mm});
            skLineSegment(sketch, "E2854", {"start": v(-5.58, -6.61) * mm, "end": v(-5.6, -6.55) * mm});
            skLineSegment(sketch, "E2855", {"start": v(-5.6, -6.55) * mm, "end": v(-5.61, -6.5) * mm});
            skLineSegment(sketch, "E2856", {"start": v(-5.61, -6.5) * mm, "end": v(-5.67, -6.33) * mm});
            skLineSegment(sketch, "E2857", {"start": v(-5.67, -6.33) * mm, "end": v(-5.73, -6.14) * mm});
            skLineSegment(sketch, "E2858", {"start": v(-5.73, -6.14) * mm, "end": v(-5.78, -5.98) * mm});
            skLineSegment(sketch, "E2859", {"start": v(-5.78, -5.98) * mm, "end": v(-5.8, -5.9) * mm});
            skLineSegment(sketch, "E2860", {"start": v(-5.8, -5.9) * mm, "end": v(-5.81, -5.88) * mm});
            skLineSegment(sketch, "E2861", {"start": v(-5.81, -5.88) * mm, "end": v(-5.82, -5.86) * mm});
            skLineSegment(sketch, "E2862", {"start": v(-5.82, -5.86) * mm, "end": v(-5.85, -5.76) * mm});
            skLineSegment(sketch, "E2863", {"start": v(-5.85, -5.76) * mm, "end": v(-5.87, -5.7) * mm});
            skLineSegment(sketch, "E2864", {"start": v(-5.87, -5.7) * mm, "end": v(-5.87, -5.7) * mm});
            skLineSegment(sketch, "E2865", {"start": v(-5.87, -5.7) * mm, "end": v(-5.87, -5.69) * mm});
            skLineSegment(sketch, "E2866", {"start": v(-5.87, -5.69) * mm, "end": v(-5.84, -5.67) * mm});
            skLineSegment(sketch, "E2867", {"start": v(-5.84, -5.67) * mm, "end": v(-5.78, -5.64) * mm});
            skLineSegment(sketch, "E2868", {"start": v(-5.78, -5.64) * mm, "end": v(-5.69, -5.6) * mm});
            skLineSegment(sketch, "E2869", {"start": v(-5.69, -5.6) * mm, "end": v(-5.6, -5.58) * mm});
            skLineSegment(sketch, "E2870", {"start": v(-5.6, -5.58) * mm, "end": v(-5.57, -5.57) * mm});
            skLineSegment(sketch, "E2871", {"start": v(-5.57, -5.57) * mm, "end": v(-5.47, -5.55) * mm});
            skLineSegment(sketch, "E2872", {"start": v(-5.47, -5.55) * mm, "end": v(-5.05, -5.43) * mm});
            skLineSegment(sketch, "E2873", {"start": v(-5.05, -5.43) * mm, "end": v(-4.71, -5.34) * mm});
            skLineSegment(sketch, "E2874", {"start": v(-4.71, -5.34) * mm, "end": v(-4.66, -5.33) * mm});
            skLineSegment(sketch, "E2875", {"start": v(-4.66, -5.33) * mm, "end": v(-4.63, -5.32) * mm});
            skLineSegment(sketch, "E2876", {"start": v(-4.63, -5.32) * mm, "end": v(-4.56, -5.3) * mm});
            skLineSegment(sketch, "E2877", {"start": v(-4.56, -5.3) * mm, "end": v(-4.44, -5.27) * mm});
            skLineSegment(sketch, "E2878", {"start": v(-4.44, -5.27) * mm, "end": v(-4.3, -5.23) * mm});
            skLineSegment(sketch, "E2879", {"start": v(-4.3, -5.23) * mm, "end": v(-4.2, -5.2) * mm});
            skLineSegment(sketch, "E2880", {"start": v(-4.2, -5.2) * mm, "end": v(-4.17, -5.2) * mm});
            skLineSegment(sketch, "E2881", {"start": v(-4.17, -5.2) * mm, "end": v(-4.15, -5.19) * mm});
            skLineSegment(sketch, "E2882", {"start": v(-4.15, -5.19) * mm, "end": v(-4.08, -5.17) * mm});
            skLineSegment(sketch, "E2883", {"start": v(-4.08, -5.17) * mm, "end": v(-3.94, -5.13) * mm});
            skLineSegment(sketch, "E2884", {"start": v(-3.94, -5.13) * mm, "end": v(-3.76, -5.08) * mm});
            skLineSegment(sketch, "E2885", {"start": v(-3.76, -5.08) * mm, "end": v(-3.54, -5.02) * mm});
            skLineSegment(sketch, "E2886", {"start": v(-3.54, -5.02) * mm, "end": v(-3.29, -4.95) * mm});
            skLineSegment(sketch, "E2887", {"start": v(-3.29, -4.95) * mm, "end": v(-3.02, -4.88) * mm});
            skLineSegment(sketch, "E2888", {"start": v(-3.02, -4.88) * mm, "end": v(-2.74, -4.8) * mm});
            skLineSegment(sketch, "E2889", {"start": v(-2.74, -4.8) * mm, "end": v(-2.52, -4.74) * mm});
            skLineSegment(sketch, "E2890", {"start": v(-2.52, -4.74) * mm, "end": v(-2.44, -4.72) * mm});
            skLineSegment(sketch, "E2891", {"start": v(-2.44, -4.72) * mm, "end": v(-2.37, -4.7) * mm});
            skLineSegment(sketch, "E2892", {"start": v(-2.37, -4.7) * mm, "end": v(-2.16, -4.64) * mm});
            skLineSegment(sketch, "E2893", {"start": v(-2.16, -4.64) * mm, "end": v(-1.9, -4.57) * mm});
            skLineSegment(sketch, "E2894", {"start": v(-1.9, -4.57) * mm, "end": v(-1.65, -4.5) * mm});
            skLineSegment(sketch, "E2895", {"start": v(-1.65, -4.5) * mm, "end": v(-1.44, -4.44) * mm});
            skLineSegment(sketch, "E2896", {"start": v(-1.44, -4.44) * mm, "end": v(-1.26, -4.4) * mm});
            skLineSegment(sketch, "E2897", {"start": v(-1.26, -4.4) * mm, "end": v(-1.13, -4.36) * mm});
            skLineSegment(sketch, "E2898", {"start": v(-1.13, -4.36) * mm, "end": v(-1.05, -4.34) * mm});
            skLineSegment(sketch, "E2899", {"start": v(-1.05, -4.34) * mm, "end": v(-1.02, -4.34) * mm});
            skLineSegment(sketch, "E2900", {"start": v(-1.02, -4.34) * mm, "end": v(-1.01, -4.34) * mm});
            skLineSegment(sketch, "E2901", {"start": v(-1.01, -4.34) * mm, "end": v(-1.01, -4.34) * mm});
            skLineSegment(sketch, "E2902", {"start": v(-1.01, -4.34) * mm, "end": v(-1, -4.4) * mm});
            skLineSegment(sketch, "E2903", {"start": v(-1, -4.4) * mm, "end": v(-0.97, -4.49) * mm});
            skLineSegment(sketch, "E2904", {"start": v(-0.97, -4.49) * mm, "end": v(-0.97, -4.5) * mm});
            skLineSegment(sketch, "E2905", {"start": v(-0.97, -4.5) * mm, "end": v(-0.96, -4.53) * mm});
            skLineSegment(sketch, "E2906", {"start": v(-0.96, -4.53) * mm, "end": v(-0.95, -4.58) * mm});
            skLineSegment(sketch, "E2907", {"start": v(-0.95, -4.58) * mm, "end": v(-0.92, -4.67) * mm});
            skLineSegment(sketch, "E2908", {"start": v(-0.92, -4.67) * mm, "end": v(-0.88, -4.76) * mm});
            skLineSegment(sketch, "E2909", {"start": v(-0.88, -4.76) * mm, "end": v(-0.86, -4.83) * mm});
            skLineSegment(sketch, "E2910", {"start": v(-0.86, -4.83) * mm, "end": v(-0.85, -4.85) * mm});
            skLineSegment(sketch, "E2911", {"start": v(-0.85, -4.85) * mm, "end": v(-0.84, -4.86) * mm});
            skLineSegment(sketch, "E2912", {"start": v(-0.84, -4.86) * mm, "end": v(-0.81, -4.92) * mm});
            skLineSegment(sketch, "E2913", {"start": v(-0.81, -4.92) * mm, "end": v(-0.76, -5) * mm});
            skLineSegment(sketch, "E2914", {"start": v(-0.76, -5) * mm, "end": v(-0.7, -5.1) * mm});
            skLineSegment(sketch, "E2915", {"start": v(-0.7, -5.1) * mm, "end": v(-0.64, -5.18) * mm});
            skLineSegment(sketch, "E2916", {"start": v(-0.64, -5.18) * mm, "end": v(-0.58, -5.26) * mm});
            skLineSegment(sketch, "E2917", {"start": v(-0.58, -5.26) * mm, "end": v(-0.53, -5.32) * mm});
            skLineSegment(sketch, "E2918", {"start": v(-0.53, -5.32) * mm, "end": v(-0.49, -5.36) * mm});
            skLineSegment(sketch, "E2919", {"start": v(-0.49, -5.36) * mm, "end": v(-0.46, -5.37) * mm});
            skLineSegment(sketch, "E2920", {"start": v(-0.46, -5.37) * mm, "end": v(-0.46, -5.37) * mm});
            skLineSegment(sketch, "E2921", {"start": v(-0.46, -5.37) * mm, "end": v(-0.44, -5.37) * mm});
            skLineSegment(sketch, "E2922", {"start": v(-0.44, -5.37) * mm, "end": v(-0.4, -5.35) * mm});
            skLineSegment(sketch, "E2923", {"start": v(-0.4, -5.35) * mm, "end": v(-0.34, -5.28) * mm});
            skLineSegment(sketch, "E2924", {"start": v(-0.34, -5.28) * mm, "end": v(-0.27, -5.19) * mm});
            skLineSegment(sketch, "E2925", {"start": v(-0.27, -5.19) * mm, "end": v(-0.2, -5.07) * mm});
            skLineSegment(sketch, "E2926", {"start": v(-0.2, -5.07) * mm, "end": v(-0.13, -4.93) * mm});
            skLineSegment(sketch, "E2927", {"start": v(-0.13, -4.93) * mm, "end": v(-0.06, -4.78) * mm});
            skLineSegment(sketch, "E2928", {"start": v(-0.06, -4.78) * mm, "end": v(-0.01, -4.64) * mm});
            skLineSegment(sketch, "E2929", {"start": v(-0.01, -4.64) * mm, "end": v(0.01, -4.54) * mm});
            skLineSegment(sketch, "E2930", {"start": v(0.01, -4.54) * mm, "end": v(0.02, -4.5) * mm});
            skLineSegment(sketch, "E2931", {"start": v(0.02, -4.5) * mm, "end": v(0.02, -4.48) * mm});
            skLineSegment(sketch, "E2932", {"start": v(0.02, -4.48) * mm, "end": v(0.04, -4.42) * mm});
            skLineSegment(sketch, "E2933", {"start": v(0.04, -4.42) * mm, "end": v(0.06, -4.36) * mm});
            skLineSegment(sketch, "E2934", {"start": v(0.06, -4.36) * mm, "end": v(0.08, -4.31) * mm});
            skLineSegment(sketch, "E2935", {"start": v(0.08, -4.31) * mm, "end": v(0.1, -4.3) * mm});
            skLineSegment(sketch, "E2936", {"start": v(0.1, -4.3) * mm, "end": v(0.1, -4.3) * mm});
            skLineSegment(sketch, "E2937", {"start": v(0.1, -4.3) * mm, "end": v(0.11, -4.3) * mm});
            skLineSegment(sketch, "E2938", {"start": v(0.11, -4.3) * mm, "end": v(0.15, -4.3) * mm});
            skLineSegment(sketch, "E2939", {"start": v(0.15, -4.3) * mm, "end": v(0.27, -4.33) * mm});
            skLineSegment(sketch, "E2940", {"start": v(0.27, -4.33) * mm, "end": v(0.42, -4.36) * mm});
            skLineSegment(sketch, "E2941", {"start": v(0.42, -4.36) * mm, "end": v(0.56, -4.39) * mm});
            skLineSegment(sketch, "E2942", {"start": v(0.56, -4.39) * mm, "end": v(0.6, -4.4) * mm});
            skSolve(sketch);
        }
        {
            var Q0;
            Q0=makeQuery(id+"F0.imprint","IMPRINT",FACE,{"disambiguationData":[TD([[makeQuery(id+"F0.imprint","IMPRINT",EDGE,{"derivedFrom":sQuery(id+"F0.wireOp",EDGE,"E0")}),1.0]])]});
            extrude(context, id + "F1", {"entities" : qUnion([Q0]), "depth" : 12.7 * mm});
        }
        {
            var Q0;
            Q0=makeQuery(id+"F1.opExtrude","SWEPT_FACE",FACE,{"disambiguationData":[OSD([sQuery(id+"F0.wireOp",EDGE,"E887")])]});
            cPlane(context, id + "F2", {"entities" : qUnion([Q0]), "cplaneType" : CPlaneType.OFFSET, "offset" : 45 * mm, "width" : 150 * mm, "height" : 150 * mm});
        }
        {
            var Q0;
            Q0=qCreatedBy(id+"F2.planeOp",FACE);
            var sketch = newSketch(context, id + "F3", { "sketchPlane" : qUnion([Q0])});
            skCircle(sketch, "E2943", {"center": v(-37.1, 7.17) * mm, "radius": 1.5 * mm});
            skSolve(sketch);
        }
        {
            var Q0;
            Q0 = qSketchRegion(id + "F3", true);
            extrude(context, id + "F4", {"entities" : qUnion([Q0]), "operationType" : NewBodyOperationType.REMOVE, "oppositeDirection" : true, "depth" : 67.1 * mm});
        }
    });
